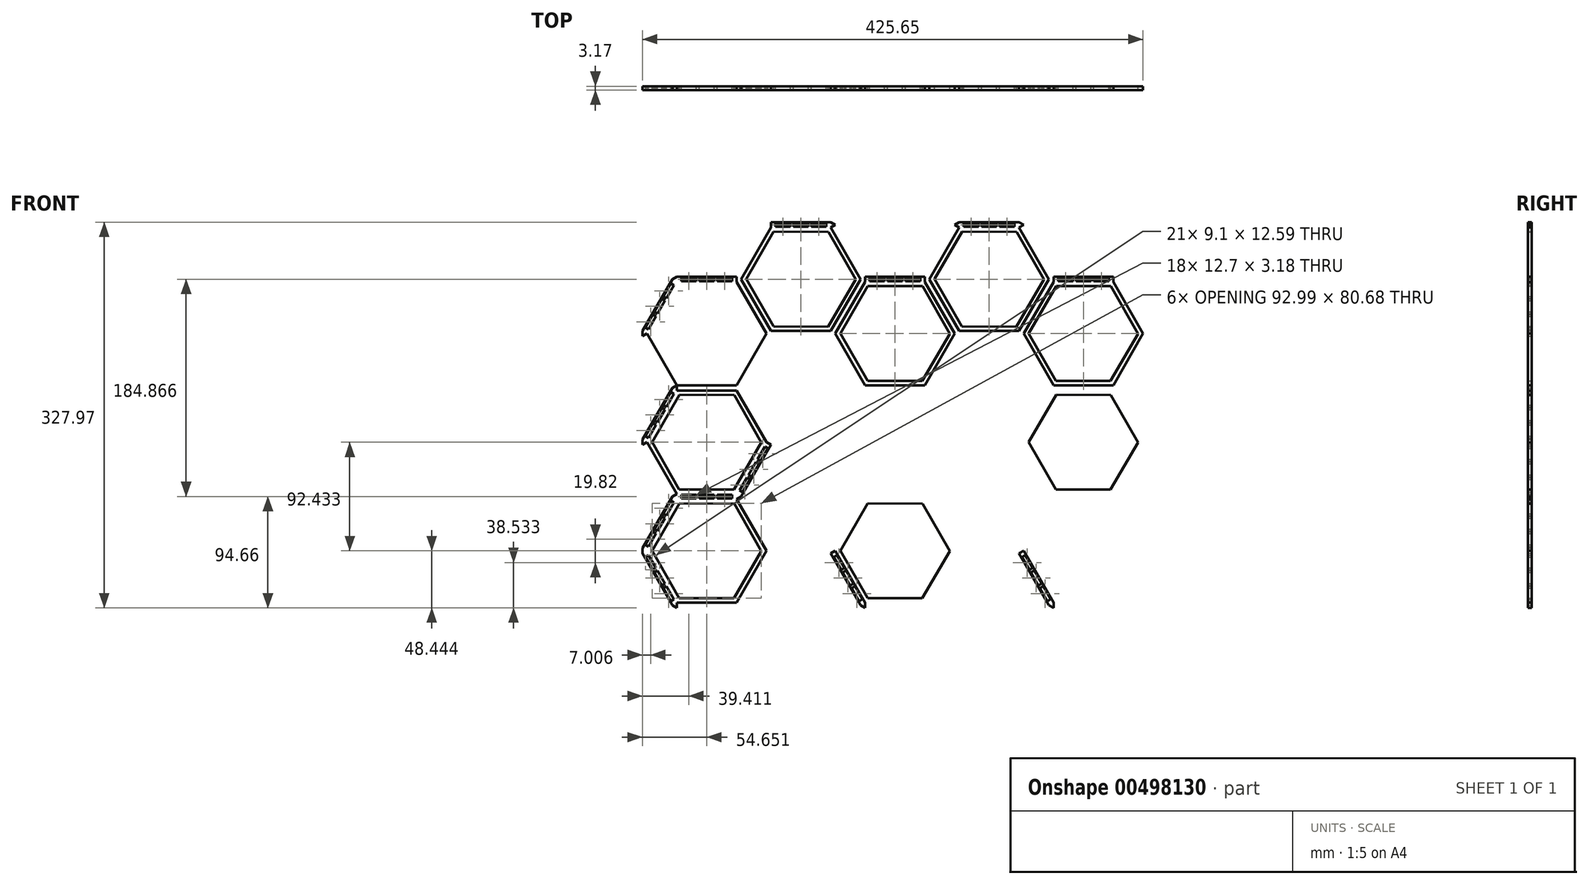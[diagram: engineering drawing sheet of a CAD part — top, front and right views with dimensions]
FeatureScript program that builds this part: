
annotation { "Feature Type Name" : "Feature", "Feature Type Description" : "" }
export const myFeature = defineFeature(function(context is Context, id is Id, definition is map)
    precondition{}
    {
        {
            var Q0;
            Q0=qCreatedBy(makeId("Front.planeOp"),FACE);
            var sketch = newSketch(context, id + "F0", { "sketchPlane" : qUnion([Q0])});
            skLineSegment(sketch, "E0", {"start": v(-1207.39, 180.55) * mm, "end": v(-1156.59, 180.55) * mm});
            skLineSegment(sketch, "E1", {"start": v(-1207.39, 185) * mm, "end": v(-1207.39, 180.55) * mm});
            skLineSegment(sketch, "E2", {"start": v(-1156.59, 185) * mm, "end": v(-1156.59, 180.55) * mm});
            skPoint(sketch, "E3.endSnap0", {"position": v(-1156.59, 182.78) * mm});
            skLineSegment(sketch, "E4", {"start": v(-1207.39, 182.78) * mm, "end": v(-1156.59, 182.78) * mm, "construction": true});
            skLineSegment(sketch, "E5", {"start": v(-1207.39, 185) * mm, "end": v(-1156.59, 185) * mm});
            skLineSegment(sketch, "E6.left", {"start": v(-1160.4, 181.19) * mm, "end": v(-1160.4, 184.36) * mm});
            skLineSegment(sketch, "E6.right", {"start": v(-1203.58, 181.19) * mm, "end": v(-1203.58, 184.36) * mm});
            skPoint(sketch, "E6.middle", {"position": v(-1181.99, 182.78) * mm});
            skLineSegment(sketch, "E7", {"start": v(-1181.99, 184.36) * mm, "end": v(-1181.99, 181.19) * mm, "construction": true});
            skLineSegment(sketch, "E8", {"start": v(-1190.88, 184.36) * mm, "end": v(-1190.88, 181.19) * mm});
            skLineSegment(sketch, "E9.MirrorCS", {"start": v(-1173.1, 184.36) * mm, "end": v(-1173.1, 181.19) * mm});
            skLineSegment(sketch, "E10", {"start": v(-1188.34, 184.36) * mm, "end": v(-1188.34, 181.19) * mm});
            skLineSegment(sketch, "E11.MirrorCS", {"start": v(-1175.64, 184.36) * mm, "end": v(-1175.64, 181.19) * mm});
            skLineSegment(sketch, "E12", {"start": v(-1203.58, 184.36) * mm, "end": v(-1190.88, 184.36) * mm});
            skLineSegment(sketch, "E13", {"start": v(-1203.58, 181.19) * mm, "end": v(-1190.88, 181.19) * mm});
            skLineSegment(sketch, "E14", {"start": v(-1188.34, 181.19) * mm, "end": v(-1181.99, 181.19) * mm});
            skLineSegment(sketch, "E15", {"start": v(-1188.34, 184.36) * mm, "end": v(-1181.99, 184.36) * mm});
            skLineSegment(sketch, "E16", {"start": v(-1181.99, 184.36) * mm, "end": v(-1175.64, 184.36) * mm});
            skLineSegment(sketch, "E17", {"start": v(-1181.99, 181.19) * mm, "end": v(-1175.64, 181.19) * mm});
            skLineSegment(sketch, "E18", {"start": v(-1173.1, 184.36) * mm, "end": v(-1160.4, 184.36) * mm});
            skLineSegment(sketch, "E19", {"start": v(-1173.1, 181.19) * mm, "end": v(-1160.4, 181.19) * mm});
            skLineSegment(sketch, "E20", {"start": v(-1152.74, 182.78) * mm, "end": v(-1156.59, 180.55) * mm});
            skLineSegment(sketch, "E21", {"start": v(-1211.24, 182.78) * mm, "end": v(-1207.39, 180.55) * mm});
            skPoint(sketch, "E22.endSnap0", {"position": v(-1209.31, 181.67) * mm});
            skLineSegment(sketch, "E23.0", {"start": v(-1207.39, 180.55) * mm, "end": v(-1211.24, 182.78) * mm, "construction": true});
            skLineSegment(sketch, "E24", {"start": v(-1207.39, 272.99) * mm, "end": v(-1156.59, 272.99) * mm});
            skLineSegment(sketch, "E25", {"start": v(-1207.39, 277.43) * mm, "end": v(-1207.39, 272.99) * mm});
            skLineSegment(sketch, "E26", {"start": v(-1156.59, 277.43) * mm, "end": v(-1156.59, 272.99) * mm});
            skPoint(sketch, "E27.endSnap0", {"position": v(-1156.59, 275.21) * mm});
            skLineSegment(sketch, "E28", {"start": v(-1207.39, 275.21) * mm, "end": v(-1156.59, 275.21) * mm, "construction": true});
            skLineSegment(sketch, "E29", {"start": v(-1207.39, 277.43) * mm, "end": v(-1156.59, 277.43) * mm});
            skLineSegment(sketch, "E30", {"start": v(-1236.64, 231.22) * mm, "end": v(-1232.79, 229) * mm});
            skLineSegment(sketch, "E31.left", {"start": v(-1160.4, 273.62) * mm, "end": v(-1160.4, 276.8) * mm});
            skLineSegment(sketch, "E31.right", {"start": v(-1203.58, 273.62) * mm, "end": v(-1203.58, 276.8) * mm});
            skPoint(sketch, "E31.middle", {"position": v(-1181.99, 275.21) * mm});
            skLineSegment(sketch, "E32", {"start": v(-1181.99, 276.8) * mm, "end": v(-1181.99, 273.62) * mm, "construction": true});
            skLineSegment(sketch, "E33", {"start": v(-1190.88, 276.8) * mm, "end": v(-1190.88, 273.62) * mm});
            skLineSegment(sketch, "E34.MirrorCS", {"start": v(-1173.1, 276.8) * mm, "end": v(-1173.1, 273.62) * mm});
            skLineSegment(sketch, "E35", {"start": v(-1188.34, 276.8) * mm, "end": v(-1188.34, 273.62) * mm});
            skLineSegment(sketch, "E36.MirrorCS", {"start": v(-1175.64, 276.8) * mm, "end": v(-1175.64, 273.62) * mm});
            skLineSegment(sketch, "E37", {"start": v(-1203.58, 276.8) * mm, "end": v(-1190.88, 276.8) * mm});
            skLineSegment(sketch, "E38", {"start": v(-1203.58, 273.62) * mm, "end": v(-1190.88, 273.62) * mm});
            skLineSegment(sketch, "E39", {"start": v(-1188.34, 273.62) * mm, "end": v(-1181.99, 273.62) * mm});
            skLineSegment(sketch, "E40", {"start": v(-1188.34, 276.8) * mm, "end": v(-1181.99, 276.8) * mm});
            skLineSegment(sketch, "E41", {"start": v(-1181.99, 276.8) * mm, "end": v(-1175.64, 276.8) * mm});
            skLineSegment(sketch, "E42", {"start": v(-1181.99, 273.62) * mm, "end": v(-1175.64, 273.62) * mm});
            skLineSegment(sketch, "E43", {"start": v(-1173.1, 276.8) * mm, "end": v(-1160.4, 276.8) * mm});
            skLineSegment(sketch, "E44", {"start": v(-1173.1, 273.62) * mm, "end": v(-1160.4, 273.62) * mm});
            skLineSegment(sketch, "E45", {"start": v(-1156.59, 272.99) * mm, "end": v(-1131.19, 229) * mm});
            skLineSegment(sketch, "E46", {"start": v(-1152.74, 275.21) * mm, "end": v(-1156.59, 272.99) * mm});
            skLineSegment(sketch, "E47", {"start": v(-1152.74, 275.21) * mm, "end": v(-1127.34, 231.22) * mm});
            skLineSegment(sketch, "E48.left", {"start": v(-1132.54, 232.61) * mm, "end": v(-1129.8, 234.2) * mm});
            skLineSegment(sketch, "E48.right", {"start": v(-1154.13, 270) * mm, "end": v(-1151.38, 271.6) * mm});
            skPoint(sketch, "E48.middle", {"position": v(-1141.96, 252.1) * mm});
            skLineSegment(sketch, "E49", {"start": v(-1140.59, 252.9) * mm, "end": v(-1143.34, 251.3) * mm, "construction": true});
            skLineSegment(sketch, "E50", {"start": v(-1145.03, 260.6) * mm, "end": v(-1147.78, 259) * mm});
            skLineSegment(sketch, "E51.MirrorCS", {"start": v(-1136.14, 245.2) * mm, "end": v(-1138.9, 243.6) * mm});
            skLineSegment(sketch, "E52", {"start": v(-1143.76, 258.4) * mm, "end": v(-1146.51, 256.8) * mm});
            skLineSegment(sketch, "E53.MirrorCS", {"start": v(-1137.41, 247.4) * mm, "end": v(-1140.16, 245.8) * mm});
            skLineSegment(sketch, "E54", {"start": v(-1151.38, 271.6) * mm, "end": v(-1145.03, 260.6) * mm});
            skLineSegment(sketch, "E55", {"start": v(-1154.13, 270) * mm, "end": v(-1147.78, 259) * mm});
            skLineSegment(sketch, "E56", {"start": v(-1146.51, 256.8) * mm, "end": v(-1143.34, 251.3) * mm});
            skLineSegment(sketch, "E57", {"start": v(-1143.76, 258.4) * mm, "end": v(-1140.59, 252.9) * mm});
            skLineSegment(sketch, "E58", {"start": v(-1140.59, 252.9) * mm, "end": v(-1137.41, 247.4) * mm});
            skLineSegment(sketch, "E59", {"start": v(-1143.34, 251.3) * mm, "end": v(-1140.16, 245.8) * mm});
            skLineSegment(sketch, "E60", {"start": v(-1136.14, 245.2) * mm, "end": v(-1129.8, 234.2) * mm});
            skLineSegment(sketch, "E61", {"start": v(-1138.9, 243.6) * mm, "end": v(-1132.54, 232.61) * mm});
            skLineSegment(sketch, "E62", {"start": v(-1232.79, 229) * mm, "end": v(-1207.39, 272.99) * mm});
            skLineSegment(sketch, "E63", {"start": v(-1211.24, 275.21) * mm, "end": v(-1207.39, 272.99) * mm});
            skPoint(sketch, "E64.endSnap0", {"position": v(-1209.31, 274.1) * mm});
            skLineSegment(sketch, "E65", {"start": v(-1236.64, 231.22) * mm, "end": v(-1211.24, 275.21) * mm});
            skLineSegment(sketch, "E66.left", {"start": v(-1209.84, 270) * mm, "end": v(-1212.6, 271.6) * mm});
            skLineSegment(sketch, "E66.right", {"start": v(-1231.43, 232.61) * mm, "end": v(-1234.18, 234.2) * mm});
            skPoint(sketch, "E66.middle", {"position": v(-1222.01, 252.1) * mm});
            skLineSegment(sketch, "E67", {"start": v(-1223.39, 252.9) * mm, "end": v(-1220.64, 251.3) * mm, "construction": true});
            skLineSegment(sketch, "E68", {"start": v(-1227.83, 245.2) * mm, "end": v(-1225.08, 243.6) * mm});
            skLineSegment(sketch, "E69.MirrorCS", {"start": v(-1218.94, 260.6) * mm, "end": v(-1216.2, 259) * mm});
            skLineSegment(sketch, "E70", {"start": v(-1226.56, 247.4) * mm, "end": v(-1223.81, 245.8) * mm});
            skLineSegment(sketch, "E71.MirrorCS", {"start": v(-1220.21, 258.4) * mm, "end": v(-1217.46, 256.8) * mm});
            skLineSegment(sketch, "E72", {"start": v(-1234.18, 234.2) * mm, "end": v(-1227.83, 245.2) * mm});
            skLineSegment(sketch, "E73", {"start": v(-1231.43, 232.61) * mm, "end": v(-1225.08, 243.6) * mm});
            skLineSegment(sketch, "E74", {"start": v(-1223.81, 245.8) * mm, "end": v(-1220.64, 251.3) * mm});
            skLineSegment(sketch, "E75", {"start": v(-1226.56, 247.4) * mm, "end": v(-1223.39, 252.9) * mm});
            skLineSegment(sketch, "E76", {"start": v(-1223.39, 252.9) * mm, "end": v(-1220.21, 258.4) * mm});
            skLineSegment(sketch, "E77", {"start": v(-1220.64, 251.3) * mm, "end": v(-1217.46, 256.8) * mm});
            skLineSegment(sketch, "E78", {"start": v(-1218.94, 260.6) * mm, "end": v(-1212.6, 271.6) * mm});
            skLineSegment(sketch, "E79", {"start": v(-1216.2, 259) * mm, "end": v(-1209.84, 270) * mm});
            skLineSegment(sketch, "E80.0", {"start": v(-1207.39, 272.99) * mm, "end": v(-1211.24, 275.21) * mm, "construction": true});
            skLineSegment(sketch, "E81", {"start": v(-1131.19, 229) * mm, "end": v(-1127.34, 231.22) * mm});
            skLineSegment(sketch, "E82.MirrorCS", {"start": v(-1211.24, 182.78) * mm, "end": v(-1207.39, 185) * mm});
            skLineSegment(sketch, "E83.MirrorCS", {"start": v(-1140.59, 205.1) * mm, "end": v(-1143.34, 206.68) * mm, "construction": true});
            skLineSegment(sketch, "E84.MirrorCS", {"start": v(-1223.39, 205.1) * mm, "end": v(-1220.64, 206.68) * mm, "construction": true});
            skLineSegment(sketch, "E85.MirrorCS", {"start": v(-1181.99, 181.19) * mm, "end": v(-1181.99, 184.36) * mm, "construction": true});
            skLineSegment(sketch, "E86.MirrorCS", {"start": v(-1207.39, 185) * mm, "end": v(-1211.24, 182.78) * mm, "construction": true});
            skLineSegment(sketch, "E87.MirrorCS", {"start": v(-1152.74, 182.78) * mm, "end": v(-1156.59, 185) * mm});
            skLineSegment(sketch, "E88.MirrorCS", {"start": v(-1154.13, 187.98) * mm, "end": v(-1151.38, 186.4) * mm});
            skLineSegment(sketch, "E89.MirrorCS", {"start": v(-1220.21, 199.6) * mm, "end": v(-1217.46, 201.18) * mm});
            skLineSegment(sketch, "E90.MirrorCS", {"start": v(-1175.64, 181.19) * mm, "end": v(-1175.64, 184.36) * mm});
            skLineSegment(sketch, "E91.MirrorCS", {"start": v(-1156.59, 180.55) * mm, "end": v(-1156.59, 185) * mm});
            skLineSegment(sketch, "E92.MirrorCS", {"start": v(-1190.88, 181.19) * mm, "end": v(-1190.88, 184.36) * mm});
            skLineSegment(sketch, "E93.MirrorCS", {"start": v(-1145.03, 197.4) * mm, "end": v(-1147.78, 198.98) * mm});
            skLineSegment(sketch, "E94.MirrorCS", {"start": v(-1188.34, 181.19) * mm, "end": v(-1188.34, 184.36) * mm});
            skLineSegment(sketch, "E95.MirrorCS", {"start": v(-1209.84, 187.98) * mm, "end": v(-1212.6, 186.4) * mm});
            skLineSegment(sketch, "E96.MirrorCS", {"start": v(-1231.43, 225.38) * mm, "end": v(-1234.18, 223.79) * mm});
            skLineSegment(sketch, "E97.MirrorCS", {"start": v(-1226.56, 210.6) * mm, "end": v(-1223.81, 212.18) * mm});
            skLineSegment(sketch, "E98.MirrorCS", {"start": v(-1236.64, 226.77) * mm, "end": v(-1232.79, 229) * mm});
            skLineSegment(sketch, "E99.MirrorCS", {"start": v(-1143.76, 199.6) * mm, "end": v(-1146.51, 201.18) * mm});
            skLineSegment(sketch, "E100.MirrorCS", {"start": v(-1173.1, 181.19) * mm, "end": v(-1173.1, 184.36) * mm});
            skLineSegment(sketch, "E101.MirrorCS", {"start": v(-1227.83, 212.8) * mm, "end": v(-1225.08, 214.38) * mm});
            skLineSegment(sketch, "E102.MirrorCS", {"start": v(-1132.54, 225.38) * mm, "end": v(-1129.8, 223.79) * mm});
            skLineSegment(sketch, "E103.MirrorCS", {"start": v(-1203.58, 184.36) * mm, "end": v(-1203.58, 181.19) * mm});
            skLineSegment(sketch, "E104.MirrorCS", {"start": v(-1136.14, 212.8) * mm, "end": v(-1138.9, 214.38) * mm});
            skLineSegment(sketch, "E105.MirrorCS", {"start": v(-1131.19, 229) * mm, "end": v(-1127.34, 226.77) * mm});
            skLineSegment(sketch, "E106.MirrorCS", {"start": v(-1137.41, 210.6) * mm, "end": v(-1140.16, 212.18) * mm});
            skLineSegment(sketch, "E107.MirrorCS", {"start": v(-1218.94, 197.4) * mm, "end": v(-1216.2, 198.98) * mm});
            skLineSegment(sketch, "E108.MirrorCS", {"start": v(-1160.4, 184.36) * mm, "end": v(-1160.4, 181.19) * mm});
            skLineSegment(sketch, "E109.MirrorCS", {"start": v(-1146.51, 201.18) * mm, "end": v(-1143.34, 206.68) * mm});
            skLineSegment(sketch, "E110.MirrorCS", {"start": v(-1223.81, 212.18) * mm, "end": v(-1220.64, 206.68) * mm});
            skLineSegment(sketch, "E111.MirrorCS", {"start": v(-1140.59, 205.1) * mm, "end": v(-1137.41, 210.6) * mm});
            skLineSegment(sketch, "E112.MirrorCS", {"start": v(-1207.39, 180.55) * mm, "end": v(-1207.39, 185) * mm});
            skLineSegment(sketch, "E113.MirrorCS", {"start": v(-1143.34, 206.68) * mm, "end": v(-1140.16, 212.18) * mm});
            skLineSegment(sketch, "E114.MirrorCS", {"start": v(-1143.76, 199.6) * mm, "end": v(-1140.59, 205.1) * mm});
            skLineSegment(sketch, "E115.MirrorCS", {"start": v(-1220.64, 206.68) * mm, "end": v(-1217.46, 201.18) * mm});
            skLineSegment(sketch, "E116.MirrorCS", {"start": v(-1138.9, 214.38) * mm, "end": v(-1132.54, 225.38) * mm});
            skLineSegment(sketch, "E117.MirrorCS", {"start": v(-1236.64, 226.77) * mm, "end": v(-1211.24, 182.78) * mm});
            skLineSegment(sketch, "E118.MirrorCS", {"start": v(-1156.59, 185) * mm, "end": v(-1131.19, 229) * mm});
            skLineSegment(sketch, "E119.MirrorCS", {"start": v(-1151.38, 186.4) * mm, "end": v(-1145.03, 197.4) * mm});
            skLineSegment(sketch, "E120.MirrorCS", {"start": v(-1231.43, 225.38) * mm, "end": v(-1225.08, 214.38) * mm});
            skLineSegment(sketch, "E121.MirrorCS", {"start": v(-1216.2, 198.98) * mm, "end": v(-1209.84, 187.98) * mm});
            skPoint(sketch, "E122.MirrorP", {"position": v(-1141.96, 205.89) * mm});
            skLineSegment(sketch, "E123.MirrorCS", {"start": v(-1136.14, 212.8) * mm, "end": v(-1129.8, 223.79) * mm});
            skPoint(sketch, "E124.MirrorP", {"position": v(-1209.31, 183.89) * mm});
            skLineSegment(sketch, "E125.MirrorCS", {"start": v(-1226.56, 210.6) * mm, "end": v(-1223.39, 205.1) * mm});
            skPoint(sketch, "E126.MirrorP", {"position": v(-1222.01, 205.89) * mm});
            skLineSegment(sketch, "E127.MirrorCS", {"start": v(-1154.13, 187.98) * mm, "end": v(-1147.78, 198.98) * mm});
            skLineSegment(sketch, "E128.MirrorCS", {"start": v(-1152.74, 182.78) * mm, "end": v(-1127.34, 226.77) * mm});
            skLineSegment(sketch, "E129.MirrorCS", {"start": v(-1232.79, 229) * mm, "end": v(-1207.39, 185) * mm});
            skLineSegment(sketch, "E130.MirrorCS", {"start": v(-1218.94, 197.4) * mm, "end": v(-1212.6, 186.4) * mm});
            skLineSegment(sketch, "E131.MirrorCS", {"start": v(-1234.18, 223.79) * mm, "end": v(-1227.83, 212.8) * mm});
            skLineSegment(sketch, "E132.MirrorCS", {"start": v(-1223.39, 205.1) * mm, "end": v(-1220.21, 199.6) * mm});
            skLineSegment(sketch, "E133", {"start": v(-1127.34, 231.22) * mm, "end": v(-1127.34, 226.77) * mm});
            skLineSegment(sketch, "E134", {"start": v(-1156.59, 185) * mm, "end": v(-1152.74, 182.78) * mm});
            skLineSegment(sketch, "E135.left", {"start": v(-1129.8, 223.79) * mm, "end": v(-1132.54, 225.38) * mm});
            skLineSegment(sketch, "E135.right", {"start": v(-1151.38, 186.4) * mm, "end": v(-1154.13, 187.98) * mm});
            skLineSegment(sketch, "E136", {"start": v(-1143.34, 206.68) * mm, "end": v(-1140.59, 205.1) * mm, "construction": true});
            skLineSegment(sketch, "E137", {"start": v(-1147.78, 198.98) * mm, "end": v(-1145.03, 197.4) * mm});
            skLineSegment(sketch, "E138.MirrorCS", {"start": v(-1138.9, 214.38) * mm, "end": v(-1136.14, 212.8) * mm});
            skLineSegment(sketch, "E139", {"start": v(-1146.51, 201.18) * mm, "end": v(-1143.76, 199.6) * mm});
            skLineSegment(sketch, "E140.MirrorCS", {"start": v(-1140.16, 212.18) * mm, "end": v(-1137.41, 210.6) * mm});
            skLineSegment(sketch, "E141.0", {"start": v(-1127.34, 226.77) * mm, "end": v(-1131.19, 229) * mm, "construction": true});
            skLineSegment(sketch, "E142.MirrorCS", {"start": v(-1156.59, 180.55) * mm, "end": v(-1152.74, 182.78) * mm});
            skLineSegment(sketch, "E143", {"start": v(-1156.59, 277.43) * mm, "end": v(-1152.74, 275.21) * mm});
            skLineSegment(sketch, "E144.MirrorCS", {"start": v(-1143.34, 251.3) * mm, "end": v(-1140.59, 252.9) * mm, "construction": true});
            skLineSegment(sketch, "E145.MirrorCS", {"start": v(-1127.34, 231.22) * mm, "end": v(-1131.19, 229) * mm, "construction": true});
            skLineSegment(sketch, "E146.MirrorCS", {"start": v(-1140.16, 245.8) * mm, "end": v(-1137.41, 247.4) * mm});
            skLineSegment(sketch, "E147.MirrorCS", {"start": v(-1129.8, 234.2) * mm, "end": v(-1132.54, 232.61) * mm});
            skLineSegment(sketch, "E148.MirrorCS", {"start": v(-1151.38, 271.6) * mm, "end": v(-1154.13, 270) * mm});
            skLineSegment(sketch, "E149.MirrorCS", {"start": v(-1146.51, 256.8) * mm, "end": v(-1143.76, 258.4) * mm});
            skLineSegment(sketch, "E150.MirrorCS", {"start": v(-1156.59, 272.99) * mm, "end": v(-1152.74, 275.21) * mm});
            skLineSegment(sketch, "E151.MirrorCS", {"start": v(-1147.78, 259) * mm, "end": v(-1145.03, 260.6) * mm});
            skLineSegment(sketch, "E152.MirrorCS", {"start": v(-1138.9, 243.6) * mm, "end": v(-1136.14, 245.2) * mm});
            skLineSegment(sketch, "E153.MirrorCS", {"start": v(-1127.34, 226.77) * mm, "end": v(-1127.34, 231.22) * mm});
            skLineSegment(sketch, "E154", {"start": v(-1236.64, 231.22) * mm, "end": v(-1236.64, 226.77) * mm});
            skLineSegment(sketch, "E155", {"start": v(-1207.39, 277.43) * mm, "end": v(-1211.24, 275.21) * mm});
            skLineSegment(sketch, "E156.0", {"start": v(-1135.5, 228.85) * mm, "end": v(-1158.86, 188.66) * mm});
            skLineSegment(sketch, "E156.1", {"start": v(-1158.86, 188.66) * mm, "end": v(-1205.36, 188.8) * mm});
            skLineSegment(sketch, "E156.2", {"start": v(-1205.36, 188.8) * mm, "end": v(-1228.49, 229.14) * mm});
            skLineSegment(sketch, "E156.3", {"start": v(-1228.49, 229.14) * mm, "end": v(-1205.11, 269.33) * mm});
            skLineSegment(sketch, "E156.4", {"start": v(-1205.11, 269.33) * mm, "end": v(-1158.62, 269.19) * mm});
            skLineSegment(sketch, "E156.5", {"start": v(-1158.62, 269.19) * mm, "end": v(-1135.5, 228.85) * mm});
            skPoint(sketch, "E156.0.midPoint", {"position": v(-1147.18, 208.75) * mm});
            skLineSegment(sketch, "E157", {"start": v(-1207.39, 365.42) * mm, "end": v(-1156.59, 365.42) * mm});
            skLineSegment(sketch, "E158", {"start": v(-1207.39, 369.87) * mm, "end": v(-1207.39, 365.42) * mm});
            skLineSegment(sketch, "E159", {"start": v(-1156.59, 369.87) * mm, "end": v(-1156.59, 365.42) * mm});
            skPoint(sketch, "E160.endSnap0", {"position": v(-1156.59, 367.64) * mm});
            skLineSegment(sketch, "E161", {"start": v(-1207.39, 367.64) * mm, "end": v(-1156.59, 367.64) * mm, "construction": true});
            skLineSegment(sketch, "E162", {"start": v(-1207.39, 369.87) * mm, "end": v(-1156.59, 369.87) * mm});
            skLineSegment(sketch, "E163", {"start": v(-1236.64, 323.65) * mm, "end": v(-1232.79, 321.43) * mm});
            skLineSegment(sketch, "E164.left", {"start": v(-1160.4, 366.06) * mm, "end": v(-1160.4, 369.23) * mm});
            skLineSegment(sketch, "E164.right", {"start": v(-1203.58, 366.06) * mm, "end": v(-1203.58, 369.23) * mm});
            skPoint(sketch, "E164.middle", {"position": v(-1181.99, 367.64) * mm});
            skLineSegment(sketch, "E165", {"start": v(-1181.99, 369.23) * mm, "end": v(-1181.99, 366.06) * mm, "construction": true});
            skLineSegment(sketch, "E166", {"start": v(-1190.88, 369.23) * mm, "end": v(-1190.88, 366.06) * mm});
            skLineSegment(sketch, "E167.MirrorCS", {"start": v(-1173.1, 369.23) * mm, "end": v(-1173.1, 366.06) * mm});
            skLineSegment(sketch, "E168", {"start": v(-1188.34, 369.23) * mm, "end": v(-1188.34, 366.06) * mm});
            skLineSegment(sketch, "E169.MirrorCS", {"start": v(-1175.64, 369.23) * mm, "end": v(-1175.64, 366.06) * mm});
            skLineSegment(sketch, "E170", {"start": v(-1203.58, 369.23) * mm, "end": v(-1190.88, 369.23) * mm});
            skLineSegment(sketch, "E171", {"start": v(-1203.58, 366.06) * mm, "end": v(-1190.88, 366.06) * mm});
            skLineSegment(sketch, "E172", {"start": v(-1188.34, 366.06) * mm, "end": v(-1181.99, 366.06) * mm});
            skLineSegment(sketch, "E173", {"start": v(-1188.34, 369.23) * mm, "end": v(-1181.99, 369.23) * mm});
            skLineSegment(sketch, "E174", {"start": v(-1181.99, 369.23) * mm, "end": v(-1175.64, 369.23) * mm});
            skLineSegment(sketch, "E175", {"start": v(-1181.99, 366.06) * mm, "end": v(-1175.64, 366.06) * mm});
            skLineSegment(sketch, "E176", {"start": v(-1173.1, 369.23) * mm, "end": v(-1160.4, 369.23) * mm});
            skLineSegment(sketch, "E177", {"start": v(-1173.1, 366.06) * mm, "end": v(-1160.4, 366.06) * mm});
            skLineSegment(sketch, "E178", {"start": v(-1156.59, 365.42) * mm, "end": v(-1131.19, 321.43) * mm});
            skLineSegment(sketch, "E179", {"start": v(-1152.74, 367.64) * mm, "end": v(-1156.59, 365.42) * mm});
            skLineSegment(sketch, "E180", {"start": v(-1152.74, 367.64) * mm, "end": v(-1127.34, 323.65) * mm});
            skLineSegment(sketch, "E181.left", {"start": v(-1132.54, 325.04) * mm, "end": v(-1129.8, 326.63) * mm});
            skLineSegment(sketch, "E181.right", {"start": v(-1154.13, 362.44) * mm, "end": v(-1151.38, 364.03) * mm});
            skPoint(sketch, "E181.middle", {"position": v(-1141.96, 344.53) * mm});
            skLineSegment(sketch, "E182", {"start": v(-1140.59, 345.33) * mm, "end": v(-1143.34, 343.74) * mm, "construction": true});
            skLineSegment(sketch, "E183", {"start": v(-1145.03, 353.03) * mm, "end": v(-1147.78, 351.44) * mm});
            skLineSegment(sketch, "E184.MirrorCS", {"start": v(-1136.14, 337.63) * mm, "end": v(-1138.9, 336.04) * mm});
            skLineSegment(sketch, "E185", {"start": v(-1143.76, 350.83) * mm, "end": v(-1146.51, 349.24) * mm});
            skLineSegment(sketch, "E186.MirrorCS", {"start": v(-1137.41, 339.83) * mm, "end": v(-1140.16, 338.24) * mm});
            skLineSegment(sketch, "E187", {"start": v(-1151.38, 364.03) * mm, "end": v(-1145.03, 353.03) * mm});
            skLineSegment(sketch, "E188", {"start": v(-1154.13, 362.44) * mm, "end": v(-1147.78, 351.44) * mm});
            skLineSegment(sketch, "E189", {"start": v(-1146.51, 349.24) * mm, "end": v(-1143.34, 343.74) * mm});
            skLineSegment(sketch, "E190", {"start": v(-1143.76, 350.83) * mm, "end": v(-1140.59, 345.33) * mm});
            skLineSegment(sketch, "E191", {"start": v(-1140.59, 345.33) * mm, "end": v(-1137.41, 339.83) * mm});
            skLineSegment(sketch, "E192", {"start": v(-1143.34, 343.74) * mm, "end": v(-1140.16, 338.24) * mm});
            skLineSegment(sketch, "E193", {"start": v(-1136.14, 337.63) * mm, "end": v(-1129.8, 326.63) * mm});
            skLineSegment(sketch, "E194", {"start": v(-1138.9, 336.04) * mm, "end": v(-1132.54, 325.04) * mm});
            skLineSegment(sketch, "E195", {"start": v(-1232.79, 321.43) * mm, "end": v(-1207.39, 365.42) * mm});
            skLineSegment(sketch, "E196", {"start": v(-1211.24, 367.64) * mm, "end": v(-1207.39, 365.42) * mm});
            skPoint(sketch, "E197.endSnap0", {"position": v(-1209.31, 366.53) * mm});
            skLineSegment(sketch, "E198", {"start": v(-1236.64, 323.65) * mm, "end": v(-1211.24, 367.64) * mm});
            skLineSegment(sketch, "E199.left", {"start": v(-1209.84, 362.44) * mm, "end": v(-1212.6, 364.03) * mm});
            skLineSegment(sketch, "E199.right", {"start": v(-1231.43, 325.04) * mm, "end": v(-1234.18, 326.63) * mm});
            skPoint(sketch, "E199.middle", {"position": v(-1222.01, 344.53) * mm});
            skLineSegment(sketch, "E200", {"start": v(-1223.39, 345.33) * mm, "end": v(-1220.64, 343.74) * mm, "construction": true});
            skLineSegment(sketch, "E201", {"start": v(-1227.83, 337.63) * mm, "end": v(-1225.08, 336.04) * mm});
            skLineSegment(sketch, "E202.MirrorCS", {"start": v(-1218.94, 353.03) * mm, "end": v(-1216.2, 351.44) * mm});
            skLineSegment(sketch, "E203", {"start": v(-1226.56, 339.83) * mm, "end": v(-1223.81, 338.24) * mm});
            skLineSegment(sketch, "E204.MirrorCS", {"start": v(-1220.21, 350.83) * mm, "end": v(-1217.46, 349.24) * mm});
            skLineSegment(sketch, "E205", {"start": v(-1234.18, 326.63) * mm, "end": v(-1227.83, 337.63) * mm});
            skLineSegment(sketch, "E206", {"start": v(-1231.43, 325.04) * mm, "end": v(-1225.08, 336.04) * mm});
            skLineSegment(sketch, "E207", {"start": v(-1223.81, 338.24) * mm, "end": v(-1220.64, 343.74) * mm});
            skLineSegment(sketch, "E208", {"start": v(-1226.56, 339.83) * mm, "end": v(-1223.39, 345.33) * mm});
            skLineSegment(sketch, "E209", {"start": v(-1223.39, 345.33) * mm, "end": v(-1220.21, 350.83) * mm});
            skLineSegment(sketch, "E210", {"start": v(-1220.64, 343.74) * mm, "end": v(-1217.46, 349.24) * mm});
            skLineSegment(sketch, "E211", {"start": v(-1218.94, 353.03) * mm, "end": v(-1212.6, 364.03) * mm});
            skLineSegment(sketch, "E212", {"start": v(-1216.2, 351.44) * mm, "end": v(-1209.84, 362.44) * mm});
            skLineSegment(sketch, "E213.0", {"start": v(-1207.39, 365.42) * mm, "end": v(-1211.24, 367.64) * mm, "construction": true});
            skLineSegment(sketch, "E214", {"start": v(-1131.19, 321.43) * mm, "end": v(-1127.34, 323.65) * mm});
            skLineSegment(sketch, "E215.MirrorCS", {"start": v(-1211.24, 275.21) * mm, "end": v(-1207.39, 277.43) * mm});
            skLineSegment(sketch, "E216.MirrorCS", {"start": v(-1140.59, 297.52) * mm, "end": v(-1143.34, 299.11) * mm, "construction": true});
            skLineSegment(sketch, "E217.MirrorCS", {"start": v(-1223.39, 297.52) * mm, "end": v(-1220.64, 299.11) * mm, "construction": true});
            skLineSegment(sketch, "E218.MirrorCS", {"start": v(-1181.99, 273.62) * mm, "end": v(-1181.99, 276.8) * mm, "construction": true});
            skLineSegment(sketch, "E219.MirrorCS", {"start": v(-1207.39, 277.43) * mm, "end": v(-1211.24, 275.21) * mm, "construction": true});
            skLineSegment(sketch, "E220.MirrorCS", {"start": v(-1152.74, 275.21) * mm, "end": v(-1156.59, 277.43) * mm});
            skLineSegment(sketch, "E221.MirrorCS", {"start": v(-1154.13, 280.41) * mm, "end": v(-1151.38, 278.83) * mm});
            skLineSegment(sketch, "E222.MirrorCS", {"start": v(-1220.21, 292.03) * mm, "end": v(-1217.46, 293.61) * mm});
            skLineSegment(sketch, "E223.MirrorCS", {"start": v(-1175.64, 273.62) * mm, "end": v(-1175.64, 276.8) * mm});
            skLineSegment(sketch, "E224.MirrorCS", {"start": v(-1156.59, 272.99) * mm, "end": v(-1156.59, 277.43) * mm});
            skLineSegment(sketch, "E225.MirrorCS", {"start": v(-1190.88, 273.62) * mm, "end": v(-1190.88, 276.8) * mm});
            skLineSegment(sketch, "E226.MirrorCS", {"start": v(-1145.03, 289.83) * mm, "end": v(-1147.78, 291.41) * mm});
            skLineSegment(sketch, "E227.MirrorCS", {"start": v(-1188.34, 273.62) * mm, "end": v(-1188.34, 276.8) * mm});
            skLineSegment(sketch, "E228.MirrorCS", {"start": v(-1209.84, 280.41) * mm, "end": v(-1212.6, 278.83) * mm});
            skLineSegment(sketch, "E229.MirrorCS", {"start": v(-1231.43, 317.8) * mm, "end": v(-1234.18, 316.22) * mm});
            skLineSegment(sketch, "E230.MirrorCS", {"start": v(-1226.56, 303.02) * mm, "end": v(-1223.81, 304.61) * mm});
            skLineSegment(sketch, "E231.MirrorCS", {"start": v(-1236.64, 319.2) * mm, "end": v(-1232.79, 321.43) * mm});
            skLineSegment(sketch, "E232.MirrorCS", {"start": v(-1143.76, 292.03) * mm, "end": v(-1146.51, 293.61) * mm});
            skLineSegment(sketch, "E233.MirrorCS", {"start": v(-1173.1, 273.62) * mm, "end": v(-1173.1, 276.8) * mm});
            skLineSegment(sketch, "E234.MirrorCS", {"start": v(-1227.83, 305.22) * mm, "end": v(-1225.08, 306.81) * mm});
            skLineSegment(sketch, "E235.MirrorCS", {"start": v(-1132.54, 317.8) * mm, "end": v(-1129.8, 316.22) * mm});
            skLineSegment(sketch, "E236.MirrorCS", {"start": v(-1203.58, 276.8) * mm, "end": v(-1203.58, 273.62) * mm});
            skLineSegment(sketch, "E237.MirrorCS", {"start": v(-1136.14, 305.22) * mm, "end": v(-1138.9, 306.81) * mm});
            skLineSegment(sketch, "E238.MirrorCS", {"start": v(-1131.19, 321.43) * mm, "end": v(-1127.34, 319.2) * mm});
            skLineSegment(sketch, "E239.MirrorCS", {"start": v(-1137.41, 303.02) * mm, "end": v(-1140.16, 304.61) * mm});
            skLineSegment(sketch, "E240.MirrorCS", {"start": v(-1218.94, 289.83) * mm, "end": v(-1216.2, 291.41) * mm});
            skLineSegment(sketch, "E241.MirrorCS", {"start": v(-1160.4, 276.8) * mm, "end": v(-1160.4, 273.62) * mm});
            skLineSegment(sketch, "E242.MirrorCS", {"start": v(-1146.51, 293.61) * mm, "end": v(-1143.34, 299.11) * mm});
            skLineSegment(sketch, "E243.MirrorCS", {"start": v(-1223.81, 304.61) * mm, "end": v(-1220.64, 299.11) * mm});
            skLineSegment(sketch, "E244.MirrorCS", {"start": v(-1140.59, 297.52) * mm, "end": v(-1137.41, 303.02) * mm});
            skLineSegment(sketch, "E245.MirrorCS", {"start": v(-1207.39, 272.99) * mm, "end": v(-1207.39, 277.43) * mm});
            skLineSegment(sketch, "E246.MirrorCS", {"start": v(-1143.34, 299.11) * mm, "end": v(-1140.16, 304.61) * mm});
            skLineSegment(sketch, "E247.MirrorCS", {"start": v(-1143.76, 292.03) * mm, "end": v(-1140.59, 297.52) * mm});
            skLineSegment(sketch, "E248.MirrorCS", {"start": v(-1220.64, 299.11) * mm, "end": v(-1217.46, 293.61) * mm});
            skLineSegment(sketch, "E249.MirrorCS", {"start": v(-1138.9, 306.81) * mm, "end": v(-1132.54, 317.8) * mm});
            skLineSegment(sketch, "E250.MirrorCS", {"start": v(-1236.64, 319.2) * mm, "end": v(-1211.24, 275.21) * mm});
            skLineSegment(sketch, "E251.MirrorCS", {"start": v(-1156.59, 277.43) * mm, "end": v(-1131.19, 321.43) * mm});
            skLineSegment(sketch, "E252.MirrorCS", {"start": v(-1151.38, 278.83) * mm, "end": v(-1145.03, 289.83) * mm});
            skLineSegment(sketch, "E253.MirrorCS", {"start": v(-1231.43, 317.8) * mm, "end": v(-1225.08, 306.81) * mm});
            skLineSegment(sketch, "E254.MirrorCS", {"start": v(-1216.2, 291.41) * mm, "end": v(-1209.84, 280.41) * mm});
            skPoint(sketch, "E255.MirrorP", {"position": v(-1141.96, 298.32) * mm});
            skLineSegment(sketch, "E256.MirrorCS", {"start": v(-1136.14, 305.22) * mm, "end": v(-1129.8, 316.22) * mm});
            skPoint(sketch, "E257.MirrorP", {"position": v(-1209.31, 276.32) * mm});
            skLineSegment(sketch, "E258.MirrorCS", {"start": v(-1226.56, 303.02) * mm, "end": v(-1223.39, 297.52) * mm});
            skPoint(sketch, "E259.MirrorP", {"position": v(-1222.01, 298.32) * mm});
            skLineSegment(sketch, "E260.MirrorCS", {"start": v(-1154.13, 280.41) * mm, "end": v(-1147.78, 291.41) * mm});
            skLineSegment(sketch, "E261.MirrorCS", {"start": v(-1152.74, 275.21) * mm, "end": v(-1127.34, 319.2) * mm});
            skLineSegment(sketch, "E262.MirrorCS", {"start": v(-1232.79, 321.43) * mm, "end": v(-1207.39, 277.43) * mm});
            skLineSegment(sketch, "E263.MirrorCS", {"start": v(-1218.94, 289.83) * mm, "end": v(-1212.6, 278.83) * mm});
            skLineSegment(sketch, "E264.MirrorCS", {"start": v(-1234.18, 316.22) * mm, "end": v(-1227.83, 305.22) * mm});
            skLineSegment(sketch, "E265.MirrorCS", {"start": v(-1223.39, 297.52) * mm, "end": v(-1220.21, 292.03) * mm});
            skLineSegment(sketch, "E266", {"start": v(-1127.34, 323.65) * mm, "end": v(-1127.34, 319.2) * mm});
            skLineSegment(sketch, "E267.left", {"start": v(-1129.8, 316.22) * mm, "end": v(-1132.54, 317.8) * mm});
            skLineSegment(sketch, "E267.right", {"start": v(-1151.38, 278.83) * mm, "end": v(-1154.13, 280.41) * mm});
            skLineSegment(sketch, "E268", {"start": v(-1143.34, 299.11) * mm, "end": v(-1140.59, 297.52) * mm, "construction": true});
            skLineSegment(sketch, "E269", {"start": v(-1147.78, 291.41) * mm, "end": v(-1145.03, 289.83) * mm});
            skLineSegment(sketch, "E270.MirrorCS", {"start": v(-1138.9, 306.81) * mm, "end": v(-1136.14, 305.22) * mm});
            skLineSegment(sketch, "E271", {"start": v(-1146.51, 293.61) * mm, "end": v(-1143.76, 292.03) * mm});
            skLineSegment(sketch, "E272.MirrorCS", {"start": v(-1140.16, 304.61) * mm, "end": v(-1137.41, 303.02) * mm});
            skLineSegment(sketch, "E273.0", {"start": v(-1127.34, 319.2) * mm, "end": v(-1131.19, 321.43) * mm, "construction": true});
            skLineSegment(sketch, "E274", {"start": v(-1156.59, 369.87) * mm, "end": v(-1152.74, 367.64) * mm});
            skLineSegment(sketch, "E275.MirrorCS", {"start": v(-1143.34, 343.74) * mm, "end": v(-1140.59, 345.33) * mm, "construction": true});
            skLineSegment(sketch, "E276.MirrorCS", {"start": v(-1127.34, 323.65) * mm, "end": v(-1131.19, 321.43) * mm, "construction": true});
            skLineSegment(sketch, "E277.MirrorCS", {"start": v(-1140.16, 338.24) * mm, "end": v(-1137.41, 339.83) * mm});
            skLineSegment(sketch, "E278.MirrorCS", {"start": v(-1129.8, 326.63) * mm, "end": v(-1132.54, 325.04) * mm});
            skLineSegment(sketch, "E279.MirrorCS", {"start": v(-1151.38, 364.03) * mm, "end": v(-1154.13, 362.44) * mm});
            skLineSegment(sketch, "E280.MirrorCS", {"start": v(-1146.51, 349.24) * mm, "end": v(-1143.76, 350.83) * mm});
            skLineSegment(sketch, "E281.MirrorCS", {"start": v(-1156.59, 365.42) * mm, "end": v(-1152.74, 367.64) * mm});
            skLineSegment(sketch, "E282.MirrorCS", {"start": v(-1147.78, 351.44) * mm, "end": v(-1145.03, 353.03) * mm});
            skLineSegment(sketch, "E283.MirrorCS", {"start": v(-1138.9, 336.04) * mm, "end": v(-1136.14, 337.63) * mm});
            skLineSegment(sketch, "E284.MirrorCS", {"start": v(-1127.34, 319.2) * mm, "end": v(-1127.34, 323.65) * mm});
            skLineSegment(sketch, "E285", {"start": v(-1236.64, 323.65) * mm, "end": v(-1236.64, 319.2) * mm});
            skLineSegment(sketch, "E286", {"start": v(-1207.39, 369.87) * mm, "end": v(-1211.24, 367.64) * mm});
            skLineSegment(sketch, "E287.0", {"start": v(-1135.5, 321.28) * mm, "end": v(-1158.86, 281.09) * mm});
            skLineSegment(sketch, "E287.1", {"start": v(-1158.86, 281.09) * mm, "end": v(-1205.36, 281.23) * mm});
            skLineSegment(sketch, "E287.2", {"start": v(-1205.36, 281.23) * mm, "end": v(-1228.49, 321.57) * mm});
            skLineSegment(sketch, "E287.3", {"start": v(-1228.49, 321.57) * mm, "end": v(-1205.11, 361.76) * mm});
            skLineSegment(sketch, "E287.4", {"start": v(-1205.11, 361.76) * mm, "end": v(-1158.62, 361.62) * mm});
            skLineSegment(sketch, "E287.5", {"start": v(-1158.62, 361.62) * mm, "end": v(-1135.5, 321.28) * mm});
            skPoint(sketch, "E287.0.midPoint", {"position": v(-1147.18, 301.19) * mm});
            skLineSegment(sketch, "E288", {"start": v(-1207.39, 457.85) * mm, "end": v(-1156.59, 457.85) * mm});
            skLineSegment(sketch, "E289", {"start": v(-1207.39, 462.3) * mm, "end": v(-1207.39, 457.85) * mm});
            skLineSegment(sketch, "E290", {"start": v(-1156.59, 462.3) * mm, "end": v(-1156.59, 457.85) * mm});
            skPoint(sketch, "E291.endSnap0", {"position": v(-1156.59, 460.08) * mm});
            skLineSegment(sketch, "E292", {"start": v(-1207.39, 460.08) * mm, "end": v(-1156.59, 460.08) * mm, "construction": true});
            skLineSegment(sketch, "E293", {"start": v(-1207.39, 462.3) * mm, "end": v(-1156.59, 462.3) * mm});
            skLineSegment(sketch, "E294", {"start": v(-1236.64, 416.08) * mm, "end": v(-1232.79, 413.86) * mm});
            skLineSegment(sketch, "E295.left", {"start": v(-1160.4, 458.49) * mm, "end": v(-1160.4, 461.66) * mm});
            skLineSegment(sketch, "E295.right", {"start": v(-1203.58, 458.49) * mm, "end": v(-1203.58, 461.66) * mm});
            skPoint(sketch, "E295.middle", {"position": v(-1181.99, 460.08) * mm});
            skLineSegment(sketch, "E296", {"start": v(-1181.99, 461.66) * mm, "end": v(-1181.99, 458.49) * mm, "construction": true});
            skLineSegment(sketch, "E297", {"start": v(-1190.88, 461.66) * mm, "end": v(-1190.88, 458.49) * mm});
            skLineSegment(sketch, "E298.MirrorCS", {"start": v(-1173.1, 461.66) * mm, "end": v(-1173.1, 458.49) * mm});
            skLineSegment(sketch, "E299", {"start": v(-1188.34, 461.66) * mm, "end": v(-1188.34, 458.49) * mm});
            skLineSegment(sketch, "E300.MirrorCS", {"start": v(-1175.64, 461.66) * mm, "end": v(-1175.64, 458.49) * mm});
            skLineSegment(sketch, "E301", {"start": v(-1203.58, 461.66) * mm, "end": v(-1190.88, 461.66) * mm});
            skLineSegment(sketch, "E302", {"start": v(-1203.58, 458.49) * mm, "end": v(-1190.88, 458.49) * mm});
            skLineSegment(sketch, "E303", {"start": v(-1188.34, 458.49) * mm, "end": v(-1181.99, 458.49) * mm});
            skLineSegment(sketch, "E304", {"start": v(-1188.34, 461.66) * mm, "end": v(-1181.99, 461.66) * mm});
            skLineSegment(sketch, "E305", {"start": v(-1181.99, 461.66) * mm, "end": v(-1175.64, 461.66) * mm});
            skLineSegment(sketch, "E306", {"start": v(-1181.99, 458.49) * mm, "end": v(-1175.64, 458.49) * mm});
            skLineSegment(sketch, "E307", {"start": v(-1173.1, 461.66) * mm, "end": v(-1160.4, 461.66) * mm});
            skLineSegment(sketch, "E308", {"start": v(-1173.1, 458.49) * mm, "end": v(-1160.4, 458.49) * mm});
            skLineSegment(sketch, "E309", {"start": v(-1156.59, 457.85) * mm, "end": v(-1131.19, 413.86) * mm});
            skLineSegment(sketch, "E310", {"start": v(-1152.74, 460.08) * mm, "end": v(-1156.59, 457.85) * mm});
            skLineSegment(sketch, "E311", {"start": v(-1152.74, 460.08) * mm, "end": v(-1127.34, 416.08) * mm});
            skLineSegment(sketch, "E312.left", {"start": v(-1132.54, 417.48) * mm, "end": v(-1129.8, 419.06) * mm});
            skLineSegment(sketch, "E312.right", {"start": v(-1154.13, 454.87) * mm, "end": v(-1151.38, 456.46) * mm});
            skPoint(sketch, "E312.middle", {"position": v(-1141.96, 436.97) * mm});
            skLineSegment(sketch, "E313", {"start": v(-1140.59, 437.76) * mm, "end": v(-1143.34, 436.17) * mm, "construction": true});
            skLineSegment(sketch, "E314", {"start": v(-1145.03, 445.46) * mm, "end": v(-1147.78, 443.87) * mm});
            skLineSegment(sketch, "E315.MirrorCS", {"start": v(-1136.14, 430.06) * mm, "end": v(-1138.9, 428.48) * mm});
            skLineSegment(sketch, "E316", {"start": v(-1143.76, 443.26) * mm, "end": v(-1146.51, 441.67) * mm});
            skLineSegment(sketch, "E317.MirrorCS", {"start": v(-1137.41, 432.26) * mm, "end": v(-1140.16, 430.68) * mm});
            skLineSegment(sketch, "E318", {"start": v(-1151.38, 456.46) * mm, "end": v(-1145.03, 445.46) * mm});
            skLineSegment(sketch, "E319", {"start": v(-1154.13, 454.87) * mm, "end": v(-1147.78, 443.87) * mm});
            skLineSegment(sketch, "E320", {"start": v(-1146.51, 441.67) * mm, "end": v(-1143.34, 436.17) * mm});
            skLineSegment(sketch, "E321", {"start": v(-1143.76, 443.26) * mm, "end": v(-1140.59, 437.76) * mm});
            skLineSegment(sketch, "E322", {"start": v(-1140.59, 437.76) * mm, "end": v(-1137.41, 432.26) * mm});
            skLineSegment(sketch, "E323", {"start": v(-1143.34, 436.17) * mm, "end": v(-1140.16, 430.68) * mm});
            skLineSegment(sketch, "E324", {"start": v(-1136.14, 430.06) * mm, "end": v(-1129.8, 419.06) * mm});
            skLineSegment(sketch, "E325", {"start": v(-1138.9, 428.48) * mm, "end": v(-1132.54, 417.48) * mm});
            skLineSegment(sketch, "E326", {"start": v(-1232.79, 413.86) * mm, "end": v(-1207.39, 457.85) * mm});
            skLineSegment(sketch, "E327", {"start": v(-1211.24, 460.08) * mm, "end": v(-1207.39, 457.85) * mm});
            skPoint(sketch, "E328.endSnap0", {"position": v(-1209.31, 458.97) * mm});
            skLineSegment(sketch, "E329", {"start": v(-1236.64, 416.08) * mm, "end": v(-1211.24, 460.08) * mm});
            skLineSegment(sketch, "E330.left", {"start": v(-1209.84, 454.87) * mm, "end": v(-1212.6, 456.46) * mm});
            skLineSegment(sketch, "E330.right", {"start": v(-1231.43, 417.48) * mm, "end": v(-1234.18, 419.06) * mm});
            skPoint(sketch, "E330.middle", {"position": v(-1222.01, 436.97) * mm});
            skLineSegment(sketch, "E331", {"start": v(-1223.39, 437.76) * mm, "end": v(-1220.64, 436.17) * mm, "construction": true});
            skLineSegment(sketch, "E332", {"start": v(-1227.83, 430.06) * mm, "end": v(-1225.08, 428.48) * mm});
            skLineSegment(sketch, "E333.MirrorCS", {"start": v(-1218.94, 445.46) * mm, "end": v(-1216.2, 443.87) * mm});
            skLineSegment(sketch, "E334", {"start": v(-1226.56, 432.26) * mm, "end": v(-1223.81, 430.68) * mm});
            skLineSegment(sketch, "E335.MirrorCS", {"start": v(-1220.21, 443.26) * mm, "end": v(-1217.46, 441.67) * mm});
            skLineSegment(sketch, "E336", {"start": v(-1234.18, 419.06) * mm, "end": v(-1227.83, 430.06) * mm});
            skLineSegment(sketch, "E337", {"start": v(-1231.43, 417.48) * mm, "end": v(-1225.08, 428.48) * mm});
            skLineSegment(sketch, "E338", {"start": v(-1223.81, 430.68) * mm, "end": v(-1220.64, 436.17) * mm});
            skLineSegment(sketch, "E339", {"start": v(-1226.56, 432.26) * mm, "end": v(-1223.39, 437.76) * mm});
            skLineSegment(sketch, "E340", {"start": v(-1223.39, 437.76) * mm, "end": v(-1220.21, 443.26) * mm});
            skLineSegment(sketch, "E341", {"start": v(-1220.64, 436.17) * mm, "end": v(-1217.46, 441.67) * mm});
            skLineSegment(sketch, "E342", {"start": v(-1218.94, 445.46) * mm, "end": v(-1212.6, 456.46) * mm});
            skLineSegment(sketch, "E343", {"start": v(-1216.2, 443.87) * mm, "end": v(-1209.84, 454.87) * mm});
            skLineSegment(sketch, "E344.0", {"start": v(-1207.39, 457.85) * mm, "end": v(-1211.24, 460.08) * mm, "construction": true});
            skLineSegment(sketch, "E345", {"start": v(-1131.19, 413.86) * mm, "end": v(-1127.34, 416.08) * mm});
            skLineSegment(sketch, "E346.MirrorCS", {"start": v(-1211.24, 367.64) * mm, "end": v(-1207.39, 369.87) * mm});
            skLineSegment(sketch, "E347.MirrorCS", {"start": v(-1140.59, 389.96) * mm, "end": v(-1143.34, 391.55) * mm, "construction": true});
            skLineSegment(sketch, "E348.MirrorCS", {"start": v(-1223.39, 389.96) * mm, "end": v(-1220.64, 391.55) * mm, "construction": true});
            skLineSegment(sketch, "E349.MirrorCS", {"start": v(-1181.99, 366.06) * mm, "end": v(-1181.99, 369.23) * mm, "construction": true});
            skLineSegment(sketch, "E350.MirrorCS", {"start": v(-1207.39, 369.87) * mm, "end": v(-1211.24, 367.64) * mm, "construction": true});
            skLineSegment(sketch, "E351.MirrorCS", {"start": v(-1152.74, 367.64) * mm, "end": v(-1156.59, 369.87) * mm});
            skLineSegment(sketch, "E352.MirrorCS", {"start": v(-1154.13, 372.85) * mm, "end": v(-1151.38, 371.26) * mm});
            skLineSegment(sketch, "E353.MirrorCS", {"start": v(-1220.21, 384.46) * mm, "end": v(-1217.46, 386.05) * mm});
            skLineSegment(sketch, "E354.MirrorCS", {"start": v(-1175.64, 366.06) * mm, "end": v(-1175.64, 369.23) * mm});
            skLineSegment(sketch, "E355.MirrorCS", {"start": v(-1156.59, 365.42) * mm, "end": v(-1156.59, 369.87) * mm});
            skLineSegment(sketch, "E356.MirrorCS", {"start": v(-1190.88, 366.06) * mm, "end": v(-1190.88, 369.23) * mm});
            skLineSegment(sketch, "E357.MirrorCS", {"start": v(-1145.03, 382.26) * mm, "end": v(-1147.78, 383.85) * mm});
            skLineSegment(sketch, "E358.MirrorCS", {"start": v(-1188.34, 366.06) * mm, "end": v(-1188.34, 369.23) * mm});
            skLineSegment(sketch, "E359.MirrorCS", {"start": v(-1209.84, 372.85) * mm, "end": v(-1212.6, 371.26) * mm});
            skLineSegment(sketch, "E360.MirrorCS", {"start": v(-1231.43, 410.24) * mm, "end": v(-1234.18, 408.66) * mm});
            skLineSegment(sketch, "E361.MirrorCS", {"start": v(-1226.56, 395.46) * mm, "end": v(-1223.81, 397.04) * mm});
            skLineSegment(sketch, "E362.MirrorCS", {"start": v(-1236.64, 411.64) * mm, "end": v(-1232.79, 413.86) * mm});
            skLineSegment(sketch, "E363.MirrorCS", {"start": v(-1143.76, 384.46) * mm, "end": v(-1146.51, 386.05) * mm});
            skLineSegment(sketch, "E364.MirrorCS", {"start": v(-1173.1, 366.06) * mm, "end": v(-1173.1, 369.23) * mm});
            skLineSegment(sketch, "E365.MirrorCS", {"start": v(-1227.83, 397.66) * mm, "end": v(-1225.08, 399.24) * mm});
            skLineSegment(sketch, "E366.MirrorCS", {"start": v(-1132.54, 410.24) * mm, "end": v(-1129.8, 408.66) * mm});
            skLineSegment(sketch, "E367.MirrorCS", {"start": v(-1203.58, 369.23) * mm, "end": v(-1203.58, 366.06) * mm});
            skLineSegment(sketch, "E368.MirrorCS", {"start": v(-1136.14, 397.66) * mm, "end": v(-1138.9, 399.24) * mm});
            skLineSegment(sketch, "E369.MirrorCS", {"start": v(-1131.19, 413.86) * mm, "end": v(-1127.34, 411.64) * mm});
            skLineSegment(sketch, "E370.MirrorCS", {"start": v(-1137.41, 395.46) * mm, "end": v(-1140.16, 397.04) * mm});
            skLineSegment(sketch, "E371.MirrorCS", {"start": v(-1218.94, 382.26) * mm, "end": v(-1216.2, 383.85) * mm});
            skLineSegment(sketch, "E372.MirrorCS", {"start": v(-1160.4, 369.23) * mm, "end": v(-1160.4, 366.06) * mm});
            skLineSegment(sketch, "E373.MirrorCS", {"start": v(-1146.51, 386.05) * mm, "end": v(-1143.34, 391.55) * mm});
            skLineSegment(sketch, "E374.MirrorCS", {"start": v(-1223.81, 397.04) * mm, "end": v(-1220.64, 391.55) * mm});
            skLineSegment(sketch, "E375.MirrorCS", {"start": v(-1140.59, 389.96) * mm, "end": v(-1137.41, 395.46) * mm});
            skLineSegment(sketch, "E376.MirrorCS", {"start": v(-1207.39, 365.42) * mm, "end": v(-1207.39, 369.87) * mm});
            skLineSegment(sketch, "E377.MirrorCS", {"start": v(-1143.34, 391.55) * mm, "end": v(-1140.16, 397.04) * mm});
            skLineSegment(sketch, "E378.MirrorCS", {"start": v(-1143.76, 384.46) * mm, "end": v(-1140.59, 389.96) * mm});
            skLineSegment(sketch, "E379.MirrorCS", {"start": v(-1220.64, 391.55) * mm, "end": v(-1217.46, 386.05) * mm});
            skLineSegment(sketch, "E380.MirrorCS", {"start": v(-1138.9, 399.24) * mm, "end": v(-1132.54, 410.24) * mm});
            skLineSegment(sketch, "E381.MirrorCS", {"start": v(-1236.64, 411.64) * mm, "end": v(-1211.24, 367.64) * mm});
            skLineSegment(sketch, "E382.MirrorCS", {"start": v(-1156.59, 369.87) * mm, "end": v(-1131.19, 413.86) * mm});
            skLineSegment(sketch, "E383.MirrorCS", {"start": v(-1151.38, 371.26) * mm, "end": v(-1145.03, 382.26) * mm});
            skLineSegment(sketch, "E384.MirrorCS", {"start": v(-1231.43, 410.24) * mm, "end": v(-1225.08, 399.24) * mm});
            skLineSegment(sketch, "E385.MirrorCS", {"start": v(-1216.2, 383.85) * mm, "end": v(-1209.84, 372.85) * mm});
            skPoint(sketch, "E386.MirrorP", {"position": v(-1141.96, 390.75) * mm});
            skLineSegment(sketch, "E387.MirrorCS", {"start": v(-1136.14, 397.66) * mm, "end": v(-1129.8, 408.66) * mm});
            skPoint(sketch, "E388.MirrorP", {"position": v(-1209.31, 368.75) * mm});
            skLineSegment(sketch, "E389.MirrorCS", {"start": v(-1226.56, 395.46) * mm, "end": v(-1223.39, 389.96) * mm});
            skPoint(sketch, "E390.MirrorP", {"position": v(-1222.01, 390.75) * mm});
            skLineSegment(sketch, "E391.MirrorCS", {"start": v(-1154.13, 372.85) * mm, "end": v(-1147.78, 383.85) * mm});
            skLineSegment(sketch, "E392.MirrorCS", {"start": v(-1152.74, 367.64) * mm, "end": v(-1127.34, 411.64) * mm});
            skLineSegment(sketch, "E393.MirrorCS", {"start": v(-1232.79, 413.86) * mm, "end": v(-1207.39, 369.87) * mm});
            skLineSegment(sketch, "E394.MirrorCS", {"start": v(-1218.94, 382.26) * mm, "end": v(-1212.6, 371.26) * mm});
            skLineSegment(sketch, "E395.MirrorCS", {"start": v(-1234.18, 408.66) * mm, "end": v(-1227.83, 397.66) * mm});
            skLineSegment(sketch, "E396.MirrorCS", {"start": v(-1223.39, 389.96) * mm, "end": v(-1220.21, 384.46) * mm});
            skLineSegment(sketch, "E397", {"start": v(-1127.34, 416.08) * mm, "end": v(-1127.34, 411.64) * mm});
            skLineSegment(sketch, "E398.left", {"start": v(-1129.8, 408.66) * mm, "end": v(-1132.54, 410.24) * mm});
            skLineSegment(sketch, "E398.right", {"start": v(-1151.38, 371.26) * mm, "end": v(-1154.13, 372.85) * mm});
            skLineSegment(sketch, "E399", {"start": v(-1143.34, 391.55) * mm, "end": v(-1140.59, 389.96) * mm, "construction": true});
            skLineSegment(sketch, "E400", {"start": v(-1147.78, 383.85) * mm, "end": v(-1145.03, 382.26) * mm});
            skLineSegment(sketch, "E401.MirrorCS", {"start": v(-1138.9, 399.24) * mm, "end": v(-1136.14, 397.66) * mm});
            skLineSegment(sketch, "E402", {"start": v(-1146.51, 386.05) * mm, "end": v(-1143.76, 384.46) * mm});
            skLineSegment(sketch, "E403.MirrorCS", {"start": v(-1140.16, 397.04) * mm, "end": v(-1137.41, 395.46) * mm});
            skLineSegment(sketch, "E404.0", {"start": v(-1127.34, 411.64) * mm, "end": v(-1131.19, 413.86) * mm, "construction": true});
            skLineSegment(sketch, "E405", {"start": v(-1156.59, 462.3) * mm, "end": v(-1152.74, 460.08) * mm});
            skLineSegment(sketch, "E406.MirrorCS", {"start": v(-1143.34, 436.17) * mm, "end": v(-1140.59, 437.76) * mm, "construction": true});
            skLineSegment(sketch, "E407.MirrorCS", {"start": v(-1127.34, 416.08) * mm, "end": v(-1131.19, 413.86) * mm, "construction": true});
            skLineSegment(sketch, "E408.MirrorCS", {"start": v(-1140.16, 430.68) * mm, "end": v(-1137.41, 432.26) * mm});
            skLineSegment(sketch, "E409.MirrorCS", {"start": v(-1129.8, 419.06) * mm, "end": v(-1132.54, 417.48) * mm});
            skLineSegment(sketch, "E410.MirrorCS", {"start": v(-1151.38, 456.46) * mm, "end": v(-1154.13, 454.87) * mm});
            skLineSegment(sketch, "E411.MirrorCS", {"start": v(-1146.51, 441.67) * mm, "end": v(-1143.76, 443.26) * mm});
            skLineSegment(sketch, "E412.MirrorCS", {"start": v(-1156.59, 457.85) * mm, "end": v(-1152.74, 460.08) * mm});
            skLineSegment(sketch, "E413.MirrorCS", {"start": v(-1147.78, 443.87) * mm, "end": v(-1145.03, 445.46) * mm});
            skLineSegment(sketch, "E414.MirrorCS", {"start": v(-1138.9, 428.48) * mm, "end": v(-1136.14, 430.06) * mm});
            skLineSegment(sketch, "E415.MirrorCS", {"start": v(-1127.34, 411.64) * mm, "end": v(-1127.34, 416.08) * mm});
            skLineSegment(sketch, "E416", {"start": v(-1236.64, 416.08) * mm, "end": v(-1236.64, 411.64) * mm});
            skLineSegment(sketch, "E417", {"start": v(-1207.39, 462.3) * mm, "end": v(-1211.24, 460.08) * mm});
            skLineSegment(sketch, "E418.0", {"start": v(-1135.5, 413.72) * mm, "end": v(-1158.86, 373.52) * mm});
            skLineSegment(sketch, "E418.1", {"start": v(-1158.86, 373.52) * mm, "end": v(-1205.36, 373.66) * mm});
            skLineSegment(sketch, "E418.2", {"start": v(-1205.36, 373.66) * mm, "end": v(-1228.49, 414) * mm});
            skLineSegment(sketch, "E418.3", {"start": v(-1228.49, 414) * mm, "end": v(-1205.11, 454.2) * mm});
            skLineSegment(sketch, "E418.4", {"start": v(-1205.11, 454.2) * mm, "end": v(-1158.62, 454.06) * mm});
            skLineSegment(sketch, "E418.5", {"start": v(-1158.62, 454.06) * mm, "end": v(-1135.5, 413.72) * mm});
            skPoint(sketch, "E418.0.midPoint", {"position": v(-1147.18, 393.62) * mm});
            skLineSegment(sketch, "E419", {"start": v(-1127.34, 226.77) * mm, "end": v(-1076.54, 226.77) * mm});
            skLineSegment(sketch, "E420", {"start": v(-1076.54, 231.22) * mm, "end": v(-1076.54, 226.77) * mm});
            skPoint(sketch, "E421.endSnap0", {"position": v(-1076.54, 229) * mm});
            skLineSegment(sketch, "E422", {"start": v(-1127.34, 229) * mm, "end": v(-1076.54, 229) * mm, "construction": true});
            skLineSegment(sketch, "E423", {"start": v(-1127.34, 231.22) * mm, "end": v(-1076.54, 231.22) * mm});
            skLineSegment(sketch, "E424.left", {"start": v(-1080.35, 227.4) * mm, "end": v(-1080.35, 230.58) * mm});
            skLineSegment(sketch, "E424.right", {"start": v(-1123.53, 227.4) * mm, "end": v(-1123.53, 230.58) * mm});
            skPoint(sketch, "E424.middle", {"position": v(-1101.94, 229) * mm});
            skLineSegment(sketch, "E425", {"start": v(-1101.94, 230.58) * mm, "end": v(-1101.94, 227.4) * mm, "construction": true});
            skLineSegment(sketch, "E426", {"start": v(-1110.83, 230.58) * mm, "end": v(-1110.83, 227.4) * mm});
            skLineSegment(sketch, "E427.MirrorCS", {"start": v(-1093.05, 230.58) * mm, "end": v(-1093.05, 227.4) * mm});
            skLineSegment(sketch, "E428", {"start": v(-1108.29, 230.58) * mm, "end": v(-1108.29, 227.4) * mm});
            skLineSegment(sketch, "E429.MirrorCS", {"start": v(-1095.59, 230.58) * mm, "end": v(-1095.59, 227.4) * mm});
            skLineSegment(sketch, "E430", {"start": v(-1123.53, 230.58) * mm, "end": v(-1110.83, 230.58) * mm});
            skLineSegment(sketch, "E431", {"start": v(-1123.53, 227.4) * mm, "end": v(-1110.83, 227.4) * mm});
            skLineSegment(sketch, "E432", {"start": v(-1108.29, 227.4) * mm, "end": v(-1101.94, 227.4) * mm});
            skLineSegment(sketch, "E433", {"start": v(-1108.29, 230.58) * mm, "end": v(-1101.94, 230.58) * mm});
            skLineSegment(sketch, "E434", {"start": v(-1101.94, 230.58) * mm, "end": v(-1095.59, 230.58) * mm});
            skLineSegment(sketch, "E435", {"start": v(-1101.94, 227.4) * mm, "end": v(-1095.59, 227.4) * mm});
            skLineSegment(sketch, "E436", {"start": v(-1093.05, 230.58) * mm, "end": v(-1080.35, 230.58) * mm});
            skLineSegment(sketch, "E437", {"start": v(-1093.05, 227.4) * mm, "end": v(-1080.35, 227.4) * mm});
            skLineSegment(sketch, "E438", {"start": v(-1072.69, 229) * mm, "end": v(-1076.54, 226.77) * mm});
            skPoint(sketch, "E439.endSnap0", {"position": v(-1129.26, 227.88) * mm});
            skLineSegment(sketch, "E440", {"start": v(-1127.34, 319.2) * mm, "end": v(-1076.54, 319.2) * mm});
            skLineSegment(sketch, "E441", {"start": v(-1076.54, 323.65) * mm, "end": v(-1076.54, 319.2) * mm});
            skPoint(sketch, "E442.endSnap0", {"position": v(-1076.54, 321.43) * mm});
            skLineSegment(sketch, "E443", {"start": v(-1127.34, 321.43) * mm, "end": v(-1076.54, 321.43) * mm, "construction": true});
            skLineSegment(sketch, "E444", {"start": v(-1127.34, 323.65) * mm, "end": v(-1076.54, 323.65) * mm});
            skLineSegment(sketch, "E445.left", {"start": v(-1080.35, 319.84) * mm, "end": v(-1080.35, 323.01) * mm});
            skLineSegment(sketch, "E445.right", {"start": v(-1123.53, 319.84) * mm, "end": v(-1123.53, 323.01) * mm});
            skPoint(sketch, "E445.middle", {"position": v(-1101.94, 321.43) * mm});
            skLineSegment(sketch, "E446", {"start": v(-1101.94, 323.01) * mm, "end": v(-1101.94, 319.84) * mm, "construction": true});
            skLineSegment(sketch, "E447", {"start": v(-1110.83, 323.01) * mm, "end": v(-1110.83, 319.84) * mm});
            skLineSegment(sketch, "E448.MirrorCS", {"start": v(-1093.05, 323.01) * mm, "end": v(-1093.05, 319.84) * mm});
            skLineSegment(sketch, "E449", {"start": v(-1108.29, 323.01) * mm, "end": v(-1108.29, 319.84) * mm});
            skLineSegment(sketch, "E450.MirrorCS", {"start": v(-1095.59, 323.01) * mm, "end": v(-1095.59, 319.84) * mm});
            skLineSegment(sketch, "E451", {"start": v(-1123.53, 323.01) * mm, "end": v(-1110.83, 323.01) * mm});
            skLineSegment(sketch, "E452", {"start": v(-1123.53, 319.84) * mm, "end": v(-1110.83, 319.84) * mm});
            skLineSegment(sketch, "E453", {"start": v(-1108.29, 319.84) * mm, "end": v(-1101.94, 319.84) * mm});
            skLineSegment(sketch, "E454", {"start": v(-1108.29, 323.01) * mm, "end": v(-1101.94, 323.01) * mm});
            skLineSegment(sketch, "E455", {"start": v(-1101.94, 323.01) * mm, "end": v(-1095.59, 323.01) * mm});
            skLineSegment(sketch, "E456", {"start": v(-1101.94, 319.84) * mm, "end": v(-1095.59, 319.84) * mm});
            skLineSegment(sketch, "E457", {"start": v(-1093.05, 323.01) * mm, "end": v(-1080.35, 323.01) * mm});
            skLineSegment(sketch, "E458", {"start": v(-1093.05, 319.84) * mm, "end": v(-1080.35, 319.84) * mm});
            skLineSegment(sketch, "E459", {"start": v(-1076.54, 319.2) * mm, "end": v(-1051.14, 275.21) * mm});
            skLineSegment(sketch, "E460", {"start": v(-1072.69, 321.43) * mm, "end": v(-1076.54, 319.2) * mm});
            skLineSegment(sketch, "E461", {"start": v(-1072.69, 321.43) * mm, "end": v(-1047.29, 277.43) * mm});
            skLineSegment(sketch, "E462.left", {"start": v(-1052.5, 278.83) * mm, "end": v(-1049.74, 280.41) * mm});
            skLineSegment(sketch, "E462.right", {"start": v(-1074.08, 316.22) * mm, "end": v(-1071.33, 317.8) * mm});
            skPoint(sketch, "E462.middle", {"position": v(-1061.91, 298.32) * mm});
            skLineSegment(sketch, "E463", {"start": v(-1060.54, 299.11) * mm, "end": v(-1063.29, 297.52) * mm, "construction": true});
            skLineSegment(sketch, "E464", {"start": v(-1064.98, 306.81) * mm, "end": v(-1067.73, 305.22) * mm});
            skLineSegment(sketch, "E465.MirrorCS", {"start": v(-1056.1, 291.41) * mm, "end": v(-1058.84, 289.83) * mm});
            skLineSegment(sketch, "E466", {"start": v(-1063.71, 304.61) * mm, "end": v(-1066.46, 303.02) * mm});
            skLineSegment(sketch, "E467.MirrorCS", {"start": v(-1057.36, 293.61) * mm, "end": v(-1060.11, 292.03) * mm});
            skLineSegment(sketch, "E468", {"start": v(-1071.33, 317.8) * mm, "end": v(-1064.98, 306.81) * mm});
            skLineSegment(sketch, "E469", {"start": v(-1074.08, 316.22) * mm, "end": v(-1067.73, 305.22) * mm});
            skLineSegment(sketch, "E470", {"start": v(-1066.46, 303.02) * mm, "end": v(-1063.29, 297.52) * mm});
            skLineSegment(sketch, "E471", {"start": v(-1063.71, 304.61) * mm, "end": v(-1060.54, 299.11) * mm});
            skLineSegment(sketch, "E472", {"start": v(-1060.54, 299.11) * mm, "end": v(-1057.36, 293.61) * mm});
            skLineSegment(sketch, "E473", {"start": v(-1063.29, 297.52) * mm, "end": v(-1060.11, 292.03) * mm});
            skLineSegment(sketch, "E474", {"start": v(-1056.1, 291.41) * mm, "end": v(-1049.74, 280.41) * mm});
            skLineSegment(sketch, "E475", {"start": v(-1058.84, 289.83) * mm, "end": v(-1052.5, 278.83) * mm});
            skPoint(sketch, "E476.endSnap0", {"position": v(-1129.26, 320.32) * mm});
            skLineSegment(sketch, "E477", {"start": v(-1051.14, 275.21) * mm, "end": v(-1047.29, 277.43) * mm});
            skLineSegment(sketch, "E478.MirrorCS", {"start": v(-1060.54, 251.3) * mm, "end": v(-1063.29, 252.9) * mm, "construction": true});
            skLineSegment(sketch, "E479.MirrorCS", {"start": v(-1101.94, 227.4) * mm, "end": v(-1101.94, 230.58) * mm, "construction": true});
            skLineSegment(sketch, "E480.MirrorCS", {"start": v(-1072.69, 229) * mm, "end": v(-1076.54, 231.22) * mm});
            skLineSegment(sketch, "E481.MirrorCS", {"start": v(-1074.08, 234.2) * mm, "end": v(-1071.33, 232.61) * mm});
            skLineSegment(sketch, "E482.MirrorCS", {"start": v(-1095.59, 227.4) * mm, "end": v(-1095.59, 230.58) * mm});
            skLineSegment(sketch, "E483.MirrorCS", {"start": v(-1076.54, 226.77) * mm, "end": v(-1076.54, 231.22) * mm});
            skLineSegment(sketch, "E484.MirrorCS", {"start": v(-1110.83, 227.4) * mm, "end": v(-1110.83, 230.58) * mm});
            skLineSegment(sketch, "E485.MirrorCS", {"start": v(-1064.98, 243.6) * mm, "end": v(-1067.73, 245.2) * mm});
            skLineSegment(sketch, "E486.MirrorCS", {"start": v(-1108.29, 227.4) * mm, "end": v(-1108.29, 230.58) * mm});
            skLineSegment(sketch, "E487.MirrorCS", {"start": v(-1063.71, 245.8) * mm, "end": v(-1066.46, 247.4) * mm});
            skLineSegment(sketch, "E488.MirrorCS", {"start": v(-1093.05, 227.4) * mm, "end": v(-1093.05, 230.58) * mm});
            skLineSegment(sketch, "E489.MirrorCS", {"start": v(-1052.5, 271.6) * mm, "end": v(-1049.74, 270) * mm});
            skLineSegment(sketch, "E490.MirrorCS", {"start": v(-1123.53, 230.58) * mm, "end": v(-1123.53, 227.4) * mm});
            skLineSegment(sketch, "E491.MirrorCS", {"start": v(-1056.1, 259) * mm, "end": v(-1058.84, 260.6) * mm});
            skLineSegment(sketch, "E492.MirrorCS", {"start": v(-1051.14, 275.21) * mm, "end": v(-1047.29, 272.99) * mm});
            skLineSegment(sketch, "E493.MirrorCS", {"start": v(-1057.36, 256.8) * mm, "end": v(-1060.11, 258.4) * mm});
            skLineSegment(sketch, "E494.MirrorCS", {"start": v(-1080.35, 230.58) * mm, "end": v(-1080.35, 227.4) * mm});
            skLineSegment(sketch, "E495.MirrorCS", {"start": v(-1066.46, 247.4) * mm, "end": v(-1063.29, 252.9) * mm});
            skLineSegment(sketch, "E496.MirrorCS", {"start": v(-1060.54, 251.3) * mm, "end": v(-1057.36, 256.8) * mm});
            skLineSegment(sketch, "E497.MirrorCS", {"start": v(-1063.29, 252.9) * mm, "end": v(-1060.11, 258.4) * mm});
            skLineSegment(sketch, "E498.MirrorCS", {"start": v(-1063.71, 245.8) * mm, "end": v(-1060.54, 251.3) * mm});
            skLineSegment(sketch, "E499.MirrorCS", {"start": v(-1058.84, 260.6) * mm, "end": v(-1052.5, 271.6) * mm});
            skLineSegment(sketch, "E500.MirrorCS", {"start": v(-1076.54, 231.22) * mm, "end": v(-1051.14, 275.21) * mm});
            skLineSegment(sketch, "E501.MirrorCS", {"start": v(-1071.33, 232.61) * mm, "end": v(-1064.98, 243.6) * mm});
            skPoint(sketch, "E502.MirrorP", {"position": v(-1061.91, 252.1) * mm});
            skLineSegment(sketch, "E503.MirrorCS", {"start": v(-1056.1, 259) * mm, "end": v(-1049.74, 270) * mm});
            skPoint(sketch, "E504.MirrorP", {"position": v(-1129.26, 230.1) * mm});
            skLineSegment(sketch, "E505.MirrorCS", {"start": v(-1074.08, 234.2) * mm, "end": v(-1067.73, 245.2) * mm});
            skLineSegment(sketch, "E506.MirrorCS", {"start": v(-1072.69, 229) * mm, "end": v(-1047.29, 272.99) * mm});
            skLineSegment(sketch, "E507", {"start": v(-1047.29, 277.43) * mm, "end": v(-1047.29, 272.99) * mm});
            skLineSegment(sketch, "E508", {"start": v(-1076.54, 231.22) * mm, "end": v(-1072.69, 229) * mm});
            skLineSegment(sketch, "E509.left", {"start": v(-1049.74, 270) * mm, "end": v(-1052.5, 271.6) * mm});
            skLineSegment(sketch, "E509.right", {"start": v(-1071.33, 232.61) * mm, "end": v(-1074.08, 234.2) * mm});
            skLineSegment(sketch, "E510", {"start": v(-1063.29, 252.9) * mm, "end": v(-1060.54, 251.3) * mm, "construction": true});
            skLineSegment(sketch, "E511", {"start": v(-1067.73, 245.2) * mm, "end": v(-1064.98, 243.6) * mm});
            skLineSegment(sketch, "E512.MirrorCS", {"start": v(-1058.84, 260.6) * mm, "end": v(-1056.1, 259) * mm});
            skLineSegment(sketch, "E513", {"start": v(-1066.46, 247.4) * mm, "end": v(-1063.71, 245.8) * mm});
            skLineSegment(sketch, "E514.MirrorCS", {"start": v(-1060.11, 258.4) * mm, "end": v(-1057.36, 256.8) * mm});
            skLineSegment(sketch, "E515.0", {"start": v(-1047.29, 272.99) * mm, "end": v(-1051.14, 275.21) * mm, "construction": true});
            skLineSegment(sketch, "E516.MirrorCS", {"start": v(-1076.54, 226.77) * mm, "end": v(-1072.69, 229) * mm});
            skLineSegment(sketch, "E517", {"start": v(-1076.54, 323.65) * mm, "end": v(-1072.69, 321.43) * mm});
            skLineSegment(sketch, "E518.MirrorCS", {"start": v(-1063.29, 297.52) * mm, "end": v(-1060.54, 299.11) * mm, "construction": true});
            skLineSegment(sketch, "E519.MirrorCS", {"start": v(-1047.29, 277.43) * mm, "end": v(-1051.14, 275.21) * mm, "construction": true});
            skLineSegment(sketch, "E520.MirrorCS", {"start": v(-1060.11, 292.03) * mm, "end": v(-1057.36, 293.61) * mm});
            skLineSegment(sketch, "E521.MirrorCS", {"start": v(-1049.74, 280.41) * mm, "end": v(-1052.5, 278.83) * mm});
            skLineSegment(sketch, "E522.MirrorCS", {"start": v(-1071.33, 317.8) * mm, "end": v(-1074.08, 316.22) * mm});
            skLineSegment(sketch, "E523.MirrorCS", {"start": v(-1066.46, 303.02) * mm, "end": v(-1063.71, 304.61) * mm});
            skLineSegment(sketch, "E524.MirrorCS", {"start": v(-1076.54, 319.2) * mm, "end": v(-1072.69, 321.43) * mm});
            skLineSegment(sketch, "E525.MirrorCS", {"start": v(-1067.73, 305.22) * mm, "end": v(-1064.98, 306.81) * mm});
            skLineSegment(sketch, "E526.MirrorCS", {"start": v(-1058.84, 289.83) * mm, "end": v(-1056.1, 291.41) * mm});
            skLineSegment(sketch, "E527.MirrorCS", {"start": v(-1047.29, 272.99) * mm, "end": v(-1047.29, 277.43) * mm});
            skLineSegment(sketch, "E528", {"start": v(-1127.34, 323.65) * mm, "end": v(-1131.19, 321.43) * mm});
            skLineSegment(sketch, "E529.0", {"start": v(-1055.44, 275.07) * mm, "end": v(-1078.81, 234.87) * mm});
            skLineSegment(sketch, "E529.1", {"start": v(-1078.81, 234.87) * mm, "end": v(-1125.31, 235.01) * mm});
            skLineSegment(sketch, "E529.2", {"start": v(-1125.31, 235.01) * mm, "end": v(-1148.44, 275.35) * mm});
            skLineSegment(sketch, "E529.3", {"start": v(-1148.44, 275.35) * mm, "end": v(-1125.06, 315.55) * mm});
            skLineSegment(sketch, "E529.4", {"start": v(-1125.06, 315.55) * mm, "end": v(-1078.57, 315.4) * mm});
            skLineSegment(sketch, "E529.5", {"start": v(-1078.57, 315.4) * mm, "end": v(-1055.44, 275.07) * mm});
            skPoint(sketch, "E529.0.midPoint", {"position": v(-1067.13, 254.97) * mm});
            skLineSegment(sketch, "E530", {"start": v(-1127.34, 411.64) * mm, "end": v(-1076.54, 411.64) * mm});
            skLineSegment(sketch, "E531", {"start": v(-1076.54, 416.08) * mm, "end": v(-1076.54, 411.64) * mm});
            skPoint(sketch, "E532.endSnap0", {"position": v(-1076.54, 413.86) * mm});
            skLineSegment(sketch, "E533", {"start": v(-1127.34, 413.86) * mm, "end": v(-1076.54, 413.86) * mm, "construction": true});
            skLineSegment(sketch, "E534", {"start": v(-1127.34, 416.08) * mm, "end": v(-1076.54, 416.08) * mm});
            skLineSegment(sketch, "E535.left", {"start": v(-1080.35, 412.27) * mm, "end": v(-1080.35, 415.45) * mm});
            skLineSegment(sketch, "E535.right", {"start": v(-1123.53, 412.27) * mm, "end": v(-1123.53, 415.45) * mm});
            skPoint(sketch, "E535.middle", {"position": v(-1101.94, 413.86) * mm});
            skLineSegment(sketch, "E536", {"start": v(-1101.94, 415.45) * mm, "end": v(-1101.94, 412.27) * mm, "construction": true});
            skLineSegment(sketch, "E537", {"start": v(-1110.83, 415.45) * mm, "end": v(-1110.83, 412.27) * mm});
            skLineSegment(sketch, "E538.MirrorCS", {"start": v(-1093.05, 415.45) * mm, "end": v(-1093.05, 412.27) * mm});
            skLineSegment(sketch, "E539", {"start": v(-1108.29, 415.45) * mm, "end": v(-1108.29, 412.27) * mm});
            skLineSegment(sketch, "E540.MirrorCS", {"start": v(-1095.59, 415.45) * mm, "end": v(-1095.59, 412.27) * mm});
            skLineSegment(sketch, "E541", {"start": v(-1123.53, 415.45) * mm, "end": v(-1110.83, 415.45) * mm});
            skLineSegment(sketch, "E542", {"start": v(-1123.53, 412.27) * mm, "end": v(-1110.83, 412.27) * mm});
            skLineSegment(sketch, "E543", {"start": v(-1108.29, 412.27) * mm, "end": v(-1101.94, 412.27) * mm});
            skLineSegment(sketch, "E544", {"start": v(-1108.29, 415.45) * mm, "end": v(-1101.94, 415.45) * mm});
            skLineSegment(sketch, "E545", {"start": v(-1101.94, 415.45) * mm, "end": v(-1095.59, 415.45) * mm});
            skLineSegment(sketch, "E546", {"start": v(-1101.94, 412.27) * mm, "end": v(-1095.59, 412.27) * mm});
            skLineSegment(sketch, "E547", {"start": v(-1093.05, 415.45) * mm, "end": v(-1080.35, 415.45) * mm});
            skLineSegment(sketch, "E548", {"start": v(-1093.05, 412.27) * mm, "end": v(-1080.35, 412.27) * mm});
            skLineSegment(sketch, "E549", {"start": v(-1076.54, 411.64) * mm, "end": v(-1051.14, 367.64) * mm});
            skLineSegment(sketch, "E550", {"start": v(-1072.69, 413.86) * mm, "end": v(-1076.54, 411.64) * mm});
            skLineSegment(sketch, "E551", {"start": v(-1072.69, 413.86) * mm, "end": v(-1047.29, 369.87) * mm});
            skLineSegment(sketch, "E552.left", {"start": v(-1052.5, 371.26) * mm, "end": v(-1049.74, 372.85) * mm});
            skLineSegment(sketch, "E552.right", {"start": v(-1074.08, 408.66) * mm, "end": v(-1071.33, 410.24) * mm});
            skPoint(sketch, "E552.middle", {"position": v(-1061.91, 390.75) * mm});
            skLineSegment(sketch, "E553", {"start": v(-1060.54, 391.55) * mm, "end": v(-1063.29, 389.96) * mm, "construction": true});
            skLineSegment(sketch, "E554", {"start": v(-1064.98, 399.24) * mm, "end": v(-1067.73, 397.66) * mm});
            skLineSegment(sketch, "E555.MirrorCS", {"start": v(-1056.1, 383.85) * mm, "end": v(-1058.84, 382.26) * mm});
            skLineSegment(sketch, "E556", {"start": v(-1063.71, 397.04) * mm, "end": v(-1066.46, 395.46) * mm});
            skLineSegment(sketch, "E557.MirrorCS", {"start": v(-1057.36, 386.05) * mm, "end": v(-1060.11, 384.46) * mm});
            skLineSegment(sketch, "E558", {"start": v(-1071.33, 410.24) * mm, "end": v(-1064.98, 399.24) * mm});
            skLineSegment(sketch, "E559", {"start": v(-1074.08, 408.66) * mm, "end": v(-1067.73, 397.66) * mm});
            skLineSegment(sketch, "E560", {"start": v(-1066.46, 395.46) * mm, "end": v(-1063.29, 389.96) * mm});
            skLineSegment(sketch, "E561", {"start": v(-1063.71, 397.04) * mm, "end": v(-1060.54, 391.55) * mm});
            skLineSegment(sketch, "E562", {"start": v(-1060.54, 391.55) * mm, "end": v(-1057.36, 386.05) * mm});
            skLineSegment(sketch, "E563", {"start": v(-1063.29, 389.96) * mm, "end": v(-1060.11, 384.46) * mm});
            skLineSegment(sketch, "E564", {"start": v(-1056.1, 383.85) * mm, "end": v(-1049.74, 372.85) * mm});
            skLineSegment(sketch, "E565", {"start": v(-1058.84, 382.26) * mm, "end": v(-1052.5, 371.26) * mm});
            skPoint(sketch, "E566.endSnap0", {"position": v(-1129.26, 412.75) * mm});
            skLineSegment(sketch, "E567", {"start": v(-1051.14, 367.64) * mm, "end": v(-1047.29, 369.87) * mm});
            skLineSegment(sketch, "E568.MirrorCS", {"start": v(-1060.54, 343.74) * mm, "end": v(-1063.29, 345.33) * mm, "construction": true});
            skLineSegment(sketch, "E569.MirrorCS", {"start": v(-1101.94, 319.84) * mm, "end": v(-1101.94, 323.01) * mm, "construction": true});
            skLineSegment(sketch, "E570.MirrorCS", {"start": v(-1072.69, 321.43) * mm, "end": v(-1076.54, 323.65) * mm});
            skLineSegment(sketch, "E571.MirrorCS", {"start": v(-1074.08, 326.63) * mm, "end": v(-1071.33, 325.04) * mm});
            skLineSegment(sketch, "E572.MirrorCS", {"start": v(-1095.59, 319.84) * mm, "end": v(-1095.59, 323.01) * mm});
            skLineSegment(sketch, "E573.MirrorCS", {"start": v(-1076.54, 319.2) * mm, "end": v(-1076.54, 323.65) * mm});
            skLineSegment(sketch, "E574.MirrorCS", {"start": v(-1110.83, 319.84) * mm, "end": v(-1110.83, 323.01) * mm});
            skLineSegment(sketch, "E575.MirrorCS", {"start": v(-1064.98, 336.04) * mm, "end": v(-1067.73, 337.63) * mm});
            skLineSegment(sketch, "E576.MirrorCS", {"start": v(-1108.29, 319.84) * mm, "end": v(-1108.29, 323.01) * mm});
            skLineSegment(sketch, "E577.MirrorCS", {"start": v(-1063.71, 338.24) * mm, "end": v(-1066.46, 339.83) * mm});
            skLineSegment(sketch, "E578.MirrorCS", {"start": v(-1093.05, 319.84) * mm, "end": v(-1093.05, 323.01) * mm});
            skLineSegment(sketch, "E579.MirrorCS", {"start": v(-1052.5, 364.03) * mm, "end": v(-1049.74, 362.44) * mm});
            skLineSegment(sketch, "E580.MirrorCS", {"start": v(-1123.53, 323.01) * mm, "end": v(-1123.53, 319.84) * mm});
            skLineSegment(sketch, "E581.MirrorCS", {"start": v(-1056.1, 351.44) * mm, "end": v(-1058.84, 353.03) * mm});
            skLineSegment(sketch, "E582.MirrorCS", {"start": v(-1051.14, 367.64) * mm, "end": v(-1047.29, 365.42) * mm});
            skLineSegment(sketch, "E583.MirrorCS", {"start": v(-1057.36, 349.24) * mm, "end": v(-1060.11, 350.83) * mm});
            skLineSegment(sketch, "E584.MirrorCS", {"start": v(-1080.35, 323.01) * mm, "end": v(-1080.35, 319.84) * mm});
            skLineSegment(sketch, "E585.MirrorCS", {"start": v(-1066.46, 339.83) * mm, "end": v(-1063.29, 345.33) * mm});
            skLineSegment(sketch, "E586.MirrorCS", {"start": v(-1060.54, 343.74) * mm, "end": v(-1057.36, 349.24) * mm});
            skLineSegment(sketch, "E587.MirrorCS", {"start": v(-1063.29, 345.33) * mm, "end": v(-1060.11, 350.83) * mm});
            skLineSegment(sketch, "E588.MirrorCS", {"start": v(-1063.71, 338.24) * mm, "end": v(-1060.54, 343.74) * mm});
            skLineSegment(sketch, "E589.MirrorCS", {"start": v(-1058.84, 353.03) * mm, "end": v(-1052.5, 364.03) * mm});
            skLineSegment(sketch, "E590.MirrorCS", {"start": v(-1076.54, 323.65) * mm, "end": v(-1051.14, 367.64) * mm});
            skLineSegment(sketch, "E591.MirrorCS", {"start": v(-1071.33, 325.04) * mm, "end": v(-1064.98, 336.04) * mm});
            skPoint(sketch, "E592.MirrorP", {"position": v(-1061.91, 344.53) * mm});
            skLineSegment(sketch, "E593.MirrorCS", {"start": v(-1056.1, 351.44) * mm, "end": v(-1049.74, 362.44) * mm});
            skPoint(sketch, "E594.MirrorP", {"position": v(-1129.26, 322.54) * mm});
            skLineSegment(sketch, "E595.MirrorCS", {"start": v(-1074.08, 326.63) * mm, "end": v(-1067.73, 337.63) * mm});
            skLineSegment(sketch, "E596.MirrorCS", {"start": v(-1072.69, 321.43) * mm, "end": v(-1047.29, 365.42) * mm});
            skLineSegment(sketch, "E597", {"start": v(-1047.29, 369.87) * mm, "end": v(-1047.29, 365.42) * mm});
            skLineSegment(sketch, "E598.left", {"start": v(-1049.74, 362.44) * mm, "end": v(-1052.5, 364.03) * mm});
            skLineSegment(sketch, "E598.right", {"start": v(-1071.33, 325.04) * mm, "end": v(-1074.08, 326.63) * mm});
            skLineSegment(sketch, "E599", {"start": v(-1063.29, 345.33) * mm, "end": v(-1060.54, 343.74) * mm, "construction": true});
            skLineSegment(sketch, "E600", {"start": v(-1067.73, 337.63) * mm, "end": v(-1064.98, 336.04) * mm});
            skLineSegment(sketch, "E601.MirrorCS", {"start": v(-1058.84, 353.03) * mm, "end": v(-1056.1, 351.44) * mm});
            skLineSegment(sketch, "E602", {"start": v(-1066.46, 339.83) * mm, "end": v(-1063.71, 338.24) * mm});
            skLineSegment(sketch, "E603.MirrorCS", {"start": v(-1060.11, 350.83) * mm, "end": v(-1057.36, 349.24) * mm});
            skLineSegment(sketch, "E604.0", {"start": v(-1047.29, 365.42) * mm, "end": v(-1051.14, 367.64) * mm, "construction": true});
            skLineSegment(sketch, "E605", {"start": v(-1076.54, 416.08) * mm, "end": v(-1072.69, 413.86) * mm});
            skLineSegment(sketch, "E606.MirrorCS", {"start": v(-1063.29, 389.96) * mm, "end": v(-1060.54, 391.55) * mm, "construction": true});
            skLineSegment(sketch, "E607.MirrorCS", {"start": v(-1047.29, 369.87) * mm, "end": v(-1051.14, 367.64) * mm, "construction": true});
            skLineSegment(sketch, "E608.MirrorCS", {"start": v(-1060.11, 384.46) * mm, "end": v(-1057.36, 386.05) * mm});
            skLineSegment(sketch, "E609.MirrorCS", {"start": v(-1049.74, 372.85) * mm, "end": v(-1052.5, 371.26) * mm});
            skLineSegment(sketch, "E610.MirrorCS", {"start": v(-1071.33, 410.24) * mm, "end": v(-1074.08, 408.66) * mm});
            skLineSegment(sketch, "E611.MirrorCS", {"start": v(-1066.46, 395.46) * mm, "end": v(-1063.71, 397.04) * mm});
            skLineSegment(sketch, "E612.MirrorCS", {"start": v(-1076.54, 411.64) * mm, "end": v(-1072.69, 413.86) * mm});
            skLineSegment(sketch, "E613.MirrorCS", {"start": v(-1067.73, 397.66) * mm, "end": v(-1064.98, 399.24) * mm});
            skLineSegment(sketch, "E614.MirrorCS", {"start": v(-1058.84, 382.26) * mm, "end": v(-1056.1, 383.85) * mm});
            skLineSegment(sketch, "E615.MirrorCS", {"start": v(-1047.29, 365.42) * mm, "end": v(-1047.29, 369.87) * mm});
            skLineSegment(sketch, "E616", {"start": v(-1127.34, 416.08) * mm, "end": v(-1131.19, 413.86) * mm});
            skLineSegment(sketch, "E617.0", {"start": v(-1055.44, 367.5) * mm, "end": v(-1078.81, 327.3) * mm});
            skLineSegment(sketch, "E617.1", {"start": v(-1078.81, 327.3) * mm, "end": v(-1125.31, 327.45) * mm});
            skLineSegment(sketch, "E617.2", {"start": v(-1125.31, 327.45) * mm, "end": v(-1148.44, 367.79) * mm});
            skLineSegment(sketch, "E617.3", {"start": v(-1148.44, 367.79) * mm, "end": v(-1125.06, 407.98) * mm});
            skLineSegment(sketch, "E617.4", {"start": v(-1125.06, 407.98) * mm, "end": v(-1078.57, 407.84) * mm});
            skLineSegment(sketch, "E617.5", {"start": v(-1078.57, 407.84) * mm, "end": v(-1055.44, 367.5) * mm});
            skPoint(sketch, "E617.0.midPoint", {"position": v(-1067.13, 347.4) * mm});
            skLineSegment(sketch, "E618", {"start": v(-1127.34, 504.07) * mm, "end": v(-1076.54, 504.07) * mm});
            skLineSegment(sketch, "E619", {"start": v(-1127.34, 508.52) * mm, "end": v(-1127.34, 504.07) * mm});
            skLineSegment(sketch, "E620", {"start": v(-1076.54, 508.52) * mm, "end": v(-1076.54, 504.07) * mm});
            skPoint(sketch, "E621.endSnap0", {"position": v(-1076.54, 506.3) * mm});
            skLineSegment(sketch, "E622", {"start": v(-1127.34, 506.3) * mm, "end": v(-1076.54, 506.3) * mm, "construction": true});
            skLineSegment(sketch, "E623", {"start": v(-1127.34, 508.52) * mm, "end": v(-1076.54, 508.52) * mm});
            skLineSegment(sketch, "E624.left", {"start": v(-1080.35, 504.7) * mm, "end": v(-1080.35, 507.88) * mm});
            skLineSegment(sketch, "E624.right", {"start": v(-1123.53, 504.7) * mm, "end": v(-1123.53, 507.88) * mm});
            skPoint(sketch, "E624.middle", {"position": v(-1101.94, 506.3) * mm});
            skLineSegment(sketch, "E625", {"start": v(-1101.94, 507.88) * mm, "end": v(-1101.94, 504.7) * mm, "construction": true});
            skLineSegment(sketch, "E626", {"start": v(-1110.83, 507.88) * mm, "end": v(-1110.83, 504.7) * mm});
            skLineSegment(sketch, "E627.MirrorCS", {"start": v(-1093.05, 507.88) * mm, "end": v(-1093.05, 504.7) * mm});
            skLineSegment(sketch, "E628", {"start": v(-1108.29, 507.88) * mm, "end": v(-1108.29, 504.7) * mm});
            skLineSegment(sketch, "E629.MirrorCS", {"start": v(-1095.59, 507.88) * mm, "end": v(-1095.59, 504.7) * mm});
            skLineSegment(sketch, "E630", {"start": v(-1123.53, 507.88) * mm, "end": v(-1110.83, 507.88) * mm});
            skLineSegment(sketch, "E631", {"start": v(-1123.53, 504.7) * mm, "end": v(-1110.83, 504.7) * mm});
            skLineSegment(sketch, "E632", {"start": v(-1108.29, 504.7) * mm, "end": v(-1101.94, 504.7) * mm});
            skLineSegment(sketch, "E633", {"start": v(-1108.29, 507.88) * mm, "end": v(-1101.94, 507.88) * mm});
            skLineSegment(sketch, "E634", {"start": v(-1101.94, 507.88) * mm, "end": v(-1095.59, 507.88) * mm});
            skLineSegment(sketch, "E635", {"start": v(-1101.94, 504.7) * mm, "end": v(-1095.59, 504.7) * mm});
            skLineSegment(sketch, "E636", {"start": v(-1093.05, 507.88) * mm, "end": v(-1080.35, 507.88) * mm});
            skLineSegment(sketch, "E637", {"start": v(-1093.05, 504.7) * mm, "end": v(-1080.35, 504.7) * mm});
            skLineSegment(sketch, "E638", {"start": v(-1076.54, 504.07) * mm, "end": v(-1051.14, 460.08) * mm});
            skLineSegment(sketch, "E639", {"start": v(-1072.69, 506.3) * mm, "end": v(-1076.54, 504.07) * mm});
            skLineSegment(sketch, "E640", {"start": v(-1072.69, 506.3) * mm, "end": v(-1047.29, 462.3) * mm});
            skLineSegment(sketch, "E641.left", {"start": v(-1052.5, 463.7) * mm, "end": v(-1049.74, 465.28) * mm});
            skLineSegment(sketch, "E641.right", {"start": v(-1074.08, 501.09) * mm, "end": v(-1071.33, 502.68) * mm});
            skPoint(sketch, "E641.middle", {"position": v(-1061.91, 483.18) * mm});
            skLineSegment(sketch, "E642", {"start": v(-1060.54, 483.98) * mm, "end": v(-1063.29, 482.4) * mm, "construction": true});
            skLineSegment(sketch, "E643", {"start": v(-1064.98, 491.68) * mm, "end": v(-1067.73, 490.09) * mm});
            skLineSegment(sketch, "E644.MirrorCS", {"start": v(-1056.1, 476.28) * mm, "end": v(-1058.84, 474.7) * mm});
            skLineSegment(sketch, "E645", {"start": v(-1063.71, 489.48) * mm, "end": v(-1066.46, 487.9) * mm});
            skLineSegment(sketch, "E646.MirrorCS", {"start": v(-1057.36, 478.48) * mm, "end": v(-1060.11, 476.9) * mm});
            skLineSegment(sketch, "E647", {"start": v(-1071.33, 502.68) * mm, "end": v(-1064.98, 491.68) * mm});
            skLineSegment(sketch, "E648", {"start": v(-1074.08, 501.09) * mm, "end": v(-1067.73, 490.09) * mm});
            skLineSegment(sketch, "E649", {"start": v(-1066.46, 487.9) * mm, "end": v(-1063.29, 482.4) * mm});
            skLineSegment(sketch, "E650", {"start": v(-1063.71, 489.48) * mm, "end": v(-1060.54, 483.98) * mm});
            skLineSegment(sketch, "E651", {"start": v(-1060.54, 483.98) * mm, "end": v(-1057.36, 478.48) * mm});
            skLineSegment(sketch, "E652", {"start": v(-1063.29, 482.4) * mm, "end": v(-1060.11, 476.9) * mm});
            skLineSegment(sketch, "E653", {"start": v(-1056.1, 476.28) * mm, "end": v(-1049.74, 465.28) * mm});
            skLineSegment(sketch, "E654", {"start": v(-1058.84, 474.7) * mm, "end": v(-1052.5, 463.7) * mm});
            skLineSegment(sketch, "E655", {"start": v(-1152.74, 460.08) * mm, "end": v(-1127.34, 504.07) * mm});
            skLineSegment(sketch, "E656", {"start": v(-1131.19, 506.3) * mm, "end": v(-1127.34, 504.07) * mm});
            skPoint(sketch, "E657.endSnap0", {"position": v(-1129.26, 505.18) * mm});
            skLineSegment(sketch, "E658", {"start": v(-1156.59, 462.3) * mm, "end": v(-1131.19, 506.3) * mm});
            skLineSegment(sketch, "E659.left", {"start": v(-1129.8, 501.09) * mm, "end": v(-1132.54, 502.68) * mm});
            skLineSegment(sketch, "E659.right", {"start": v(-1151.38, 463.7) * mm, "end": v(-1154.13, 465.28) * mm});
            skPoint(sketch, "E659.middle", {"position": v(-1141.96, 483.18) * mm});
            skLineSegment(sketch, "E660", {"start": v(-1143.34, 483.98) * mm, "end": v(-1140.59, 482.4) * mm, "construction": true});
            skLineSegment(sketch, "E661", {"start": v(-1147.78, 476.28) * mm, "end": v(-1145.03, 474.7) * mm});
            skLineSegment(sketch, "E662.MirrorCS", {"start": v(-1138.9, 491.68) * mm, "end": v(-1136.14, 490.09) * mm});
            skLineSegment(sketch, "E663", {"start": v(-1146.51, 478.48) * mm, "end": v(-1143.76, 476.9) * mm});
            skLineSegment(sketch, "E664.MirrorCS", {"start": v(-1140.16, 489.48) * mm, "end": v(-1137.41, 487.9) * mm});
            skLineSegment(sketch, "E665", {"start": v(-1154.13, 465.28) * mm, "end": v(-1147.78, 476.28) * mm});
            skLineSegment(sketch, "E666", {"start": v(-1151.38, 463.7) * mm, "end": v(-1145.03, 474.7) * mm});
            skLineSegment(sketch, "E667", {"start": v(-1143.76, 476.9) * mm, "end": v(-1140.59, 482.4) * mm});
            skLineSegment(sketch, "E668", {"start": v(-1146.51, 478.48) * mm, "end": v(-1143.34, 483.98) * mm});
            skLineSegment(sketch, "E669", {"start": v(-1143.34, 483.98) * mm, "end": v(-1140.16, 489.48) * mm});
            skLineSegment(sketch, "E670", {"start": v(-1140.59, 482.4) * mm, "end": v(-1137.41, 487.9) * mm});
            skLineSegment(sketch, "E671", {"start": v(-1138.9, 491.68) * mm, "end": v(-1132.54, 502.68) * mm});
            skLineSegment(sketch, "E672", {"start": v(-1136.14, 490.09) * mm, "end": v(-1129.8, 501.09) * mm});
            skLineSegment(sketch, "E673.0", {"start": v(-1127.34, 504.07) * mm, "end": v(-1131.19, 506.3) * mm, "construction": true});
            skLineSegment(sketch, "E674", {"start": v(-1051.14, 460.08) * mm, "end": v(-1047.29, 462.3) * mm});
            skLineSegment(sketch, "E675.MirrorCS", {"start": v(-1060.54, 436.17) * mm, "end": v(-1063.29, 437.76) * mm, "construction": true});
            skLineSegment(sketch, "E676.MirrorCS", {"start": v(-1101.94, 412.27) * mm, "end": v(-1101.94, 415.45) * mm, "construction": true});
            skLineSegment(sketch, "E677.MirrorCS", {"start": v(-1072.69, 413.86) * mm, "end": v(-1076.54, 416.08) * mm});
            skLineSegment(sketch, "E678.MirrorCS", {"start": v(-1074.08, 419.06) * mm, "end": v(-1071.33, 417.48) * mm});
            skLineSegment(sketch, "E679.MirrorCS", {"start": v(-1095.59, 412.27) * mm, "end": v(-1095.59, 415.45) * mm});
            skLineSegment(sketch, "E680.MirrorCS", {"start": v(-1076.54, 411.64) * mm, "end": v(-1076.54, 416.08) * mm});
            skLineSegment(sketch, "E681.MirrorCS", {"start": v(-1110.83, 412.27) * mm, "end": v(-1110.83, 415.45) * mm});
            skLineSegment(sketch, "E682.MirrorCS", {"start": v(-1064.98, 428.48) * mm, "end": v(-1067.73, 430.06) * mm});
            skLineSegment(sketch, "E683.MirrorCS", {"start": v(-1108.29, 412.27) * mm, "end": v(-1108.29, 415.45) * mm});
            skLineSegment(sketch, "E684.MirrorCS", {"start": v(-1063.71, 430.68) * mm, "end": v(-1066.46, 432.26) * mm});
            skLineSegment(sketch, "E685.MirrorCS", {"start": v(-1093.05, 412.27) * mm, "end": v(-1093.05, 415.45) * mm});
            skLineSegment(sketch, "E686.MirrorCS", {"start": v(-1052.5, 456.46) * mm, "end": v(-1049.74, 454.87) * mm});
            skLineSegment(sketch, "E687.MirrorCS", {"start": v(-1123.53, 415.45) * mm, "end": v(-1123.53, 412.27) * mm});
            skLineSegment(sketch, "E688.MirrorCS", {"start": v(-1056.1, 443.87) * mm, "end": v(-1058.84, 445.46) * mm});
            skLineSegment(sketch, "E689.MirrorCS", {"start": v(-1051.14, 460.08) * mm, "end": v(-1047.29, 457.85) * mm});
            skLineSegment(sketch, "E690.MirrorCS", {"start": v(-1057.36, 441.67) * mm, "end": v(-1060.11, 443.26) * mm});
            skLineSegment(sketch, "E691.MirrorCS", {"start": v(-1080.35, 415.45) * mm, "end": v(-1080.35, 412.27) * mm});
            skLineSegment(sketch, "E692.MirrorCS", {"start": v(-1066.46, 432.26) * mm, "end": v(-1063.29, 437.76) * mm});
            skLineSegment(sketch, "E693.MirrorCS", {"start": v(-1060.54, 436.17) * mm, "end": v(-1057.36, 441.67) * mm});
            skLineSegment(sketch, "E694.MirrorCS", {"start": v(-1063.29, 437.76) * mm, "end": v(-1060.11, 443.26) * mm});
            skLineSegment(sketch, "E695.MirrorCS", {"start": v(-1063.71, 430.68) * mm, "end": v(-1060.54, 436.17) * mm});
            skLineSegment(sketch, "E696.MirrorCS", {"start": v(-1058.84, 445.46) * mm, "end": v(-1052.5, 456.46) * mm});
            skLineSegment(sketch, "E697.MirrorCS", {"start": v(-1076.54, 416.08) * mm, "end": v(-1051.14, 460.08) * mm});
            skLineSegment(sketch, "E698.MirrorCS", {"start": v(-1071.33, 417.48) * mm, "end": v(-1064.98, 428.48) * mm});
            skPoint(sketch, "E699.MirrorP", {"position": v(-1061.91, 436.97) * mm});
            skLineSegment(sketch, "E700.MirrorCS", {"start": v(-1056.1, 443.87) * mm, "end": v(-1049.74, 454.87) * mm});
            skPoint(sketch, "E701.MirrorP", {"position": v(-1129.26, 414.97) * mm});
            skLineSegment(sketch, "E702.MirrorCS", {"start": v(-1074.08, 419.06) * mm, "end": v(-1067.73, 430.06) * mm});
            skLineSegment(sketch, "E703.MirrorCS", {"start": v(-1072.69, 413.86) * mm, "end": v(-1047.29, 457.85) * mm});
            skLineSegment(sketch, "E704", {"start": v(-1047.29, 462.3) * mm, "end": v(-1047.29, 457.85) * mm});
            skLineSegment(sketch, "E705.left", {"start": v(-1049.74, 454.87) * mm, "end": v(-1052.5, 456.46) * mm});
            skLineSegment(sketch, "E705.right", {"start": v(-1071.33, 417.48) * mm, "end": v(-1074.08, 419.06) * mm});
            skLineSegment(sketch, "E706", {"start": v(-1063.29, 437.76) * mm, "end": v(-1060.54, 436.17) * mm, "construction": true});
            skLineSegment(sketch, "E707", {"start": v(-1067.73, 430.06) * mm, "end": v(-1064.98, 428.48) * mm});
            skLineSegment(sketch, "E708.MirrorCS", {"start": v(-1058.84, 445.46) * mm, "end": v(-1056.1, 443.87) * mm});
            skLineSegment(sketch, "E709", {"start": v(-1066.46, 432.26) * mm, "end": v(-1063.71, 430.68) * mm});
            skLineSegment(sketch, "E710.MirrorCS", {"start": v(-1060.11, 443.26) * mm, "end": v(-1057.36, 441.67) * mm});
            skLineSegment(sketch, "E711.0", {"start": v(-1047.29, 457.85) * mm, "end": v(-1051.14, 460.08) * mm, "construction": true});
            skLineSegment(sketch, "E712", {"start": v(-1076.54, 508.52) * mm, "end": v(-1072.69, 506.3) * mm});
            skLineSegment(sketch, "E713.MirrorCS", {"start": v(-1063.29, 482.4) * mm, "end": v(-1060.54, 483.98) * mm, "construction": true});
            skLineSegment(sketch, "E714.MirrorCS", {"start": v(-1047.29, 462.3) * mm, "end": v(-1051.14, 460.08) * mm, "construction": true});
            skLineSegment(sketch, "E715.MirrorCS", {"start": v(-1060.11, 476.9) * mm, "end": v(-1057.36, 478.48) * mm});
            skLineSegment(sketch, "E716.MirrorCS", {"start": v(-1049.74, 465.28) * mm, "end": v(-1052.5, 463.7) * mm});
            skLineSegment(sketch, "E717.MirrorCS", {"start": v(-1071.33, 502.68) * mm, "end": v(-1074.08, 501.09) * mm});
            skLineSegment(sketch, "E718.MirrorCS", {"start": v(-1066.46, 487.9) * mm, "end": v(-1063.71, 489.48) * mm});
            skLineSegment(sketch, "E719.MirrorCS", {"start": v(-1076.54, 504.07) * mm, "end": v(-1072.69, 506.3) * mm});
            skLineSegment(sketch, "E720.MirrorCS", {"start": v(-1067.73, 490.09) * mm, "end": v(-1064.98, 491.68) * mm});
            skLineSegment(sketch, "E721.MirrorCS", {"start": v(-1058.84, 474.7) * mm, "end": v(-1056.1, 476.28) * mm});
            skLineSegment(sketch, "E722.MirrorCS", {"start": v(-1047.29, 457.85) * mm, "end": v(-1047.29, 462.3) * mm});
            skLineSegment(sketch, "E723", {"start": v(-1127.34, 508.52) * mm, "end": v(-1131.19, 506.3) * mm});
            skLineSegment(sketch, "E724.0", {"start": v(-1055.44, 459.93) * mm, "end": v(-1078.81, 419.74) * mm});
            skLineSegment(sketch, "E724.1", {"start": v(-1078.81, 419.74) * mm, "end": v(-1125.31, 419.88) * mm});
            skLineSegment(sketch, "E724.2", {"start": v(-1125.31, 419.88) * mm, "end": v(-1148.44, 460.22) * mm});
            skLineSegment(sketch, "E724.3", {"start": v(-1148.44, 460.22) * mm, "end": v(-1125.06, 500.41) * mm});
            skLineSegment(sketch, "E724.4", {"start": v(-1125.06, 500.41) * mm, "end": v(-1078.57, 500.27) * mm});
            skLineSegment(sketch, "E724.5", {"start": v(-1078.57, 500.27) * mm, "end": v(-1055.44, 459.93) * mm});
            skPoint(sketch, "E724.0.midPoint", {"position": v(-1067.13, 439.84) * mm});
            skLineSegment(sketch, "E725", {"start": v(-1047.29, 180.55) * mm, "end": v(-996.49, 180.55) * mm});
            skLineSegment(sketch, "E726", {"start": v(-1047.29, 185) * mm, "end": v(-1047.29, 180.55) * mm});
            skLineSegment(sketch, "E727", {"start": v(-996.49, 185) * mm, "end": v(-996.49, 180.55) * mm});
            skPoint(sketch, "E728.endSnap0", {"position": v(-996.49, 182.78) * mm});
            skLineSegment(sketch, "E729", {"start": v(-1047.29, 182.78) * mm, "end": v(-996.49, 182.78) * mm, "construction": true});
            skLineSegment(sketch, "E730", {"start": v(-1047.29, 185) * mm, "end": v(-996.49, 185) * mm});
            skLineSegment(sketch, "E731.left", {"start": v(-1000.3, 181.19) * mm, "end": v(-1000.3, 184.36) * mm});
            skLineSegment(sketch, "E731.right", {"start": v(-1043.48, 181.19) * mm, "end": v(-1043.48, 184.36) * mm});
            skPoint(sketch, "E731.middle", {"position": v(-1021.89, 182.78) * mm});
            skLineSegment(sketch, "E732", {"start": v(-1021.89, 184.36) * mm, "end": v(-1021.89, 181.19) * mm, "construction": true});
            skLineSegment(sketch, "E733", {"start": v(-1030.78, 184.36) * mm, "end": v(-1030.78, 181.19) * mm});
            skLineSegment(sketch, "E734.MirrorCS", {"start": v(-1013, 184.36) * mm, "end": v(-1013, 181.19) * mm});
            skLineSegment(sketch, "E735", {"start": v(-1028.24, 184.36) * mm, "end": v(-1028.24, 181.19) * mm});
            skLineSegment(sketch, "E736.MirrorCS", {"start": v(-1015.54, 184.36) * mm, "end": v(-1015.54, 181.19) * mm});
            skLineSegment(sketch, "E737", {"start": v(-1043.48, 184.36) * mm, "end": v(-1030.78, 184.36) * mm});
            skLineSegment(sketch, "E738", {"start": v(-1043.48, 181.19) * mm, "end": v(-1030.78, 181.19) * mm});
            skLineSegment(sketch, "E739", {"start": v(-1028.24, 181.19) * mm, "end": v(-1021.89, 181.19) * mm});
            skLineSegment(sketch, "E740", {"start": v(-1028.24, 184.36) * mm, "end": v(-1021.89, 184.36) * mm});
            skLineSegment(sketch, "E741", {"start": v(-1021.89, 184.36) * mm, "end": v(-1015.54, 184.36) * mm});
            skLineSegment(sketch, "E742", {"start": v(-1021.89, 181.19) * mm, "end": v(-1015.54, 181.19) * mm});
            skLineSegment(sketch, "E743", {"start": v(-1013, 184.36) * mm, "end": v(-1000.3, 184.36) * mm});
            skLineSegment(sketch, "E744", {"start": v(-1013, 181.19) * mm, "end": v(-1000.3, 181.19) * mm});
            skLineSegment(sketch, "E745", {"start": v(-992.64, 182.78) * mm, "end": v(-996.49, 180.55) * mm});
            skLineSegment(sketch, "E746", {"start": v(-1051.14, 182.78) * mm, "end": v(-1047.29, 180.55) * mm});
            skPoint(sketch, "E747.endSnap0", {"position": v(-1049.21, 181.67) * mm});
            skLineSegment(sketch, "E748.0", {"start": v(-1047.29, 180.55) * mm, "end": v(-1051.14, 182.78) * mm, "construction": true});
            skLineSegment(sketch, "E749", {"start": v(-1047.29, 272.99) * mm, "end": v(-996.49, 272.99) * mm});
            skLineSegment(sketch, "E750", {"start": v(-996.49, 277.43) * mm, "end": v(-996.49, 272.99) * mm});
            skPoint(sketch, "E751.endSnap0", {"position": v(-996.49, 275.21) * mm});
            skLineSegment(sketch, "E752", {"start": v(-1047.29, 275.21) * mm, "end": v(-996.49, 275.21) * mm, "construction": true});
            skLineSegment(sketch, "E753", {"start": v(-1047.29, 277.43) * mm, "end": v(-996.49, 277.43) * mm});
            skLineSegment(sketch, "E754.left", {"start": v(-1000.3, 273.62) * mm, "end": v(-1000.3, 276.8) * mm});
            skLineSegment(sketch, "E754.right", {"start": v(-1043.48, 273.62) * mm, "end": v(-1043.48, 276.8) * mm});
            skPoint(sketch, "E754.middle", {"position": v(-1021.89, 275.21) * mm});
            skLineSegment(sketch, "E755", {"start": v(-1021.89, 276.8) * mm, "end": v(-1021.89, 273.62) * mm, "construction": true});
            skLineSegment(sketch, "E756", {"start": v(-1030.78, 276.8) * mm, "end": v(-1030.78, 273.62) * mm});
            skLineSegment(sketch, "E757.MirrorCS", {"start": v(-1013, 276.8) * mm, "end": v(-1013, 273.62) * mm});
            skLineSegment(sketch, "E758", {"start": v(-1028.24, 276.8) * mm, "end": v(-1028.24, 273.62) * mm});
            skLineSegment(sketch, "E759.MirrorCS", {"start": v(-1015.54, 276.8) * mm, "end": v(-1015.54, 273.62) * mm});
            skLineSegment(sketch, "E760", {"start": v(-1043.48, 276.8) * mm, "end": v(-1030.78, 276.8) * mm});
            skLineSegment(sketch, "E761", {"start": v(-1043.48, 273.62) * mm, "end": v(-1030.78, 273.62) * mm});
            skLineSegment(sketch, "E762", {"start": v(-1028.24, 273.62) * mm, "end": v(-1021.89, 273.62) * mm});
            skLineSegment(sketch, "E763", {"start": v(-1028.24, 276.8) * mm, "end": v(-1021.89, 276.8) * mm});
            skLineSegment(sketch, "E764", {"start": v(-1021.89, 276.8) * mm, "end": v(-1015.54, 276.8) * mm});
            skLineSegment(sketch, "E765", {"start": v(-1021.89, 273.62) * mm, "end": v(-1015.54, 273.62) * mm});
            skLineSegment(sketch, "E766", {"start": v(-1013, 276.8) * mm, "end": v(-1000.3, 276.8) * mm});
            skLineSegment(sketch, "E767", {"start": v(-1013, 273.62) * mm, "end": v(-1000.3, 273.62) * mm});
            skLineSegment(sketch, "E768", {"start": v(-996.49, 272.99) * mm, "end": v(-971.09, 229) * mm});
            skLineSegment(sketch, "E769", {"start": v(-992.64, 275.21) * mm, "end": v(-996.49, 272.99) * mm});
            skLineSegment(sketch, "E770", {"start": v(-992.64, 275.21) * mm, "end": v(-967.24, 231.22) * mm});
            skLineSegment(sketch, "E771.left", {"start": v(-972.44, 232.61) * mm, "end": v(-969.7, 234.2) * mm});
            skLineSegment(sketch, "E771.right", {"start": v(-994.03, 270) * mm, "end": v(-991.29, 271.6) * mm});
            skPoint(sketch, "E771.middle", {"position": v(-981.87, 252.1) * mm});
            skLineSegment(sketch, "E772", {"start": v(-980.5, 252.9) * mm, "end": v(-983.24, 251.3) * mm, "construction": true});
            skLineSegment(sketch, "E773", {"start": v(-984.94, 260.6) * mm, "end": v(-987.68, 259) * mm});
            skLineSegment(sketch, "E774.MirrorCS", {"start": v(-976.05, 245.2) * mm, "end": v(-978.8, 243.6) * mm});
            skLineSegment(sketch, "E775", {"start": v(-983.67, 258.4) * mm, "end": v(-986.41, 256.8) * mm});
            skLineSegment(sketch, "E776.MirrorCS", {"start": v(-977.32, 247.4) * mm, "end": v(-980.06, 245.8) * mm});
            skLineSegment(sketch, "E777", {"start": v(-991.29, 271.6) * mm, "end": v(-984.94, 260.6) * mm});
            skLineSegment(sketch, "E778", {"start": v(-994.03, 270) * mm, "end": v(-987.68, 259) * mm});
            skLineSegment(sketch, "E779", {"start": v(-986.41, 256.8) * mm, "end": v(-983.24, 251.3) * mm});
            skLineSegment(sketch, "E780", {"start": v(-983.67, 258.4) * mm, "end": v(-980.5, 252.9) * mm});
            skLineSegment(sketch, "E781", {"start": v(-980.5, 252.9) * mm, "end": v(-977.32, 247.4) * mm});
            skLineSegment(sketch, "E782", {"start": v(-983.24, 251.3) * mm, "end": v(-980.06, 245.8) * mm});
            skLineSegment(sketch, "E783", {"start": v(-976.05, 245.2) * mm, "end": v(-969.7, 234.2) * mm});
            skLineSegment(sketch, "E784", {"start": v(-978.8, 243.6) * mm, "end": v(-972.44, 232.61) * mm});
            skPoint(sketch, "E785.endSnap0", {"position": v(-1049.21, 274.1) * mm});
            skLineSegment(sketch, "E786", {"start": v(-971.09, 229) * mm, "end": v(-967.24, 231.22) * mm});
            skLineSegment(sketch, "E787.MirrorCS", {"start": v(-1051.14, 182.78) * mm, "end": v(-1047.29, 185) * mm});
            skLineSegment(sketch, "E788.MirrorCS", {"start": v(-980.5, 205.1) * mm, "end": v(-983.24, 206.68) * mm, "construction": true});
            skLineSegment(sketch, "E789.MirrorCS", {"start": v(-1063.29, 205.1) * mm, "end": v(-1060.54, 206.68) * mm, "construction": true});
            skLineSegment(sketch, "E790.MirrorCS", {"start": v(-1021.89, 181.19) * mm, "end": v(-1021.89, 184.36) * mm, "construction": true});
            skLineSegment(sketch, "E791.MirrorCS", {"start": v(-1047.29, 185) * mm, "end": v(-1051.14, 182.78) * mm, "construction": true});
            skLineSegment(sketch, "E792.MirrorCS", {"start": v(-992.64, 182.78) * mm, "end": v(-996.49, 185) * mm});
            skLineSegment(sketch, "E793.MirrorCS", {"start": v(-994.03, 187.98) * mm, "end": v(-991.29, 186.4) * mm});
            skLineSegment(sketch, "E794.MirrorCS", {"start": v(-1060.11, 199.6) * mm, "end": v(-1057.36, 201.18) * mm});
            skLineSegment(sketch, "E795.MirrorCS", {"start": v(-1015.54, 181.19) * mm, "end": v(-1015.54, 184.36) * mm});
            skLineSegment(sketch, "E796.MirrorCS", {"start": v(-996.49, 180.55) * mm, "end": v(-996.49, 185) * mm});
            skLineSegment(sketch, "E797.MirrorCS", {"start": v(-1030.78, 181.19) * mm, "end": v(-1030.78, 184.36) * mm});
            skLineSegment(sketch, "E798.MirrorCS", {"start": v(-984.94, 197.4) * mm, "end": v(-987.68, 198.98) * mm});
            skLineSegment(sketch, "E799.MirrorCS", {"start": v(-1028.24, 181.19) * mm, "end": v(-1028.24, 184.36) * mm});
            skLineSegment(sketch, "E800.MirrorCS", {"start": v(-1049.74, 187.98) * mm, "end": v(-1052.5, 186.4) * mm});
            skLineSegment(sketch, "E801.MirrorCS", {"start": v(-1071.33, 225.38) * mm, "end": v(-1074.08, 223.79) * mm});
            skLineSegment(sketch, "E802.MirrorCS", {"start": v(-1066.46, 210.6) * mm, "end": v(-1063.71, 212.18) * mm});
            skLineSegment(sketch, "E803.MirrorCS", {"start": v(-983.67, 199.6) * mm, "end": v(-986.41, 201.18) * mm});
            skLineSegment(sketch, "E804.MirrorCS", {"start": v(-1013, 181.19) * mm, "end": v(-1013, 184.36) * mm});
            skLineSegment(sketch, "E805.MirrorCS", {"start": v(-1067.73, 212.8) * mm, "end": v(-1064.98, 214.38) * mm});
            skLineSegment(sketch, "E806.MirrorCS", {"start": v(-972.44, 225.38) * mm, "end": v(-969.7, 223.79) * mm});
            skLineSegment(sketch, "E807.MirrorCS", {"start": v(-1043.48, 184.36) * mm, "end": v(-1043.48, 181.19) * mm});
            skLineSegment(sketch, "E808.MirrorCS", {"start": v(-976.05, 212.8) * mm, "end": v(-978.8, 214.38) * mm});
            skLineSegment(sketch, "E809.MirrorCS", {"start": v(-971.09, 229) * mm, "end": v(-967.24, 226.77) * mm});
            skLineSegment(sketch, "E810.MirrorCS", {"start": v(-977.32, 210.6) * mm, "end": v(-980.06, 212.18) * mm});
            skLineSegment(sketch, "E811.MirrorCS", {"start": v(-1058.84, 197.4) * mm, "end": v(-1056.1, 198.98) * mm});
            skLineSegment(sketch, "E812.MirrorCS", {"start": v(-1000.3, 184.36) * mm, "end": v(-1000.3, 181.19) * mm});
            skLineSegment(sketch, "E813.MirrorCS", {"start": v(-986.41, 201.18) * mm, "end": v(-983.24, 206.68) * mm});
            skLineSegment(sketch, "E814.MirrorCS", {"start": v(-1063.71, 212.18) * mm, "end": v(-1060.54, 206.68) * mm});
            skLineSegment(sketch, "E815.MirrorCS", {"start": v(-980.5, 205.1) * mm, "end": v(-977.32, 210.6) * mm});
            skLineSegment(sketch, "E816.MirrorCS", {"start": v(-1047.29, 180.55) * mm, "end": v(-1047.29, 185) * mm});
            skLineSegment(sketch, "E817.MirrorCS", {"start": v(-983.24, 206.68) * mm, "end": v(-980.06, 212.18) * mm});
            skLineSegment(sketch, "E818.MirrorCS", {"start": v(-983.67, 199.6) * mm, "end": v(-980.5, 205.1) * mm});
            skLineSegment(sketch, "E819.MirrorCS", {"start": v(-1060.54, 206.68) * mm, "end": v(-1057.36, 201.18) * mm});
            skLineSegment(sketch, "E820.MirrorCS", {"start": v(-978.8, 214.38) * mm, "end": v(-972.44, 225.38) * mm});
            skLineSegment(sketch, "E821.MirrorCS", {"start": v(-1076.54, 226.77) * mm, "end": v(-1051.14, 182.78) * mm});
            skLineSegment(sketch, "E822.MirrorCS", {"start": v(-996.49, 185) * mm, "end": v(-971.09, 229) * mm});
            skLineSegment(sketch, "E823.MirrorCS", {"start": v(-991.29, 186.4) * mm, "end": v(-984.94, 197.4) * mm});
            skLineSegment(sketch, "E824.MirrorCS", {"start": v(-1071.33, 225.38) * mm, "end": v(-1064.98, 214.38) * mm});
            skLineSegment(sketch, "E825.MirrorCS", {"start": v(-1056.1, 198.98) * mm, "end": v(-1049.74, 187.98) * mm});
            skPoint(sketch, "E826.MirrorP", {"position": v(-981.87, 205.89) * mm});
            skLineSegment(sketch, "E827.MirrorCS", {"start": v(-976.05, 212.8) * mm, "end": v(-969.7, 223.79) * mm});
            skPoint(sketch, "E828.MirrorP", {"position": v(-1049.21, 183.89) * mm});
            skLineSegment(sketch, "E829.MirrorCS", {"start": v(-1066.46, 210.6) * mm, "end": v(-1063.29, 205.1) * mm});
            skPoint(sketch, "E830.MirrorP", {"position": v(-1061.91, 205.89) * mm});
            skLineSegment(sketch, "E831.MirrorCS", {"start": v(-994.03, 187.98) * mm, "end": v(-987.68, 198.98) * mm});
            skLineSegment(sketch, "E832.MirrorCS", {"start": v(-992.64, 182.78) * mm, "end": v(-967.24, 226.77) * mm});
            skLineSegment(sketch, "E833.MirrorCS", {"start": v(-1072.69, 229) * mm, "end": v(-1047.29, 185) * mm});
            skLineSegment(sketch, "E834.MirrorCS", {"start": v(-1058.84, 197.4) * mm, "end": v(-1052.5, 186.4) * mm});
            skLineSegment(sketch, "E835.MirrorCS", {"start": v(-1074.08, 223.79) * mm, "end": v(-1067.73, 212.8) * mm});
            skLineSegment(sketch, "E836.MirrorCS", {"start": v(-1063.29, 205.1) * mm, "end": v(-1060.11, 199.6) * mm});
            skLineSegment(sketch, "E837", {"start": v(-967.24, 231.22) * mm, "end": v(-967.24, 226.77) * mm});
            skLineSegment(sketch, "E838", {"start": v(-996.49, 185) * mm, "end": v(-992.64, 182.78) * mm});
            skLineSegment(sketch, "E839.left", {"start": v(-969.7, 223.79) * mm, "end": v(-972.44, 225.38) * mm});
            skLineSegment(sketch, "E839.right", {"start": v(-991.29, 186.4) * mm, "end": v(-994.03, 187.98) * mm});
            skLineSegment(sketch, "E840", {"start": v(-983.24, 206.68) * mm, "end": v(-980.5, 205.1) * mm, "construction": true});
            skLineSegment(sketch, "E841", {"start": v(-987.68, 198.98) * mm, "end": v(-984.94, 197.4) * mm});
            skLineSegment(sketch, "E842.MirrorCS", {"start": v(-978.8, 214.38) * mm, "end": v(-976.05, 212.8) * mm});
            skLineSegment(sketch, "E843", {"start": v(-986.41, 201.18) * mm, "end": v(-983.67, 199.6) * mm});
            skLineSegment(sketch, "E844.MirrorCS", {"start": v(-980.06, 212.18) * mm, "end": v(-977.32, 210.6) * mm});
            skLineSegment(sketch, "E845.0", {"start": v(-967.24, 226.77) * mm, "end": v(-971.09, 229) * mm, "construction": true});
            skLineSegment(sketch, "E846.MirrorCS", {"start": v(-996.49, 180.55) * mm, "end": v(-992.64, 182.78) * mm});
            skLineSegment(sketch, "E847", {"start": v(-996.49, 277.43) * mm, "end": v(-992.64, 275.21) * mm});
            skLineSegment(sketch, "E848.MirrorCS", {"start": v(-983.24, 251.3) * mm, "end": v(-980.5, 252.9) * mm, "construction": true});
            skLineSegment(sketch, "E849.MirrorCS", {"start": v(-967.24, 231.22) * mm, "end": v(-971.09, 229) * mm, "construction": true});
            skLineSegment(sketch, "E850.MirrorCS", {"start": v(-980.06, 245.8) * mm, "end": v(-977.32, 247.4) * mm});
            skLineSegment(sketch, "E851.MirrorCS", {"start": v(-969.7, 234.2) * mm, "end": v(-972.44, 232.61) * mm});
            skLineSegment(sketch, "E852.MirrorCS", {"start": v(-991.29, 271.6) * mm, "end": v(-994.03, 270) * mm});
            skLineSegment(sketch, "E853.MirrorCS", {"start": v(-986.41, 256.8) * mm, "end": v(-983.67, 258.4) * mm});
            skLineSegment(sketch, "E854.MirrorCS", {"start": v(-996.49, 272.99) * mm, "end": v(-992.64, 275.21) * mm});
            skLineSegment(sketch, "E855.MirrorCS", {"start": v(-987.68, 259) * mm, "end": v(-984.94, 260.6) * mm});
            skLineSegment(sketch, "E856.MirrorCS", {"start": v(-978.8, 243.6) * mm, "end": v(-976.05, 245.2) * mm});
            skLineSegment(sketch, "E857.MirrorCS", {"start": v(-967.24, 226.77) * mm, "end": v(-967.24, 231.22) * mm});
            skLineSegment(sketch, "E858", {"start": v(-1047.29, 277.43) * mm, "end": v(-1051.14, 275.21) * mm});
            skLineSegment(sketch, "E859.0", {"start": v(-975.4, 228.85) * mm, "end": v(-998.76, 188.66) * mm});
            skLineSegment(sketch, "E859.1", {"start": v(-998.76, 188.66) * mm, "end": v(-1045.26, 188.8) * mm});
            skLineSegment(sketch, "E859.2", {"start": v(-1045.26, 188.8) * mm, "end": v(-1068.39, 229.14) * mm});
            skLineSegment(sketch, "E859.3", {"start": v(-1068.39, 229.14) * mm, "end": v(-1045.01, 269.33) * mm});
            skLineSegment(sketch, "E859.4", {"start": v(-1045.01, 269.33) * mm, "end": v(-998.52, 269.19) * mm});
            skLineSegment(sketch, "E859.5", {"start": v(-998.52, 269.19) * mm, "end": v(-975.4, 228.85) * mm});
            skPoint(sketch, "E859.0.midPoint", {"position": v(-987.08, 208.75) * mm});
            skLineSegment(sketch, "E860", {"start": v(-1047.29, 365.42) * mm, "end": v(-996.49, 365.42) * mm});
            skLineSegment(sketch, "E861", {"start": v(-996.49, 369.87) * mm, "end": v(-996.49, 365.42) * mm});
            skPoint(sketch, "E862.endSnap0", {"position": v(-996.49, 367.64) * mm});
            skLineSegment(sketch, "E863", {"start": v(-1047.29, 367.64) * mm, "end": v(-996.49, 367.64) * mm, "construction": true});
            skLineSegment(sketch, "E864", {"start": v(-1047.29, 369.87) * mm, "end": v(-996.49, 369.87) * mm});
            skLineSegment(sketch, "E865.left", {"start": v(-1000.3, 366.06) * mm, "end": v(-1000.3, 369.23) * mm});
            skLineSegment(sketch, "E865.right", {"start": v(-1043.48, 366.06) * mm, "end": v(-1043.48, 369.23) * mm});
            skPoint(sketch, "E865.middle", {"position": v(-1021.89, 367.64) * mm});
            skLineSegment(sketch, "E866", {"start": v(-1021.89, 369.23) * mm, "end": v(-1021.89, 366.06) * mm, "construction": true});
            skLineSegment(sketch, "E867", {"start": v(-1030.78, 369.23) * mm, "end": v(-1030.78, 366.06) * mm});
            skLineSegment(sketch, "E868.MirrorCS", {"start": v(-1013, 369.23) * mm, "end": v(-1013, 366.06) * mm});
            skLineSegment(sketch, "E869", {"start": v(-1028.24, 369.23) * mm, "end": v(-1028.24, 366.06) * mm});
            skLineSegment(sketch, "E870.MirrorCS", {"start": v(-1015.54, 369.23) * mm, "end": v(-1015.54, 366.06) * mm});
            skLineSegment(sketch, "E871", {"start": v(-1043.48, 369.23) * mm, "end": v(-1030.78, 369.23) * mm});
            skLineSegment(sketch, "E872", {"start": v(-1043.48, 366.06) * mm, "end": v(-1030.78, 366.06) * mm});
            skLineSegment(sketch, "E873", {"start": v(-1028.24, 366.06) * mm, "end": v(-1021.89, 366.06) * mm});
            skLineSegment(sketch, "E874", {"start": v(-1028.24, 369.23) * mm, "end": v(-1021.89, 369.23) * mm});
            skLineSegment(sketch, "E875", {"start": v(-1021.89, 369.23) * mm, "end": v(-1015.54, 369.23) * mm});
            skLineSegment(sketch, "E876", {"start": v(-1021.89, 366.06) * mm, "end": v(-1015.54, 366.06) * mm});
            skLineSegment(sketch, "E877", {"start": v(-1013, 369.23) * mm, "end": v(-1000.3, 369.23) * mm});
            skLineSegment(sketch, "E878", {"start": v(-1013, 366.06) * mm, "end": v(-1000.3, 366.06) * mm});
            skLineSegment(sketch, "E879", {"start": v(-996.49, 365.42) * mm, "end": v(-971.09, 321.43) * mm});
            skLineSegment(sketch, "E880", {"start": v(-992.64, 367.64) * mm, "end": v(-996.49, 365.42) * mm});
            skLineSegment(sketch, "E881", {"start": v(-992.64, 367.64) * mm, "end": v(-967.24, 323.65) * mm});
            skLineSegment(sketch, "E882.left", {"start": v(-972.44, 325.04) * mm, "end": v(-969.7, 326.63) * mm});
            skLineSegment(sketch, "E882.right", {"start": v(-994.03, 362.44) * mm, "end": v(-991.29, 364.03) * mm});
            skPoint(sketch, "E882.middle", {"position": v(-981.87, 344.53) * mm});
            skLineSegment(sketch, "E883", {"start": v(-980.5, 345.33) * mm, "end": v(-983.24, 343.74) * mm, "construction": true});
            skLineSegment(sketch, "E884", {"start": v(-984.94, 353.03) * mm, "end": v(-987.68, 351.44) * mm});
            skLineSegment(sketch, "E885.MirrorCS", {"start": v(-976.05, 337.63) * mm, "end": v(-978.8, 336.04) * mm});
            skLineSegment(sketch, "E886", {"start": v(-983.67, 350.83) * mm, "end": v(-986.41, 349.24) * mm});
            skLineSegment(sketch, "E887.MirrorCS", {"start": v(-977.32, 339.83) * mm, "end": v(-980.06, 338.24) * mm});
            skLineSegment(sketch, "E888", {"start": v(-991.29, 364.03) * mm, "end": v(-984.94, 353.03) * mm});
            skLineSegment(sketch, "E889", {"start": v(-994.03, 362.44) * mm, "end": v(-987.68, 351.44) * mm});
            skLineSegment(sketch, "E890", {"start": v(-986.41, 349.24) * mm, "end": v(-983.24, 343.74) * mm});
            skLineSegment(sketch, "E891", {"start": v(-983.67, 350.83) * mm, "end": v(-980.5, 345.33) * mm});
            skLineSegment(sketch, "E892", {"start": v(-980.5, 345.33) * mm, "end": v(-977.32, 339.83) * mm});
            skLineSegment(sketch, "E893", {"start": v(-983.24, 343.74) * mm, "end": v(-980.06, 338.24) * mm});
            skLineSegment(sketch, "E894", {"start": v(-976.05, 337.63) * mm, "end": v(-969.7, 326.63) * mm});
            skLineSegment(sketch, "E895", {"start": v(-978.8, 336.04) * mm, "end": v(-972.44, 325.04) * mm});
            skPoint(sketch, "E896.endSnap0", {"position": v(-1049.21, 366.53) * mm});
            skLineSegment(sketch, "E897", {"start": v(-971.09, 321.43) * mm, "end": v(-967.24, 323.65) * mm});
            skLineSegment(sketch, "E898.MirrorCS", {"start": v(-980.5, 297.52) * mm, "end": v(-983.24, 299.11) * mm, "construction": true});
            skLineSegment(sketch, "E899.MirrorCS", {"start": v(-1021.89, 273.62) * mm, "end": v(-1021.89, 276.8) * mm, "construction": true});
            skLineSegment(sketch, "E900.MirrorCS", {"start": v(-992.64, 275.21) * mm, "end": v(-996.49, 277.43) * mm});
            skLineSegment(sketch, "E901.MirrorCS", {"start": v(-994.03, 280.41) * mm, "end": v(-991.29, 278.83) * mm});
            skLineSegment(sketch, "E902.MirrorCS", {"start": v(-1015.54, 273.62) * mm, "end": v(-1015.54, 276.8) * mm});
            skLineSegment(sketch, "E903.MirrorCS", {"start": v(-996.49, 272.99) * mm, "end": v(-996.49, 277.43) * mm});
            skLineSegment(sketch, "E904.MirrorCS", {"start": v(-1030.78, 273.62) * mm, "end": v(-1030.78, 276.8) * mm});
            skLineSegment(sketch, "E905.MirrorCS", {"start": v(-984.94, 289.83) * mm, "end": v(-987.68, 291.41) * mm});
            skLineSegment(sketch, "E906.MirrorCS", {"start": v(-1028.24, 273.62) * mm, "end": v(-1028.24, 276.8) * mm});
            skLineSegment(sketch, "E907.MirrorCS", {"start": v(-983.67, 292.03) * mm, "end": v(-986.41, 293.61) * mm});
            skLineSegment(sketch, "E908.MirrorCS", {"start": v(-1013, 273.62) * mm, "end": v(-1013, 276.8) * mm});
            skLineSegment(sketch, "E909.MirrorCS", {"start": v(-972.44, 317.8) * mm, "end": v(-969.7, 316.22) * mm});
            skLineSegment(sketch, "E910.MirrorCS", {"start": v(-1043.48, 276.8) * mm, "end": v(-1043.48, 273.62) * mm});
            skLineSegment(sketch, "E911.MirrorCS", {"start": v(-976.05, 305.22) * mm, "end": v(-978.8, 306.81) * mm});
            skLineSegment(sketch, "E912.MirrorCS", {"start": v(-971.09, 321.43) * mm, "end": v(-967.24, 319.2) * mm});
            skLineSegment(sketch, "E913.MirrorCS", {"start": v(-977.32, 303.02) * mm, "end": v(-980.06, 304.61) * mm});
            skLineSegment(sketch, "E914.MirrorCS", {"start": v(-1000.3, 276.8) * mm, "end": v(-1000.3, 273.62) * mm});
            skLineSegment(sketch, "E915.MirrorCS", {"start": v(-986.41, 293.61) * mm, "end": v(-983.24, 299.11) * mm});
            skLineSegment(sketch, "E916.MirrorCS", {"start": v(-980.5, 297.52) * mm, "end": v(-977.32, 303.02) * mm});
            skLineSegment(sketch, "E917.MirrorCS", {"start": v(-983.24, 299.11) * mm, "end": v(-980.06, 304.61) * mm});
            skLineSegment(sketch, "E918.MirrorCS", {"start": v(-983.67, 292.03) * mm, "end": v(-980.5, 297.52) * mm});
            skLineSegment(sketch, "E919.MirrorCS", {"start": v(-978.8, 306.81) * mm, "end": v(-972.44, 317.8) * mm});
            skLineSegment(sketch, "E920.MirrorCS", {"start": v(-996.49, 277.43) * mm, "end": v(-971.09, 321.43) * mm});
            skLineSegment(sketch, "E921.MirrorCS", {"start": v(-991.29, 278.83) * mm, "end": v(-984.94, 289.83) * mm});
            skPoint(sketch, "E922.MirrorP", {"position": v(-981.87, 298.32) * mm});
            skLineSegment(sketch, "E923.MirrorCS", {"start": v(-976.05, 305.22) * mm, "end": v(-969.7, 316.22) * mm});
            skPoint(sketch, "E924.MirrorP", {"position": v(-1049.21, 276.32) * mm});
            skLineSegment(sketch, "E925.MirrorCS", {"start": v(-994.03, 280.41) * mm, "end": v(-987.68, 291.41) * mm});
            skLineSegment(sketch, "E926.MirrorCS", {"start": v(-992.64, 275.21) * mm, "end": v(-967.24, 319.2) * mm});
            skLineSegment(sketch, "E927", {"start": v(-967.24, 323.65) * mm, "end": v(-967.24, 319.2) * mm});
            skLineSegment(sketch, "E928.left", {"start": v(-969.7, 316.22) * mm, "end": v(-972.44, 317.8) * mm});
            skLineSegment(sketch, "E928.right", {"start": v(-991.29, 278.83) * mm, "end": v(-994.03, 280.41) * mm});
            skLineSegment(sketch, "E929", {"start": v(-983.24, 299.11) * mm, "end": v(-980.5, 297.52) * mm, "construction": true});
            skLineSegment(sketch, "E930", {"start": v(-987.68, 291.41) * mm, "end": v(-984.94, 289.83) * mm});
            skLineSegment(sketch, "E931.MirrorCS", {"start": v(-978.8, 306.81) * mm, "end": v(-976.05, 305.22) * mm});
            skLineSegment(sketch, "E932", {"start": v(-986.41, 293.61) * mm, "end": v(-983.67, 292.03) * mm});
            skLineSegment(sketch, "E933.MirrorCS", {"start": v(-980.06, 304.61) * mm, "end": v(-977.32, 303.02) * mm});
            skLineSegment(sketch, "E934.0", {"start": v(-967.24, 319.2) * mm, "end": v(-971.09, 321.43) * mm, "construction": true});
            skLineSegment(sketch, "E935", {"start": v(-996.49, 369.87) * mm, "end": v(-992.64, 367.64) * mm});
            skLineSegment(sketch, "E936.MirrorCS", {"start": v(-983.24, 343.74) * mm, "end": v(-980.5, 345.33) * mm, "construction": true});
            skLineSegment(sketch, "E937.MirrorCS", {"start": v(-967.24, 323.65) * mm, "end": v(-971.09, 321.43) * mm, "construction": true});
            skLineSegment(sketch, "E938.MirrorCS", {"start": v(-980.06, 338.24) * mm, "end": v(-977.32, 339.83) * mm});
            skLineSegment(sketch, "E939.MirrorCS", {"start": v(-969.7, 326.63) * mm, "end": v(-972.44, 325.04) * mm});
            skLineSegment(sketch, "E940.MirrorCS", {"start": v(-991.29, 364.03) * mm, "end": v(-994.03, 362.44) * mm});
            skLineSegment(sketch, "E941.MirrorCS", {"start": v(-986.41, 349.24) * mm, "end": v(-983.67, 350.83) * mm});
            skLineSegment(sketch, "E942.MirrorCS", {"start": v(-996.49, 365.42) * mm, "end": v(-992.64, 367.64) * mm});
            skLineSegment(sketch, "E943.MirrorCS", {"start": v(-987.68, 351.44) * mm, "end": v(-984.94, 353.03) * mm});
            skLineSegment(sketch, "E944.MirrorCS", {"start": v(-978.8, 336.04) * mm, "end": v(-976.05, 337.63) * mm});
            skLineSegment(sketch, "E945.MirrorCS", {"start": v(-967.24, 319.2) * mm, "end": v(-967.24, 323.65) * mm});
            skLineSegment(sketch, "E946", {"start": v(-1047.29, 369.87) * mm, "end": v(-1051.14, 367.64) * mm});
            skLineSegment(sketch, "E947.0", {"start": v(-975.4, 321.28) * mm, "end": v(-998.76, 281.09) * mm});
            skLineSegment(sketch, "E947.1", {"start": v(-998.76, 281.09) * mm, "end": v(-1045.26, 281.23) * mm});
            skLineSegment(sketch, "E947.2", {"start": v(-1045.26, 281.23) * mm, "end": v(-1068.39, 321.57) * mm});
            skLineSegment(sketch, "E947.3", {"start": v(-1068.39, 321.57) * mm, "end": v(-1045.01, 361.76) * mm});
            skLineSegment(sketch, "E947.4", {"start": v(-1045.01, 361.76) * mm, "end": v(-998.52, 361.62) * mm});
            skLineSegment(sketch, "E947.5", {"start": v(-998.52, 361.62) * mm, "end": v(-975.4, 321.28) * mm});
            skPoint(sketch, "E947.0.midPoint", {"position": v(-987.08, 301.19) * mm});
            skLineSegment(sketch, "E948", {"start": v(-1047.29, 457.85) * mm, "end": v(-996.49, 457.85) * mm});
            skLineSegment(sketch, "E949", {"start": v(-996.49, 462.3) * mm, "end": v(-996.49, 457.85) * mm});
            skPoint(sketch, "E950.endSnap0", {"position": v(-996.49, 460.08) * mm});
            skLineSegment(sketch, "E951", {"start": v(-1047.29, 460.08) * mm, "end": v(-996.49, 460.08) * mm, "construction": true});
            skLineSegment(sketch, "E952", {"start": v(-1047.29, 462.3) * mm, "end": v(-996.49, 462.3) * mm});
            skLineSegment(sketch, "E953.left", {"start": v(-1000.3, 458.49) * mm, "end": v(-1000.3, 461.66) * mm});
            skLineSegment(sketch, "E953.right", {"start": v(-1043.48, 458.49) * mm, "end": v(-1043.48, 461.66) * mm});
            skPoint(sketch, "E953.middle", {"position": v(-1021.89, 460.08) * mm});
            skLineSegment(sketch, "E954", {"start": v(-1021.89, 461.66) * mm, "end": v(-1021.89, 458.49) * mm, "construction": true});
            skLineSegment(sketch, "E955", {"start": v(-1030.78, 461.66) * mm, "end": v(-1030.78, 458.49) * mm});
            skLineSegment(sketch, "E956.MirrorCS", {"start": v(-1013, 461.66) * mm, "end": v(-1013, 458.49) * mm});
            skLineSegment(sketch, "E957", {"start": v(-1028.24, 461.66) * mm, "end": v(-1028.24, 458.49) * mm});
            skLineSegment(sketch, "E958.MirrorCS", {"start": v(-1015.54, 461.66) * mm, "end": v(-1015.54, 458.49) * mm});
            skLineSegment(sketch, "E959", {"start": v(-1043.48, 461.66) * mm, "end": v(-1030.78, 461.66) * mm});
            skLineSegment(sketch, "E960", {"start": v(-1043.48, 458.49) * mm, "end": v(-1030.78, 458.49) * mm});
            skLineSegment(sketch, "E961", {"start": v(-1028.24, 458.49) * mm, "end": v(-1021.89, 458.49) * mm});
            skLineSegment(sketch, "E962", {"start": v(-1028.24, 461.66) * mm, "end": v(-1021.89, 461.66) * mm});
            skLineSegment(sketch, "E963", {"start": v(-1021.89, 461.66) * mm, "end": v(-1015.54, 461.66) * mm});
            skLineSegment(sketch, "E964", {"start": v(-1021.89, 458.49) * mm, "end": v(-1015.54, 458.49) * mm});
            skLineSegment(sketch, "E965", {"start": v(-1013, 461.66) * mm, "end": v(-1000.3, 461.66) * mm});
            skLineSegment(sketch, "E966", {"start": v(-1013, 458.49) * mm, "end": v(-1000.3, 458.49) * mm});
            skLineSegment(sketch, "E967", {"start": v(-996.49, 457.85) * mm, "end": v(-971.09, 413.86) * mm});
            skLineSegment(sketch, "E968", {"start": v(-992.64, 460.08) * mm, "end": v(-996.49, 457.85) * mm});
            skLineSegment(sketch, "E969", {"start": v(-992.64, 460.08) * mm, "end": v(-967.24, 416.08) * mm});
            skLineSegment(sketch, "E970.left", {"start": v(-972.44, 417.48) * mm, "end": v(-969.7, 419.06) * mm});
            skLineSegment(sketch, "E970.right", {"start": v(-994.03, 454.87) * mm, "end": v(-991.29, 456.46) * mm});
            skPoint(sketch, "E970.middle", {"position": v(-981.87, 436.97) * mm});
            skLineSegment(sketch, "E971", {"start": v(-980.5, 437.76) * mm, "end": v(-983.24, 436.17) * mm, "construction": true});
            skLineSegment(sketch, "E972", {"start": v(-984.94, 445.46) * mm, "end": v(-987.68, 443.87) * mm});
            skLineSegment(sketch, "E973.MirrorCS", {"start": v(-976.05, 430.06) * mm, "end": v(-978.8, 428.48) * mm});
            skLineSegment(sketch, "E974", {"start": v(-983.67, 443.26) * mm, "end": v(-986.41, 441.67) * mm});
            skLineSegment(sketch, "E975.MirrorCS", {"start": v(-977.32, 432.26) * mm, "end": v(-980.06, 430.68) * mm});
            skLineSegment(sketch, "E976", {"start": v(-991.29, 456.46) * mm, "end": v(-984.94, 445.46) * mm});
            skLineSegment(sketch, "E977", {"start": v(-994.03, 454.87) * mm, "end": v(-987.68, 443.87) * mm});
            skLineSegment(sketch, "E978", {"start": v(-986.41, 441.67) * mm, "end": v(-983.24, 436.17) * mm});
            skLineSegment(sketch, "E979", {"start": v(-983.67, 443.26) * mm, "end": v(-980.5, 437.76) * mm});
            skLineSegment(sketch, "E980", {"start": v(-980.5, 437.76) * mm, "end": v(-977.32, 432.26) * mm});
            skLineSegment(sketch, "E981", {"start": v(-983.24, 436.17) * mm, "end": v(-980.06, 430.68) * mm});
            skLineSegment(sketch, "E982", {"start": v(-976.05, 430.06) * mm, "end": v(-969.7, 419.06) * mm});
            skLineSegment(sketch, "E983", {"start": v(-978.8, 428.48) * mm, "end": v(-972.44, 417.48) * mm});
            skPoint(sketch, "E984.endSnap0", {"position": v(-1049.21, 458.97) * mm});
            skLineSegment(sketch, "E985", {"start": v(-971.09, 413.86) * mm, "end": v(-967.24, 416.08) * mm});
            skLineSegment(sketch, "E986.MirrorCS", {"start": v(-980.5, 389.96) * mm, "end": v(-983.24, 391.55) * mm, "construction": true});
            skLineSegment(sketch, "E987.MirrorCS", {"start": v(-1021.89, 366.06) * mm, "end": v(-1021.89, 369.23) * mm, "construction": true});
            skLineSegment(sketch, "E988.MirrorCS", {"start": v(-992.64, 367.64) * mm, "end": v(-996.49, 369.87) * mm});
            skLineSegment(sketch, "E989.MirrorCS", {"start": v(-994.03, 372.85) * mm, "end": v(-991.29, 371.26) * mm});
            skLineSegment(sketch, "E990.MirrorCS", {"start": v(-1015.54, 366.06) * mm, "end": v(-1015.54, 369.23) * mm});
            skLineSegment(sketch, "E991.MirrorCS", {"start": v(-996.49, 365.42) * mm, "end": v(-996.49, 369.87) * mm});
            skLineSegment(sketch, "E992.MirrorCS", {"start": v(-1030.78, 366.06) * mm, "end": v(-1030.78, 369.23) * mm});
            skLineSegment(sketch, "E993.MirrorCS", {"start": v(-984.94, 382.26) * mm, "end": v(-987.68, 383.85) * mm});
            skLineSegment(sketch, "E994.MirrorCS", {"start": v(-1028.24, 366.06) * mm, "end": v(-1028.24, 369.23) * mm});
            skLineSegment(sketch, "E995.MirrorCS", {"start": v(-983.67, 384.46) * mm, "end": v(-986.41, 386.05) * mm});
            skLineSegment(sketch, "E996.MirrorCS", {"start": v(-1013, 366.06) * mm, "end": v(-1013, 369.23) * mm});
            skLineSegment(sketch, "E997.MirrorCS", {"start": v(-972.44, 410.24) * mm, "end": v(-969.7, 408.66) * mm});
            skLineSegment(sketch, "E998.MirrorCS", {"start": v(-1043.48, 369.23) * mm, "end": v(-1043.48, 366.06) * mm});
            skLineSegment(sketch, "E999.MirrorCS", {"start": v(-976.05, 397.66) * mm, "end": v(-978.8, 399.24) * mm});
            skLineSegment(sketch, "E1000.MirrorCS", {"start": v(-971.09, 413.86) * mm, "end": v(-967.24, 411.64) * mm});
            skLineSegment(sketch, "E1001.MirrorCS", {"start": v(-977.32, 395.46) * mm, "end": v(-980.06, 397.04) * mm});
            skLineSegment(sketch, "E1002.MirrorCS", {"start": v(-1000.3, 369.23) * mm, "end": v(-1000.3, 366.06) * mm});
            skLineSegment(sketch, "E1003.MirrorCS", {"start": v(-986.41, 386.05) * mm, "end": v(-983.24, 391.55) * mm});
            skLineSegment(sketch, "E1004.MirrorCS", {"start": v(-980.5, 389.96) * mm, "end": v(-977.32, 395.46) * mm});
            skLineSegment(sketch, "E1005.MirrorCS", {"start": v(-983.24, 391.55) * mm, "end": v(-980.06, 397.04) * mm});
            skLineSegment(sketch, "E1006.MirrorCS", {"start": v(-983.67, 384.46) * mm, "end": v(-980.5, 389.96) * mm});
            skLineSegment(sketch, "E1007.MirrorCS", {"start": v(-978.8, 399.24) * mm, "end": v(-972.44, 410.24) * mm});
            skLineSegment(sketch, "E1008.MirrorCS", {"start": v(-996.49, 369.87) * mm, "end": v(-971.09, 413.86) * mm});
            skLineSegment(sketch, "E1009.MirrorCS", {"start": v(-991.29, 371.26) * mm, "end": v(-984.94, 382.26) * mm});
            skPoint(sketch, "E1010.MirrorP", {"position": v(-981.87, 390.75) * mm});
            skLineSegment(sketch, "E1011.MirrorCS", {"start": v(-976.05, 397.66) * mm, "end": v(-969.7, 408.66) * mm});
            skPoint(sketch, "E1012.MirrorP", {"position": v(-1049.21, 368.75) * mm});
            skLineSegment(sketch, "E1013.MirrorCS", {"start": v(-994.03, 372.85) * mm, "end": v(-987.68, 383.85) * mm});
            skLineSegment(sketch, "E1014.MirrorCS", {"start": v(-992.64, 367.64) * mm, "end": v(-967.24, 411.64) * mm});
            skLineSegment(sketch, "E1015", {"start": v(-967.24, 416.08) * mm, "end": v(-967.24, 411.64) * mm});
            skLineSegment(sketch, "E1016.left", {"start": v(-969.7, 408.66) * mm, "end": v(-972.44, 410.24) * mm});
            skLineSegment(sketch, "E1016.right", {"start": v(-991.29, 371.26) * mm, "end": v(-994.03, 372.85) * mm});
            skLineSegment(sketch, "E1017", {"start": v(-983.24, 391.55) * mm, "end": v(-980.5, 389.96) * mm, "construction": true});
            skLineSegment(sketch, "E1018", {"start": v(-987.68, 383.85) * mm, "end": v(-984.94, 382.26) * mm});
            skLineSegment(sketch, "E1019.MirrorCS", {"start": v(-978.8, 399.24) * mm, "end": v(-976.05, 397.66) * mm});
            skLineSegment(sketch, "E1020", {"start": v(-986.41, 386.05) * mm, "end": v(-983.67, 384.46) * mm});
            skLineSegment(sketch, "E1021.MirrorCS", {"start": v(-980.06, 397.04) * mm, "end": v(-977.32, 395.46) * mm});
            skLineSegment(sketch, "E1022.0", {"start": v(-967.24, 411.64) * mm, "end": v(-971.09, 413.86) * mm, "construction": true});
            skLineSegment(sketch, "E1023", {"start": v(-996.49, 462.3) * mm, "end": v(-992.64, 460.08) * mm});
            skLineSegment(sketch, "E1024.MirrorCS", {"start": v(-983.24, 436.17) * mm, "end": v(-980.5, 437.76) * mm, "construction": true});
            skLineSegment(sketch, "E1025.MirrorCS", {"start": v(-967.24, 416.08) * mm, "end": v(-971.09, 413.86) * mm, "construction": true});
            skLineSegment(sketch, "E1026.MirrorCS", {"start": v(-980.06, 430.68) * mm, "end": v(-977.32, 432.26) * mm});
            skLineSegment(sketch, "E1027.MirrorCS", {"start": v(-969.7, 419.06) * mm, "end": v(-972.44, 417.48) * mm});
            skLineSegment(sketch, "E1028.MirrorCS", {"start": v(-991.29, 456.46) * mm, "end": v(-994.03, 454.87) * mm});
            skLineSegment(sketch, "E1029.MirrorCS", {"start": v(-986.41, 441.67) * mm, "end": v(-983.67, 443.26) * mm});
            skLineSegment(sketch, "E1030.MirrorCS", {"start": v(-996.49, 457.85) * mm, "end": v(-992.64, 460.08) * mm});
            skLineSegment(sketch, "E1031.MirrorCS", {"start": v(-987.68, 443.87) * mm, "end": v(-984.94, 445.46) * mm});
            skLineSegment(sketch, "E1032.MirrorCS", {"start": v(-978.8, 428.48) * mm, "end": v(-976.05, 430.06) * mm});
            skLineSegment(sketch, "E1033.MirrorCS", {"start": v(-967.24, 411.64) * mm, "end": v(-967.24, 416.08) * mm});
            skLineSegment(sketch, "E1034", {"start": v(-1047.29, 462.3) * mm, "end": v(-1051.14, 460.08) * mm});
            skLineSegment(sketch, "E1035.0", {"start": v(-975.4, 413.72) * mm, "end": v(-998.76, 373.52) * mm});
            skLineSegment(sketch, "E1035.1", {"start": v(-998.76, 373.52) * mm, "end": v(-1045.26, 373.66) * mm});
            skLineSegment(sketch, "E1035.2", {"start": v(-1045.26, 373.66) * mm, "end": v(-1068.39, 414) * mm});
            skLineSegment(sketch, "E1035.3", {"start": v(-1068.39, 414) * mm, "end": v(-1045.01, 454.2) * mm});
            skLineSegment(sketch, "E1035.4", {"start": v(-1045.01, 454.2) * mm, "end": v(-998.52, 454.06) * mm});
            skLineSegment(sketch, "E1035.5", {"start": v(-998.52, 454.06) * mm, "end": v(-975.4, 413.72) * mm});
            skPoint(sketch, "E1035.0.midPoint", {"position": v(-987.08, 393.62) * mm});
            skLineSegment(sketch, "E1036", {"start": v(-967.24, 226.77) * mm, "end": v(-916.44, 226.77) * mm});
            skLineSegment(sketch, "E1037", {"start": v(-916.44, 231.22) * mm, "end": v(-916.44, 226.77) * mm});
            skPoint(sketch, "E1038.endSnap0", {"position": v(-916.44, 229) * mm});
            skLineSegment(sketch, "E1039", {"start": v(-967.24, 229) * mm, "end": v(-916.44, 229) * mm, "construction": true});
            skLineSegment(sketch, "E1040", {"start": v(-967.24, 231.22) * mm, "end": v(-916.44, 231.22) * mm});
            skLineSegment(sketch, "E1041.left", {"start": v(-920.25, 227.4) * mm, "end": v(-920.25, 230.58) * mm});
            skLineSegment(sketch, "E1041.right", {"start": v(-963.43, 227.4) * mm, "end": v(-963.43, 230.58) * mm});
            skPoint(sketch, "E1041.middle", {"position": v(-941.84, 229) * mm});
            skLineSegment(sketch, "E1042", {"start": v(-941.84, 230.58) * mm, "end": v(-941.84, 227.4) * mm, "construction": true});
            skLineSegment(sketch, "E1043", {"start": v(-950.73, 230.58) * mm, "end": v(-950.73, 227.4) * mm});
            skLineSegment(sketch, "E1044.MirrorCS", {"start": v(-932.95, 230.58) * mm, "end": v(-932.95, 227.4) * mm});
            skLineSegment(sketch, "E1045", {"start": v(-948.2, 230.58) * mm, "end": v(-948.2, 227.4) * mm});
            skLineSegment(sketch, "E1046.MirrorCS", {"start": v(-935.5, 230.58) * mm, "end": v(-935.5, 227.4) * mm});
            skLineSegment(sketch, "E1047", {"start": v(-963.43, 230.58) * mm, "end": v(-950.73, 230.58) * mm});
            skLineSegment(sketch, "E1048", {"start": v(-963.43, 227.4) * mm, "end": v(-950.73, 227.4) * mm});
            skLineSegment(sketch, "E1049", {"start": v(-948.2, 227.4) * mm, "end": v(-941.84, 227.4) * mm});
            skLineSegment(sketch, "E1050", {"start": v(-948.2, 230.58) * mm, "end": v(-941.84, 230.58) * mm});
            skLineSegment(sketch, "E1051", {"start": v(-941.84, 230.58) * mm, "end": v(-935.5, 230.58) * mm});
            skLineSegment(sketch, "E1052", {"start": v(-941.84, 227.4) * mm, "end": v(-935.5, 227.4) * mm});
            skLineSegment(sketch, "E1053", {"start": v(-932.95, 230.58) * mm, "end": v(-920.25, 230.58) * mm});
            skLineSegment(sketch, "E1054", {"start": v(-932.95, 227.4) * mm, "end": v(-920.25, 227.4) * mm});
            skLineSegment(sketch, "E1055", {"start": v(-912.6, 229) * mm, "end": v(-916.44, 226.77) * mm});
            skPoint(sketch, "E1056.endSnap0", {"position": v(-969.17, 227.88) * mm});
            skLineSegment(sketch, "E1057", {"start": v(-967.24, 319.2) * mm, "end": v(-916.44, 319.2) * mm});
            skLineSegment(sketch, "E1058", {"start": v(-916.44, 323.65) * mm, "end": v(-916.44, 319.2) * mm});
            skPoint(sketch, "E1059.endSnap0", {"position": v(-916.44, 321.43) * mm});
            skLineSegment(sketch, "E1060", {"start": v(-967.24, 321.43) * mm, "end": v(-916.44, 321.43) * mm, "construction": true});
            skLineSegment(sketch, "E1061", {"start": v(-967.24, 323.65) * mm, "end": v(-916.44, 323.65) * mm});
            skLineSegment(sketch, "E1062.left", {"start": v(-920.25, 319.84) * mm, "end": v(-920.25, 323.01) * mm});
            skLineSegment(sketch, "E1062.right", {"start": v(-963.43, 319.84) * mm, "end": v(-963.43, 323.01) * mm});
            skPoint(sketch, "E1062.middle", {"position": v(-941.84, 321.43) * mm});
            skLineSegment(sketch, "E1063", {"start": v(-941.84, 323.01) * mm, "end": v(-941.84, 319.84) * mm, "construction": true});
            skLineSegment(sketch, "E1064", {"start": v(-950.73, 323.01) * mm, "end": v(-950.73, 319.84) * mm});
            skLineSegment(sketch, "E1065.MirrorCS", {"start": v(-932.95, 323.01) * mm, "end": v(-932.95, 319.84) * mm});
            skLineSegment(sketch, "E1066", {"start": v(-948.2, 323.01) * mm, "end": v(-948.2, 319.84) * mm});
            skLineSegment(sketch, "E1067.MirrorCS", {"start": v(-935.5, 323.01) * mm, "end": v(-935.5, 319.84) * mm});
            skLineSegment(sketch, "E1068", {"start": v(-963.43, 323.01) * mm, "end": v(-950.73, 323.01) * mm});
            skLineSegment(sketch, "E1069", {"start": v(-963.43, 319.84) * mm, "end": v(-950.73, 319.84) * mm});
            skLineSegment(sketch, "E1070", {"start": v(-948.2, 319.84) * mm, "end": v(-941.84, 319.84) * mm});
            skLineSegment(sketch, "E1071", {"start": v(-948.2, 323.01) * mm, "end": v(-941.84, 323.01) * mm});
            skLineSegment(sketch, "E1072", {"start": v(-941.84, 323.01) * mm, "end": v(-935.5, 323.01) * mm});
            skLineSegment(sketch, "E1073", {"start": v(-941.84, 319.84) * mm, "end": v(-935.5, 319.84) * mm});
            skLineSegment(sketch, "E1074", {"start": v(-932.95, 323.01) * mm, "end": v(-920.25, 323.01) * mm});
            skLineSegment(sketch, "E1075", {"start": v(-932.95, 319.84) * mm, "end": v(-920.25, 319.84) * mm});
            skLineSegment(sketch, "E1076", {"start": v(-916.44, 319.2) * mm, "end": v(-891.04, 275.21) * mm});
            skLineSegment(sketch, "E1077", {"start": v(-912.6, 321.43) * mm, "end": v(-916.44, 319.2) * mm});
            skLineSegment(sketch, "E1078", {"start": v(-912.6, 321.43) * mm, "end": v(-887.2, 277.43) * mm});
            skLineSegment(sketch, "E1079.left", {"start": v(-892.4, 278.83) * mm, "end": v(-889.65, 280.41) * mm});
            skLineSegment(sketch, "E1079.right", {"start": v(-913.99, 316.22) * mm, "end": v(-911.24, 317.8) * mm});
            skPoint(sketch, "E1079.middle", {"position": v(-901.82, 298.32) * mm});
            skLineSegment(sketch, "E1080", {"start": v(-900.44, 299.11) * mm, "end": v(-903.2, 297.52) * mm, "construction": true});
            skLineSegment(sketch, "E1081", {"start": v(-904.89, 306.81) * mm, "end": v(-907.64, 305.22) * mm});
            skLineSegment(sketch, "E1082.MirrorCS", {"start": v(-896, 291.41) * mm, "end": v(-898.75, 289.83) * mm});
            skLineSegment(sketch, "E1083", {"start": v(-903.62, 304.61) * mm, "end": v(-906.37, 303.02) * mm});
            skLineSegment(sketch, "E1084.MirrorCS", {"start": v(-897.27, 293.61) * mm, "end": v(-900.02, 292.03) * mm});
            skLineSegment(sketch, "E1085", {"start": v(-911.24, 317.8) * mm, "end": v(-904.89, 306.81) * mm});
            skLineSegment(sketch, "E1086", {"start": v(-913.99, 316.22) * mm, "end": v(-907.64, 305.22) * mm});
            skLineSegment(sketch, "E1087", {"start": v(-906.37, 303.02) * mm, "end": v(-903.2, 297.52) * mm});
            skLineSegment(sketch, "E1088", {"start": v(-903.62, 304.61) * mm, "end": v(-900.44, 299.11) * mm});
            skLineSegment(sketch, "E1089", {"start": v(-900.44, 299.11) * mm, "end": v(-897.27, 293.61) * mm});
            skLineSegment(sketch, "E1090", {"start": v(-903.2, 297.52) * mm, "end": v(-900.02, 292.03) * mm});
            skLineSegment(sketch, "E1091", {"start": v(-896, 291.41) * mm, "end": v(-889.65, 280.41) * mm});
            skLineSegment(sketch, "E1092", {"start": v(-898.75, 289.83) * mm, "end": v(-892.4, 278.83) * mm});
            skPoint(sketch, "E1093.endSnap0", {"position": v(-969.17, 320.32) * mm});
            skLineSegment(sketch, "E1094", {"start": v(-891.04, 275.21) * mm, "end": v(-887.2, 277.43) * mm});
            skLineSegment(sketch, "E1095.MirrorCS", {"start": v(-900.44, 251.3) * mm, "end": v(-903.2, 252.9) * mm, "construction": true});
            skLineSegment(sketch, "E1096.MirrorCS", {"start": v(-941.84, 227.4) * mm, "end": v(-941.84, 230.58) * mm, "construction": true});
            skLineSegment(sketch, "E1097.MirrorCS", {"start": v(-912.6, 229) * mm, "end": v(-916.44, 231.22) * mm});
            skLineSegment(sketch, "E1098.MirrorCS", {"start": v(-913.99, 234.2) * mm, "end": v(-911.24, 232.61) * mm});
            skLineSegment(sketch, "E1099.MirrorCS", {"start": v(-935.5, 227.4) * mm, "end": v(-935.5, 230.58) * mm});
            skLineSegment(sketch, "E1100.MirrorCS", {"start": v(-916.44, 226.77) * mm, "end": v(-916.44, 231.22) * mm});
            skLineSegment(sketch, "E1101.MirrorCS", {"start": v(-950.73, 227.4) * mm, "end": v(-950.73, 230.58) * mm});
            skLineSegment(sketch, "E1102.MirrorCS", {"start": v(-904.89, 243.6) * mm, "end": v(-907.64, 245.2) * mm});
            skLineSegment(sketch, "E1103.MirrorCS", {"start": v(-948.2, 227.4) * mm, "end": v(-948.2, 230.58) * mm});
            skLineSegment(sketch, "E1104.MirrorCS", {"start": v(-903.62, 245.8) * mm, "end": v(-906.37, 247.4) * mm});
            skLineSegment(sketch, "E1105.MirrorCS", {"start": v(-932.95, 227.4) * mm, "end": v(-932.95, 230.58) * mm});
            skLineSegment(sketch, "E1106.MirrorCS", {"start": v(-892.4, 271.6) * mm, "end": v(-889.65, 270) * mm});
            skLineSegment(sketch, "E1107.MirrorCS", {"start": v(-963.43, 230.58) * mm, "end": v(-963.43, 227.4) * mm});
            skLineSegment(sketch, "E1108.MirrorCS", {"start": v(-896, 259) * mm, "end": v(-898.75, 260.6) * mm});
            skLineSegment(sketch, "E1109.MirrorCS", {"start": v(-891.04, 275.21) * mm, "end": v(-887.2, 272.99) * mm});
            skLineSegment(sketch, "E1110.MirrorCS", {"start": v(-897.27, 256.8) * mm, "end": v(-900.02, 258.4) * mm});
            skLineSegment(sketch, "E1111.MirrorCS", {"start": v(-920.25, 230.58) * mm, "end": v(-920.25, 227.4) * mm});
            skLineSegment(sketch, "E1112.MirrorCS", {"start": v(-906.37, 247.4) * mm, "end": v(-903.2, 252.9) * mm});
            skLineSegment(sketch, "E1113.MirrorCS", {"start": v(-900.44, 251.3) * mm, "end": v(-897.27, 256.8) * mm});
            skLineSegment(sketch, "E1114.MirrorCS", {"start": v(-903.2, 252.9) * mm, "end": v(-900.02, 258.4) * mm});
            skLineSegment(sketch, "E1115.MirrorCS", {"start": v(-903.62, 245.8) * mm, "end": v(-900.44, 251.3) * mm});
            skLineSegment(sketch, "E1116.MirrorCS", {"start": v(-898.75, 260.6) * mm, "end": v(-892.4, 271.6) * mm});
            skLineSegment(sketch, "E1117.MirrorCS", {"start": v(-916.44, 231.22) * mm, "end": v(-891.04, 275.21) * mm});
            skLineSegment(sketch, "E1118.MirrorCS", {"start": v(-911.24, 232.61) * mm, "end": v(-904.89, 243.6) * mm});
            skPoint(sketch, "E1119.MirrorP", {"position": v(-901.82, 252.1) * mm});
            skLineSegment(sketch, "E1120.MirrorCS", {"start": v(-896, 259) * mm, "end": v(-889.65, 270) * mm});
            skPoint(sketch, "E1121.MirrorP", {"position": v(-969.17, 230.1) * mm});
            skLineSegment(sketch, "E1122.MirrorCS", {"start": v(-913.99, 234.2) * mm, "end": v(-907.64, 245.2) * mm});
            skLineSegment(sketch, "E1123.MirrorCS", {"start": v(-912.6, 229) * mm, "end": v(-887.2, 272.99) * mm});
            skLineSegment(sketch, "E1124", {"start": v(-887.2, 277.43) * mm, "end": v(-887.2, 272.99) * mm});
            skLineSegment(sketch, "E1125", {"start": v(-916.44, 231.22) * mm, "end": v(-912.6, 229) * mm});
            skLineSegment(sketch, "E1126.left", {"start": v(-889.65, 270) * mm, "end": v(-892.4, 271.6) * mm});
            skLineSegment(sketch, "E1126.right", {"start": v(-911.24, 232.61) * mm, "end": v(-913.99, 234.2) * mm});
            skLineSegment(sketch, "E1127", {"start": v(-903.2, 252.9) * mm, "end": v(-900.44, 251.3) * mm, "construction": true});
            skLineSegment(sketch, "E1128", {"start": v(-907.64, 245.2) * mm, "end": v(-904.89, 243.6) * mm});
            skLineSegment(sketch, "E1129.MirrorCS", {"start": v(-898.75, 260.6) * mm, "end": v(-896, 259) * mm});
            skLineSegment(sketch, "E1130", {"start": v(-906.37, 247.4) * mm, "end": v(-903.62, 245.8) * mm});
            skLineSegment(sketch, "E1131.MirrorCS", {"start": v(-900.02, 258.4) * mm, "end": v(-897.27, 256.8) * mm});
            skLineSegment(sketch, "E1132.0", {"start": v(-887.2, 272.99) * mm, "end": v(-891.04, 275.21) * mm, "construction": true});
            skLineSegment(sketch, "E1133.MirrorCS", {"start": v(-916.44, 226.77) * mm, "end": v(-912.6, 229) * mm});
            skLineSegment(sketch, "E1134", {"start": v(-916.44, 323.65) * mm, "end": v(-912.6, 321.43) * mm});
            skLineSegment(sketch, "E1135.MirrorCS", {"start": v(-903.2, 297.52) * mm, "end": v(-900.44, 299.11) * mm, "construction": true});
            skLineSegment(sketch, "E1136.MirrorCS", {"start": v(-887.2, 277.43) * mm, "end": v(-891.04, 275.21) * mm, "construction": true});
            skLineSegment(sketch, "E1137.MirrorCS", {"start": v(-900.02, 292.03) * mm, "end": v(-897.27, 293.61) * mm});
            skLineSegment(sketch, "E1138.MirrorCS", {"start": v(-889.65, 280.41) * mm, "end": v(-892.4, 278.83) * mm});
            skLineSegment(sketch, "E1139.MirrorCS", {"start": v(-911.24, 317.8) * mm, "end": v(-913.99, 316.22) * mm});
            skLineSegment(sketch, "E1140.MirrorCS", {"start": v(-906.37, 303.02) * mm, "end": v(-903.62, 304.61) * mm});
            skLineSegment(sketch, "E1141.MirrorCS", {"start": v(-916.44, 319.2) * mm, "end": v(-912.6, 321.43) * mm});
            skLineSegment(sketch, "E1142.MirrorCS", {"start": v(-907.64, 305.22) * mm, "end": v(-904.89, 306.81) * mm});
            skLineSegment(sketch, "E1143.MirrorCS", {"start": v(-898.75, 289.83) * mm, "end": v(-896, 291.41) * mm});
            skLineSegment(sketch, "E1144.MirrorCS", {"start": v(-887.2, 272.99) * mm, "end": v(-887.2, 277.43) * mm});
            skLineSegment(sketch, "E1145", {"start": v(-967.24, 323.65) * mm, "end": v(-971.09, 321.43) * mm});
            skLineSegment(sketch, "E1146.0", {"start": v(-895.34, 275.07) * mm, "end": v(-918.72, 234.87) * mm});
            skLineSegment(sketch, "E1146.1", {"start": v(-918.72, 234.87) * mm, "end": v(-965.21, 235.01) * mm});
            skLineSegment(sketch, "E1146.2", {"start": v(-965.21, 235.01) * mm, "end": v(-988.34, 275.35) * mm});
            skLineSegment(sketch, "E1146.3", {"start": v(-988.34, 275.35) * mm, "end": v(-964.97, 315.55) * mm});
            skLineSegment(sketch, "E1146.4", {"start": v(-964.97, 315.55) * mm, "end": v(-918.47, 315.4) * mm});
            skLineSegment(sketch, "E1146.5", {"start": v(-918.47, 315.4) * mm, "end": v(-895.34, 275.07) * mm});
            skPoint(sketch, "E1146.0.midPoint", {"position": v(-907.03, 254.97) * mm});
            skLineSegment(sketch, "E1147", {"start": v(-967.24, 411.64) * mm, "end": v(-916.44, 411.64) * mm});
            skLineSegment(sketch, "E1148", {"start": v(-916.44, 416.08) * mm, "end": v(-916.44, 411.64) * mm});
            skPoint(sketch, "E1149.endSnap0", {"position": v(-916.44, 413.86) * mm});
            skLineSegment(sketch, "E1150", {"start": v(-967.24, 413.86) * mm, "end": v(-916.44, 413.86) * mm, "construction": true});
            skLineSegment(sketch, "E1151", {"start": v(-967.24, 416.08) * mm, "end": v(-916.44, 416.08) * mm});
            skLineSegment(sketch, "E1152.left", {"start": v(-920.25, 412.27) * mm, "end": v(-920.25, 415.45) * mm});
            skLineSegment(sketch, "E1152.right", {"start": v(-963.43, 412.27) * mm, "end": v(-963.43, 415.45) * mm});
            skPoint(sketch, "E1152.middle", {"position": v(-941.84, 413.86) * mm});
            skLineSegment(sketch, "E1153", {"start": v(-941.84, 415.45) * mm, "end": v(-941.84, 412.27) * mm, "construction": true});
            skLineSegment(sketch, "E1154", {"start": v(-950.73, 415.45) * mm, "end": v(-950.73, 412.27) * mm});
            skLineSegment(sketch, "E1155.MirrorCS", {"start": v(-932.95, 415.45) * mm, "end": v(-932.95, 412.27) * mm});
            skLineSegment(sketch, "E1156", {"start": v(-948.2, 415.45) * mm, "end": v(-948.2, 412.27) * mm});
            skLineSegment(sketch, "E1157.MirrorCS", {"start": v(-935.5, 415.45) * mm, "end": v(-935.5, 412.27) * mm});
            skLineSegment(sketch, "E1158", {"start": v(-963.43, 415.45) * mm, "end": v(-950.73, 415.45) * mm});
            skLineSegment(sketch, "E1159", {"start": v(-963.43, 412.27) * mm, "end": v(-950.73, 412.27) * mm});
            skLineSegment(sketch, "E1160", {"start": v(-948.2, 412.27) * mm, "end": v(-941.84, 412.27) * mm});
            skLineSegment(sketch, "E1161", {"start": v(-948.2, 415.45) * mm, "end": v(-941.84, 415.45) * mm});
            skLineSegment(sketch, "E1162", {"start": v(-941.84, 415.45) * mm, "end": v(-935.5, 415.45) * mm});
            skLineSegment(sketch, "E1163", {"start": v(-941.84, 412.27) * mm, "end": v(-935.5, 412.27) * mm});
            skLineSegment(sketch, "E1164", {"start": v(-932.95, 415.45) * mm, "end": v(-920.25, 415.45) * mm});
            skLineSegment(sketch, "E1165", {"start": v(-932.95, 412.27) * mm, "end": v(-920.25, 412.27) * mm});
            skLineSegment(sketch, "E1166", {"start": v(-916.44, 411.64) * mm, "end": v(-891.04, 367.64) * mm});
            skLineSegment(sketch, "E1167", {"start": v(-912.6, 413.86) * mm, "end": v(-916.44, 411.64) * mm});
            skLineSegment(sketch, "E1168", {"start": v(-912.6, 413.86) * mm, "end": v(-887.2, 369.87) * mm});
            skLineSegment(sketch, "E1169.left", {"start": v(-892.4, 371.26) * mm, "end": v(-889.65, 372.85) * mm});
            skLineSegment(sketch, "E1169.right", {"start": v(-913.99, 408.66) * mm, "end": v(-911.24, 410.24) * mm});
            skPoint(sketch, "E1169.middle", {"position": v(-901.82, 390.75) * mm});
            skLineSegment(sketch, "E1170", {"start": v(-900.44, 391.55) * mm, "end": v(-903.2, 389.96) * mm, "construction": true});
            skLineSegment(sketch, "E1171", {"start": v(-904.89, 399.24) * mm, "end": v(-907.64, 397.66) * mm});
            skLineSegment(sketch, "E1172.MirrorCS", {"start": v(-896, 383.85) * mm, "end": v(-898.75, 382.26) * mm});
            skLineSegment(sketch, "E1173", {"start": v(-903.62, 397.04) * mm, "end": v(-906.37, 395.46) * mm});
            skLineSegment(sketch, "E1174.MirrorCS", {"start": v(-897.27, 386.05) * mm, "end": v(-900.02, 384.46) * mm});
            skLineSegment(sketch, "E1175", {"start": v(-911.24, 410.24) * mm, "end": v(-904.89, 399.24) * mm});
            skLineSegment(sketch, "E1176", {"start": v(-913.99, 408.66) * mm, "end": v(-907.64, 397.66) * mm});
            skLineSegment(sketch, "E1177", {"start": v(-906.37, 395.46) * mm, "end": v(-903.2, 389.96) * mm});
            skLineSegment(sketch, "E1178", {"start": v(-903.62, 397.04) * mm, "end": v(-900.44, 391.55) * mm});
            skLineSegment(sketch, "E1179", {"start": v(-900.44, 391.55) * mm, "end": v(-897.27, 386.05) * mm});
            skLineSegment(sketch, "E1180", {"start": v(-903.2, 389.96) * mm, "end": v(-900.02, 384.46) * mm});
            skLineSegment(sketch, "E1181", {"start": v(-896, 383.85) * mm, "end": v(-889.65, 372.85) * mm});
            skLineSegment(sketch, "E1182", {"start": v(-898.75, 382.26) * mm, "end": v(-892.4, 371.26) * mm});
            skPoint(sketch, "E1183.endSnap0", {"position": v(-969.17, 412.75) * mm});
            skLineSegment(sketch, "E1184", {"start": v(-891.04, 367.64) * mm, "end": v(-887.2, 369.87) * mm});
            skLineSegment(sketch, "E1185.MirrorCS", {"start": v(-900.44, 343.74) * mm, "end": v(-903.2, 345.33) * mm, "construction": true});
            skLineSegment(sketch, "E1186.MirrorCS", {"start": v(-941.84, 319.84) * mm, "end": v(-941.84, 323.01) * mm, "construction": true});
            skLineSegment(sketch, "E1187.MirrorCS", {"start": v(-912.6, 321.43) * mm, "end": v(-916.44, 323.65) * mm});
            skLineSegment(sketch, "E1188.MirrorCS", {"start": v(-913.99, 326.63) * mm, "end": v(-911.24, 325.04) * mm});
            skLineSegment(sketch, "E1189.MirrorCS", {"start": v(-935.5, 319.84) * mm, "end": v(-935.5, 323.01) * mm});
            skLineSegment(sketch, "E1190.MirrorCS", {"start": v(-916.44, 319.2) * mm, "end": v(-916.44, 323.65) * mm});
            skLineSegment(sketch, "E1191.MirrorCS", {"start": v(-950.73, 319.84) * mm, "end": v(-950.73, 323.01) * mm});
            skLineSegment(sketch, "E1192.MirrorCS", {"start": v(-904.89, 336.04) * mm, "end": v(-907.64, 337.63) * mm});
            skLineSegment(sketch, "E1193.MirrorCS", {"start": v(-948.2, 319.84) * mm, "end": v(-948.2, 323.01) * mm});
            skLineSegment(sketch, "E1194.MirrorCS", {"start": v(-903.62, 338.24) * mm, "end": v(-906.37, 339.83) * mm});
            skLineSegment(sketch, "E1195.MirrorCS", {"start": v(-932.95, 319.84) * mm, "end": v(-932.95, 323.01) * mm});
            skLineSegment(sketch, "E1196.MirrorCS", {"start": v(-892.4, 364.03) * mm, "end": v(-889.65, 362.44) * mm});
            skLineSegment(sketch, "E1197.MirrorCS", {"start": v(-963.43, 323.01) * mm, "end": v(-963.43, 319.84) * mm});
            skLineSegment(sketch, "E1198.MirrorCS", {"start": v(-896, 351.44) * mm, "end": v(-898.75, 353.03) * mm});
            skLineSegment(sketch, "E1199.MirrorCS", {"start": v(-891.04, 367.64) * mm, "end": v(-887.2, 365.42) * mm});
            skLineSegment(sketch, "E1200.MirrorCS", {"start": v(-897.27, 349.24) * mm, "end": v(-900.02, 350.83) * mm});
            skLineSegment(sketch, "E1201.MirrorCS", {"start": v(-920.25, 323.01) * mm, "end": v(-920.25, 319.84) * mm});
            skLineSegment(sketch, "E1202.MirrorCS", {"start": v(-906.37, 339.83) * mm, "end": v(-903.2, 345.33) * mm});
            skLineSegment(sketch, "E1203.MirrorCS", {"start": v(-900.44, 343.74) * mm, "end": v(-897.27, 349.24) * mm});
            skLineSegment(sketch, "E1204.MirrorCS", {"start": v(-903.2, 345.33) * mm, "end": v(-900.02, 350.83) * mm});
            skLineSegment(sketch, "E1205.MirrorCS", {"start": v(-903.62, 338.24) * mm, "end": v(-900.44, 343.74) * mm});
            skLineSegment(sketch, "E1206.MirrorCS", {"start": v(-898.75, 353.03) * mm, "end": v(-892.4, 364.03) * mm});
            skLineSegment(sketch, "E1207.MirrorCS", {"start": v(-916.44, 323.65) * mm, "end": v(-891.04, 367.64) * mm});
            skLineSegment(sketch, "E1208.MirrorCS", {"start": v(-911.24, 325.04) * mm, "end": v(-904.89, 336.04) * mm});
            skPoint(sketch, "E1209.MirrorP", {"position": v(-901.82, 344.53) * mm});
            skLineSegment(sketch, "E1210.MirrorCS", {"start": v(-896, 351.44) * mm, "end": v(-889.65, 362.44) * mm});
            skPoint(sketch, "E1211.MirrorP", {"position": v(-969.17, 322.54) * mm});
            skLineSegment(sketch, "E1212.MirrorCS", {"start": v(-913.99, 326.63) * mm, "end": v(-907.64, 337.63) * mm});
            skLineSegment(sketch, "E1213.MirrorCS", {"start": v(-912.6, 321.43) * mm, "end": v(-887.2, 365.42) * mm});
            skLineSegment(sketch, "E1214", {"start": v(-887.2, 369.87) * mm, "end": v(-887.2, 365.42) * mm});
            skLineSegment(sketch, "E1215.left", {"start": v(-889.65, 362.44) * mm, "end": v(-892.4, 364.03) * mm});
            skLineSegment(sketch, "E1215.right", {"start": v(-911.24, 325.04) * mm, "end": v(-913.99, 326.63) * mm});
            skLineSegment(sketch, "E1216", {"start": v(-903.2, 345.33) * mm, "end": v(-900.44, 343.74) * mm, "construction": true});
            skLineSegment(sketch, "E1217", {"start": v(-907.64, 337.63) * mm, "end": v(-904.89, 336.04) * mm});
            skLineSegment(sketch, "E1218.MirrorCS", {"start": v(-898.75, 353.03) * mm, "end": v(-896, 351.44) * mm});
            skLineSegment(sketch, "E1219", {"start": v(-906.37, 339.83) * mm, "end": v(-903.62, 338.24) * mm});
            skLineSegment(sketch, "E1220.MirrorCS", {"start": v(-900.02, 350.83) * mm, "end": v(-897.27, 349.24) * mm});
            skLineSegment(sketch, "E1221.0", {"start": v(-887.2, 365.42) * mm, "end": v(-891.04, 367.64) * mm, "construction": true});
            skLineSegment(sketch, "E1222", {"start": v(-916.44, 416.08) * mm, "end": v(-912.6, 413.86) * mm});
            skLineSegment(sketch, "E1223.MirrorCS", {"start": v(-903.2, 389.96) * mm, "end": v(-900.44, 391.55) * mm, "construction": true});
            skLineSegment(sketch, "E1224.MirrorCS", {"start": v(-887.2, 369.87) * mm, "end": v(-891.04, 367.64) * mm, "construction": true});
            skLineSegment(sketch, "E1225.MirrorCS", {"start": v(-900.02, 384.46) * mm, "end": v(-897.27, 386.05) * mm});
            skLineSegment(sketch, "E1226.MirrorCS", {"start": v(-889.65, 372.85) * mm, "end": v(-892.4, 371.26) * mm});
            skLineSegment(sketch, "E1227.MirrorCS", {"start": v(-911.24, 410.24) * mm, "end": v(-913.99, 408.66) * mm});
            skLineSegment(sketch, "E1228.MirrorCS", {"start": v(-906.37, 395.46) * mm, "end": v(-903.62, 397.04) * mm});
            skLineSegment(sketch, "E1229.MirrorCS", {"start": v(-916.44, 411.64) * mm, "end": v(-912.6, 413.86) * mm});
            skLineSegment(sketch, "E1230.MirrorCS", {"start": v(-907.64, 397.66) * mm, "end": v(-904.89, 399.24) * mm});
            skLineSegment(sketch, "E1231.MirrorCS", {"start": v(-898.75, 382.26) * mm, "end": v(-896, 383.85) * mm});
            skLineSegment(sketch, "E1232.MirrorCS", {"start": v(-887.2, 365.42) * mm, "end": v(-887.2, 369.87) * mm});
            skLineSegment(sketch, "E1233", {"start": v(-967.24, 416.08) * mm, "end": v(-971.09, 413.86) * mm});
            skLineSegment(sketch, "E1234.0", {"start": v(-895.34, 367.5) * mm, "end": v(-918.72, 327.3) * mm});
            skLineSegment(sketch, "E1234.1", {"start": v(-918.72, 327.3) * mm, "end": v(-965.21, 327.45) * mm});
            skLineSegment(sketch, "E1234.2", {"start": v(-965.21, 327.45) * mm, "end": v(-988.34, 367.79) * mm});
            skLineSegment(sketch, "E1234.3", {"start": v(-988.34, 367.79) * mm, "end": v(-964.97, 407.98) * mm});
            skLineSegment(sketch, "E1234.4", {"start": v(-964.97, 407.98) * mm, "end": v(-918.47, 407.84) * mm});
            skLineSegment(sketch, "E1234.5", {"start": v(-918.47, 407.84) * mm, "end": v(-895.34, 367.5) * mm});
            skPoint(sketch, "E1234.0.midPoint", {"position": v(-907.03, 347.4) * mm});
            skLineSegment(sketch, "E1235", {"start": v(-967.24, 504.07) * mm, "end": v(-916.44, 504.07) * mm});
            skLineSegment(sketch, "E1236", {"start": v(-967.24, 508.52) * mm, "end": v(-967.24, 504.07) * mm});
            skLineSegment(sketch, "E1237", {"start": v(-916.44, 508.52) * mm, "end": v(-916.44, 504.07) * mm});
            skPoint(sketch, "E1238.endSnap0", {"position": v(-916.44, 506.3) * mm});
            skLineSegment(sketch, "E1239", {"start": v(-967.24, 506.3) * mm, "end": v(-916.44, 506.3) * mm, "construction": true});
            skLineSegment(sketch, "E1240", {"start": v(-967.24, 508.52) * mm, "end": v(-916.44, 508.52) * mm});
            skLineSegment(sketch, "E1241.left", {"start": v(-920.25, 504.7) * mm, "end": v(-920.25, 507.88) * mm});
            skLineSegment(sketch, "E1241.right", {"start": v(-963.43, 504.7) * mm, "end": v(-963.43, 507.88) * mm});
            skPoint(sketch, "E1241.middle", {"position": v(-941.84, 506.3) * mm});
            skLineSegment(sketch, "E1242", {"start": v(-941.84, 507.88) * mm, "end": v(-941.84, 504.7) * mm, "construction": true});
            skLineSegment(sketch, "E1243", {"start": v(-950.73, 507.88) * mm, "end": v(-950.73, 504.7) * mm});
            skLineSegment(sketch, "E1244.MirrorCS", {"start": v(-932.95, 507.88) * mm, "end": v(-932.95, 504.7) * mm});
            skLineSegment(sketch, "E1245", {"start": v(-948.2, 507.88) * mm, "end": v(-948.2, 504.7) * mm});
            skLineSegment(sketch, "E1246.MirrorCS", {"start": v(-935.5, 507.88) * mm, "end": v(-935.5, 504.7) * mm});
            skLineSegment(sketch, "E1247", {"start": v(-963.43, 507.88) * mm, "end": v(-950.73, 507.88) * mm});
            skLineSegment(sketch, "E1248", {"start": v(-963.43, 504.7) * mm, "end": v(-950.73, 504.7) * mm});
            skLineSegment(sketch, "E1249", {"start": v(-948.2, 504.7) * mm, "end": v(-941.84, 504.7) * mm});
            skLineSegment(sketch, "E1250", {"start": v(-948.2, 507.88) * mm, "end": v(-941.84, 507.88) * mm});
            skLineSegment(sketch, "E1251", {"start": v(-941.84, 507.88) * mm, "end": v(-935.5, 507.88) * mm});
            skLineSegment(sketch, "E1252", {"start": v(-941.84, 504.7) * mm, "end": v(-935.5, 504.7) * mm});
            skLineSegment(sketch, "E1253", {"start": v(-932.95, 507.88) * mm, "end": v(-920.25, 507.88) * mm});
            skLineSegment(sketch, "E1254", {"start": v(-932.95, 504.7) * mm, "end": v(-920.25, 504.7) * mm});
            skLineSegment(sketch, "E1255", {"start": v(-916.44, 504.07) * mm, "end": v(-891.04, 460.08) * mm});
            skLineSegment(sketch, "E1256", {"start": v(-912.6, 506.3) * mm, "end": v(-916.44, 504.07) * mm});
            skLineSegment(sketch, "E1257", {"start": v(-912.6, 506.3) * mm, "end": v(-887.2, 462.3) * mm});
            skLineSegment(sketch, "E1258.left", {"start": v(-892.4, 463.7) * mm, "end": v(-889.65, 465.28) * mm});
            skLineSegment(sketch, "E1258.right", {"start": v(-913.99, 501.09) * mm, "end": v(-911.24, 502.68) * mm});
            skPoint(sketch, "E1258.middle", {"position": v(-901.82, 483.18) * mm});
            skLineSegment(sketch, "E1259", {"start": v(-900.44, 483.98) * mm, "end": v(-903.2, 482.4) * mm, "construction": true});
            skLineSegment(sketch, "E1260", {"start": v(-904.89, 491.68) * mm, "end": v(-907.64, 490.09) * mm});
            skLineSegment(sketch, "E1261.MirrorCS", {"start": v(-896, 476.28) * mm, "end": v(-898.75, 474.7) * mm});
            skLineSegment(sketch, "E1262", {"start": v(-903.62, 489.48) * mm, "end": v(-906.37, 487.9) * mm});
            skLineSegment(sketch, "E1263.MirrorCS", {"start": v(-897.27, 478.48) * mm, "end": v(-900.02, 476.9) * mm});
            skLineSegment(sketch, "E1264", {"start": v(-911.24, 502.68) * mm, "end": v(-904.89, 491.68) * mm});
            skLineSegment(sketch, "E1265", {"start": v(-913.99, 501.09) * mm, "end": v(-907.64, 490.09) * mm});
            skLineSegment(sketch, "E1266", {"start": v(-906.37, 487.9) * mm, "end": v(-903.2, 482.4) * mm});
            skLineSegment(sketch, "E1267", {"start": v(-903.62, 489.48) * mm, "end": v(-900.44, 483.98) * mm});
            skLineSegment(sketch, "E1268", {"start": v(-900.44, 483.98) * mm, "end": v(-897.27, 478.48) * mm});
            skLineSegment(sketch, "E1269", {"start": v(-903.2, 482.4) * mm, "end": v(-900.02, 476.9) * mm});
            skLineSegment(sketch, "E1270", {"start": v(-896, 476.28) * mm, "end": v(-889.65, 465.28) * mm});
            skLineSegment(sketch, "E1271", {"start": v(-898.75, 474.7) * mm, "end": v(-892.4, 463.7) * mm});
            skLineSegment(sketch, "E1272", {"start": v(-992.64, 460.08) * mm, "end": v(-967.24, 504.07) * mm});
            skLineSegment(sketch, "E1273", {"start": v(-971.09, 506.3) * mm, "end": v(-967.24, 504.07) * mm});
            skPoint(sketch, "E1274.endSnap0", {"position": v(-969.17, 505.18) * mm});
            skLineSegment(sketch, "E1275", {"start": v(-996.49, 462.3) * mm, "end": v(-971.09, 506.3) * mm});
            skLineSegment(sketch, "E1276.left", {"start": v(-969.7, 501.09) * mm, "end": v(-972.44, 502.68) * mm});
            skLineSegment(sketch, "E1276.right", {"start": v(-991.29, 463.7) * mm, "end": v(-994.03, 465.28) * mm});
            skPoint(sketch, "E1276.middle", {"position": v(-981.87, 483.18) * mm});
            skLineSegment(sketch, "E1277", {"start": v(-983.24, 483.98) * mm, "end": v(-980.5, 482.4) * mm, "construction": true});
            skLineSegment(sketch, "E1278", {"start": v(-987.68, 476.28) * mm, "end": v(-984.94, 474.7) * mm});
            skLineSegment(sketch, "E1279.MirrorCS", {"start": v(-978.8, 491.68) * mm, "end": v(-976.05, 490.09) * mm});
            skLineSegment(sketch, "E1280", {"start": v(-986.41, 478.48) * mm, "end": v(-983.67, 476.9) * mm});
            skLineSegment(sketch, "E1281.MirrorCS", {"start": v(-980.06, 489.48) * mm, "end": v(-977.32, 487.9) * mm});
            skLineSegment(sketch, "E1282", {"start": v(-994.03, 465.28) * mm, "end": v(-987.68, 476.28) * mm});
            skLineSegment(sketch, "E1283", {"start": v(-991.29, 463.7) * mm, "end": v(-984.94, 474.7) * mm});
            skLineSegment(sketch, "E1284", {"start": v(-983.67, 476.9) * mm, "end": v(-980.5, 482.4) * mm});
            skLineSegment(sketch, "E1285", {"start": v(-986.41, 478.48) * mm, "end": v(-983.24, 483.98) * mm});
            skLineSegment(sketch, "E1286", {"start": v(-983.24, 483.98) * mm, "end": v(-980.06, 489.48) * mm});
            skLineSegment(sketch, "E1287", {"start": v(-980.5, 482.4) * mm, "end": v(-977.32, 487.9) * mm});
            skLineSegment(sketch, "E1288", {"start": v(-978.8, 491.68) * mm, "end": v(-972.44, 502.68) * mm});
            skLineSegment(sketch, "E1289", {"start": v(-976.05, 490.09) * mm, "end": v(-969.7, 501.09) * mm});
            skLineSegment(sketch, "E1290.0", {"start": v(-967.24, 504.07) * mm, "end": v(-971.09, 506.3) * mm, "construction": true});
            skLineSegment(sketch, "E1291", {"start": v(-891.04, 460.08) * mm, "end": v(-887.2, 462.3) * mm});
            skLineSegment(sketch, "E1292.MirrorCS", {"start": v(-900.44, 436.17) * mm, "end": v(-903.2, 437.76) * mm, "construction": true});
            skLineSegment(sketch, "E1293.MirrorCS", {"start": v(-941.84, 412.27) * mm, "end": v(-941.84, 415.45) * mm, "construction": true});
            skLineSegment(sketch, "E1294.MirrorCS", {"start": v(-912.6, 413.86) * mm, "end": v(-916.44, 416.08) * mm});
            skLineSegment(sketch, "E1295.MirrorCS", {"start": v(-913.99, 419.06) * mm, "end": v(-911.24, 417.48) * mm});
            skLineSegment(sketch, "E1296.MirrorCS", {"start": v(-935.5, 412.27) * mm, "end": v(-935.5, 415.45) * mm});
            skLineSegment(sketch, "E1297.MirrorCS", {"start": v(-916.44, 411.64) * mm, "end": v(-916.44, 416.08) * mm});
            skLineSegment(sketch, "E1298.MirrorCS", {"start": v(-950.73, 412.27) * mm, "end": v(-950.73, 415.45) * mm});
            skLineSegment(sketch, "E1299.MirrorCS", {"start": v(-904.89, 428.48) * mm, "end": v(-907.64, 430.06) * mm});
            skLineSegment(sketch, "E1300.MirrorCS", {"start": v(-948.2, 412.27) * mm, "end": v(-948.2, 415.45) * mm});
            skLineSegment(sketch, "E1301.MirrorCS", {"start": v(-903.62, 430.68) * mm, "end": v(-906.37, 432.26) * mm});
            skLineSegment(sketch, "E1302.MirrorCS", {"start": v(-932.95, 412.27) * mm, "end": v(-932.95, 415.45) * mm});
            skLineSegment(sketch, "E1303.MirrorCS", {"start": v(-892.4, 456.46) * mm, "end": v(-889.65, 454.87) * mm});
            skLineSegment(sketch, "E1304.MirrorCS", {"start": v(-963.43, 415.45) * mm, "end": v(-963.43, 412.27) * mm});
            skLineSegment(sketch, "E1305.MirrorCS", {"start": v(-896, 443.87) * mm, "end": v(-898.75, 445.46) * mm});
            skLineSegment(sketch, "E1306.MirrorCS", {"start": v(-891.04, 460.08) * mm, "end": v(-887.2, 457.85) * mm});
            skLineSegment(sketch, "E1307.MirrorCS", {"start": v(-897.27, 441.67) * mm, "end": v(-900.02, 443.26) * mm});
            skLineSegment(sketch, "E1308.MirrorCS", {"start": v(-920.25, 415.45) * mm, "end": v(-920.25, 412.27) * mm});
            skLineSegment(sketch, "E1309.MirrorCS", {"start": v(-906.37, 432.26) * mm, "end": v(-903.2, 437.76) * mm});
            skLineSegment(sketch, "E1310.MirrorCS", {"start": v(-900.44, 436.17) * mm, "end": v(-897.27, 441.67) * mm});
            skLineSegment(sketch, "E1311.MirrorCS", {"start": v(-903.2, 437.76) * mm, "end": v(-900.02, 443.26) * mm});
            skLineSegment(sketch, "E1312.MirrorCS", {"start": v(-903.62, 430.68) * mm, "end": v(-900.44, 436.17) * mm});
            skLineSegment(sketch, "E1313.MirrorCS", {"start": v(-898.75, 445.46) * mm, "end": v(-892.4, 456.46) * mm});
            skLineSegment(sketch, "E1314.MirrorCS", {"start": v(-916.44, 416.08) * mm, "end": v(-891.04, 460.08) * mm});
            skLineSegment(sketch, "E1315.MirrorCS", {"start": v(-911.24, 417.48) * mm, "end": v(-904.89, 428.48) * mm});
            skPoint(sketch, "E1316.MirrorP", {"position": v(-901.82, 436.97) * mm});
            skLineSegment(sketch, "E1317.MirrorCS", {"start": v(-896, 443.87) * mm, "end": v(-889.65, 454.87) * mm});
            skPoint(sketch, "E1318.MirrorP", {"position": v(-969.17, 414.97) * mm});
            skLineSegment(sketch, "E1319.MirrorCS", {"start": v(-913.99, 419.06) * mm, "end": v(-907.64, 430.06) * mm});
            skLineSegment(sketch, "E1320.MirrorCS", {"start": v(-912.6, 413.86) * mm, "end": v(-887.2, 457.85) * mm});
            skLineSegment(sketch, "E1321", {"start": v(-887.2, 462.3) * mm, "end": v(-887.2, 457.85) * mm});
            skLineSegment(sketch, "E1322.left", {"start": v(-889.65, 454.87) * mm, "end": v(-892.4, 456.46) * mm});
            skLineSegment(sketch, "E1322.right", {"start": v(-911.24, 417.48) * mm, "end": v(-913.99, 419.06) * mm});
            skLineSegment(sketch, "E1323", {"start": v(-903.2, 437.76) * mm, "end": v(-900.44, 436.17) * mm, "construction": true});
            skLineSegment(sketch, "E1324", {"start": v(-907.64, 430.06) * mm, "end": v(-904.89, 428.48) * mm});
            skLineSegment(sketch, "E1325.MirrorCS", {"start": v(-898.75, 445.46) * mm, "end": v(-896, 443.87) * mm});
            skLineSegment(sketch, "E1326", {"start": v(-906.37, 432.26) * mm, "end": v(-903.62, 430.68) * mm});
            skLineSegment(sketch, "E1327.MirrorCS", {"start": v(-900.02, 443.26) * mm, "end": v(-897.27, 441.67) * mm});
            skLineSegment(sketch, "E1328.0", {"start": v(-887.2, 457.85) * mm, "end": v(-891.04, 460.08) * mm, "construction": true});
            skLineSegment(sketch, "E1329", {"start": v(-916.44, 508.52) * mm, "end": v(-912.6, 506.3) * mm});
            skLineSegment(sketch, "E1330.MirrorCS", {"start": v(-903.2, 482.4) * mm, "end": v(-900.44, 483.98) * mm, "construction": true});
            skLineSegment(sketch, "E1331.MirrorCS", {"start": v(-887.2, 462.3) * mm, "end": v(-891.04, 460.08) * mm, "construction": true});
            skLineSegment(sketch, "E1332.MirrorCS", {"start": v(-900.02, 476.9) * mm, "end": v(-897.27, 478.48) * mm});
            skLineSegment(sketch, "E1333.MirrorCS", {"start": v(-889.65, 465.28) * mm, "end": v(-892.4, 463.7) * mm});
            skLineSegment(sketch, "E1334.MirrorCS", {"start": v(-911.24, 502.68) * mm, "end": v(-913.99, 501.09) * mm});
            skLineSegment(sketch, "E1335.MirrorCS", {"start": v(-906.37, 487.9) * mm, "end": v(-903.62, 489.48) * mm});
            skLineSegment(sketch, "E1336.MirrorCS", {"start": v(-916.44, 504.07) * mm, "end": v(-912.6, 506.3) * mm});
            skLineSegment(sketch, "E1337.MirrorCS", {"start": v(-907.64, 490.09) * mm, "end": v(-904.89, 491.68) * mm});
            skLineSegment(sketch, "E1338.MirrorCS", {"start": v(-898.75, 474.7) * mm, "end": v(-896, 476.28) * mm});
            skLineSegment(sketch, "E1339.MirrorCS", {"start": v(-887.2, 457.85) * mm, "end": v(-887.2, 462.3) * mm});
            skLineSegment(sketch, "E1340", {"start": v(-967.24, 508.52) * mm, "end": v(-971.09, 506.3) * mm});
            skLineSegment(sketch, "E1341.0", {"start": v(-895.34, 459.93) * mm, "end": v(-918.72, 419.74) * mm});
            skLineSegment(sketch, "E1341.1", {"start": v(-918.72, 419.74) * mm, "end": v(-965.21, 419.88) * mm});
            skLineSegment(sketch, "E1341.2", {"start": v(-965.21, 419.88) * mm, "end": v(-988.34, 460.22) * mm});
            skLineSegment(sketch, "E1341.3", {"start": v(-988.34, 460.22) * mm, "end": v(-964.97, 500.41) * mm});
            skLineSegment(sketch, "E1341.4", {"start": v(-964.97, 500.41) * mm, "end": v(-918.47, 500.27) * mm});
            skLineSegment(sketch, "E1341.5", {"start": v(-918.47, 500.27) * mm, "end": v(-895.34, 459.93) * mm});
            skPoint(sketch, "E1341.0.midPoint", {"position": v(-907.03, 439.84) * mm});
            skLineSegment(sketch, "E1342", {"start": v(-887.2, 180.55) * mm, "end": v(-836.4, 180.55) * mm});
            skLineSegment(sketch, "E1343", {"start": v(-887.2, 185) * mm, "end": v(-887.2, 180.55) * mm});
            skLineSegment(sketch, "E1344", {"start": v(-836.4, 185) * mm, "end": v(-836.4, 180.55) * mm});
            skPoint(sketch, "E1345.endSnap0", {"position": v(-836.4, 182.78) * mm});
            skLineSegment(sketch, "E1346", {"start": v(-887.2, 182.78) * mm, "end": v(-836.4, 182.78) * mm, "construction": true});
            skLineSegment(sketch, "E1347", {"start": v(-887.2, 185) * mm, "end": v(-836.4, 185) * mm});
            skLineSegment(sketch, "E1348.left", {"start": v(-840.2, 181.19) * mm, "end": v(-840.2, 184.36) * mm});
            skLineSegment(sketch, "E1348.right", {"start": v(-883.38, 181.19) * mm, "end": v(-883.38, 184.36) * mm});
            skPoint(sketch, "E1348.middle", {"position": v(-861.8, 182.78) * mm});
            skLineSegment(sketch, "E1349", {"start": v(-861.8, 184.36) * mm, "end": v(-861.8, 181.19) * mm, "construction": true});
            skLineSegment(sketch, "E1350", {"start": v(-870.68, 184.36) * mm, "end": v(-870.68, 181.19) * mm});
            skLineSegment(sketch, "E1351.MirrorCS", {"start": v(-852.9, 184.36) * mm, "end": v(-852.9, 181.19) * mm});
            skLineSegment(sketch, "E1352", {"start": v(-868.14, 184.36) * mm, "end": v(-868.14, 181.19) * mm});
            skLineSegment(sketch, "E1353.MirrorCS", {"start": v(-855.44, 184.36) * mm, "end": v(-855.44, 181.19) * mm});
            skLineSegment(sketch, "E1354", {"start": v(-883.38, 184.36) * mm, "end": v(-870.68, 184.36) * mm});
            skLineSegment(sketch, "E1355", {"start": v(-883.38, 181.19) * mm, "end": v(-870.68, 181.19) * mm});
            skLineSegment(sketch, "E1356", {"start": v(-868.14, 181.19) * mm, "end": v(-861.8, 181.19) * mm});
            skLineSegment(sketch, "E1357", {"start": v(-868.14, 184.36) * mm, "end": v(-861.8, 184.36) * mm});
            skLineSegment(sketch, "E1358", {"start": v(-861.8, 184.36) * mm, "end": v(-855.44, 184.36) * mm});
            skLineSegment(sketch, "E1359", {"start": v(-861.8, 181.19) * mm, "end": v(-855.44, 181.19) * mm});
            skLineSegment(sketch, "E1360", {"start": v(-852.9, 184.36) * mm, "end": v(-840.2, 184.36) * mm});
            skLineSegment(sketch, "E1361", {"start": v(-852.9, 181.19) * mm, "end": v(-840.2, 181.19) * mm});
            skLineSegment(sketch, "E1362", {"start": v(-832.54, 182.78) * mm, "end": v(-836.4, 180.55) * mm});
            skLineSegment(sketch, "E1363", {"start": v(-891.04, 182.78) * mm, "end": v(-887.2, 180.55) * mm});
            skPoint(sketch, "E1364.endSnap0", {"position": v(-889.12, 181.67) * mm});
            skLineSegment(sketch, "E1365.0", {"start": v(-887.2, 180.55) * mm, "end": v(-891.04, 182.78) * mm, "construction": true});
            skLineSegment(sketch, "E1366", {"start": v(-887.2, 272.99) * mm, "end": v(-836.4, 272.99) * mm});
            skLineSegment(sketch, "E1367", {"start": v(-836.4, 277.43) * mm, "end": v(-836.4, 272.99) * mm});
            skPoint(sketch, "E1368.endSnap0", {"position": v(-836.4, 275.21) * mm});
            skLineSegment(sketch, "E1369", {"start": v(-887.2, 275.21) * mm, "end": v(-836.4, 275.21) * mm, "construction": true});
            skLineSegment(sketch, "E1370", {"start": v(-887.2, 277.43) * mm, "end": v(-836.4, 277.43) * mm});
            skLineSegment(sketch, "E1371.left", {"start": v(-840.2, 273.62) * mm, "end": v(-840.2, 276.8) * mm});
            skLineSegment(sketch, "E1371.right", {"start": v(-883.38, 273.62) * mm, "end": v(-883.38, 276.8) * mm});
            skPoint(sketch, "E1371.middle", {"position": v(-861.8, 275.21) * mm});
            skLineSegment(sketch, "E1372", {"start": v(-861.8, 276.8) * mm, "end": v(-861.8, 273.62) * mm, "construction": true});
            skLineSegment(sketch, "E1373", {"start": v(-870.68, 276.8) * mm, "end": v(-870.68, 273.62) * mm});
            skLineSegment(sketch, "E1374.MirrorCS", {"start": v(-852.9, 276.8) * mm, "end": v(-852.9, 273.62) * mm});
            skLineSegment(sketch, "E1375", {"start": v(-868.14, 276.8) * mm, "end": v(-868.14, 273.62) * mm});
            skLineSegment(sketch, "E1376.MirrorCS", {"start": v(-855.44, 276.8) * mm, "end": v(-855.44, 273.62) * mm});
            skLineSegment(sketch, "E1377", {"start": v(-883.38, 276.8) * mm, "end": v(-870.68, 276.8) * mm});
            skLineSegment(sketch, "E1378", {"start": v(-883.38, 273.62) * mm, "end": v(-870.68, 273.62) * mm});
            skLineSegment(sketch, "E1379", {"start": v(-868.14, 273.62) * mm, "end": v(-861.8, 273.62) * mm});
            skLineSegment(sketch, "E1380", {"start": v(-868.14, 276.8) * mm, "end": v(-861.8, 276.8) * mm});
            skLineSegment(sketch, "E1381", {"start": v(-861.8, 276.8) * mm, "end": v(-855.44, 276.8) * mm});
            skLineSegment(sketch, "E1382", {"start": v(-861.8, 273.62) * mm, "end": v(-855.44, 273.62) * mm});
            skLineSegment(sketch, "E1383", {"start": v(-852.9, 276.8) * mm, "end": v(-840.2, 276.8) * mm});
            skLineSegment(sketch, "E1384", {"start": v(-852.9, 273.62) * mm, "end": v(-840.2, 273.62) * mm});
            skLineSegment(sketch, "E1385", {"start": v(-836.4, 272.99) * mm, "end": v(-811, 229) * mm});
            skLineSegment(sketch, "E1386", {"start": v(-832.54, 275.21) * mm, "end": v(-836.4, 272.99) * mm});
            skLineSegment(sketch, "E1387", {"start": v(-832.54, 275.21) * mm, "end": v(-807.14, 231.22) * mm});
            skLineSegment(sketch, "E1388.left", {"start": v(-812.35, 232.61) * mm, "end": v(-809.6, 234.2) * mm});
            skLineSegment(sketch, "E1388.right", {"start": v(-833.94, 270) * mm, "end": v(-831.19, 271.6) * mm});
            skPoint(sketch, "E1388.middle", {"position": v(-821.77, 252.1) * mm});
            skLineSegment(sketch, "E1389", {"start": v(-820.4, 252.9) * mm, "end": v(-823.14, 251.3) * mm, "construction": true});
            skLineSegment(sketch, "E1390", {"start": v(-824.84, 260.6) * mm, "end": v(-827.59, 259) * mm});
            skLineSegment(sketch, "E1391.MirrorCS", {"start": v(-815.95, 245.2) * mm, "end": v(-818.7, 243.6) * mm});
            skLineSegment(sketch, "E1392", {"start": v(-823.57, 258.4) * mm, "end": v(-826.32, 256.8) * mm});
            skLineSegment(sketch, "E1393.MirrorCS", {"start": v(-817.22, 247.4) * mm, "end": v(-819.97, 245.8) * mm});
            skLineSegment(sketch, "E1394", {"start": v(-831.19, 271.6) * mm, "end": v(-824.84, 260.6) * mm});
            skLineSegment(sketch, "E1395", {"start": v(-833.94, 270) * mm, "end": v(-827.59, 259) * mm});
            skLineSegment(sketch, "E1396", {"start": v(-826.32, 256.8) * mm, "end": v(-823.14, 251.3) * mm});
            skLineSegment(sketch, "E1397", {"start": v(-823.57, 258.4) * mm, "end": v(-820.4, 252.9) * mm});
            skLineSegment(sketch, "E1398", {"start": v(-820.4, 252.9) * mm, "end": v(-817.22, 247.4) * mm});
            skLineSegment(sketch, "E1399", {"start": v(-823.14, 251.3) * mm, "end": v(-819.97, 245.8) * mm});
            skLineSegment(sketch, "E1400", {"start": v(-815.95, 245.2) * mm, "end": v(-809.6, 234.2) * mm});
            skLineSegment(sketch, "E1401", {"start": v(-818.7, 243.6) * mm, "end": v(-812.35, 232.61) * mm});
            skPoint(sketch, "E1402.endSnap0", {"position": v(-889.12, 274.1) * mm});
            skLineSegment(sketch, "E1403", {"start": v(-811, 229) * mm, "end": v(-807.14, 231.22) * mm});
            skLineSegment(sketch, "E1404.MirrorCS", {"start": v(-891.04, 182.78) * mm, "end": v(-887.2, 185) * mm});
            skLineSegment(sketch, "E1405.MirrorCS", {"start": v(-820.4, 205.1) * mm, "end": v(-823.14, 206.68) * mm, "construction": true});
            skLineSegment(sketch, "E1406.MirrorCS", {"start": v(-903.2, 205.1) * mm, "end": v(-900.44, 206.68) * mm, "construction": true});
            skLineSegment(sketch, "E1407.MirrorCS", {"start": v(-861.8, 181.19) * mm, "end": v(-861.8, 184.36) * mm, "construction": true});
            skLineSegment(sketch, "E1408.MirrorCS", {"start": v(-887.2, 185) * mm, "end": v(-891.04, 182.78) * mm, "construction": true});
            skLineSegment(sketch, "E1409.MirrorCS", {"start": v(-832.54, 182.78) * mm, "end": v(-836.4, 185) * mm});
            skLineSegment(sketch, "E1410.MirrorCS", {"start": v(-833.94, 187.98) * mm, "end": v(-831.19, 186.4) * mm});
            skLineSegment(sketch, "E1411.MirrorCS", {"start": v(-900.02, 199.6) * mm, "end": v(-897.27, 201.18) * mm});
            skLineSegment(sketch, "E1412.MirrorCS", {"start": v(-855.44, 181.19) * mm, "end": v(-855.44, 184.36) * mm});
            skLineSegment(sketch, "E1413.MirrorCS", {"start": v(-836.4, 180.55) * mm, "end": v(-836.4, 185) * mm});
            skLineSegment(sketch, "E1414.MirrorCS", {"start": v(-870.68, 181.19) * mm, "end": v(-870.68, 184.36) * mm});
            skLineSegment(sketch, "E1415.MirrorCS", {"start": v(-824.84, 197.4) * mm, "end": v(-827.59, 198.98) * mm});
            skLineSegment(sketch, "E1416.MirrorCS", {"start": v(-868.14, 181.19) * mm, "end": v(-868.14, 184.36) * mm});
            skLineSegment(sketch, "E1417.MirrorCS", {"start": v(-889.65, 187.98) * mm, "end": v(-892.4, 186.4) * mm});
            skLineSegment(sketch, "E1418.MirrorCS", {"start": v(-911.24, 225.38) * mm, "end": v(-913.99, 223.79) * mm});
            skLineSegment(sketch, "E1419.MirrorCS", {"start": v(-906.37, 210.6) * mm, "end": v(-903.62, 212.18) * mm});
            skLineSegment(sketch, "E1420.MirrorCS", {"start": v(-823.57, 199.6) * mm, "end": v(-826.32, 201.18) * mm});
            skLineSegment(sketch, "E1421.MirrorCS", {"start": v(-852.9, 181.19) * mm, "end": v(-852.9, 184.36) * mm});
            skLineSegment(sketch, "E1422.MirrorCS", {"start": v(-907.64, 212.8) * mm, "end": v(-904.89, 214.38) * mm});
            skLineSegment(sketch, "E1423.MirrorCS", {"start": v(-812.35, 225.38) * mm, "end": v(-809.6, 223.79) * mm});
            skLineSegment(sketch, "E1424.MirrorCS", {"start": v(-883.38, 184.36) * mm, "end": v(-883.38, 181.19) * mm});
            skLineSegment(sketch, "E1425.MirrorCS", {"start": v(-815.95, 212.8) * mm, "end": v(-818.7, 214.38) * mm});
            skLineSegment(sketch, "E1426.MirrorCS", {"start": v(-811, 229) * mm, "end": v(-807.14, 226.77) * mm});
            skLineSegment(sketch, "E1427.MirrorCS", {"start": v(-817.22, 210.6) * mm, "end": v(-819.97, 212.18) * mm});
            skLineSegment(sketch, "E1428.MirrorCS", {"start": v(-898.75, 197.4) * mm, "end": v(-896, 198.98) * mm});
            skLineSegment(sketch, "E1429.MirrorCS", {"start": v(-840.2, 184.36) * mm, "end": v(-840.2, 181.19) * mm});
            skLineSegment(sketch, "E1430.MirrorCS", {"start": v(-826.32, 201.18) * mm, "end": v(-823.14, 206.68) * mm});
            skLineSegment(sketch, "E1431.MirrorCS", {"start": v(-903.62, 212.18) * mm, "end": v(-900.44, 206.68) * mm});
            skLineSegment(sketch, "E1432.MirrorCS", {"start": v(-820.4, 205.1) * mm, "end": v(-817.22, 210.6) * mm});
            skLineSegment(sketch, "E1433.MirrorCS", {"start": v(-887.2, 180.55) * mm, "end": v(-887.2, 185) * mm});
            skLineSegment(sketch, "E1434.MirrorCS", {"start": v(-823.14, 206.68) * mm, "end": v(-819.97, 212.18) * mm});
            skLineSegment(sketch, "E1435.MirrorCS", {"start": v(-823.57, 199.6) * mm, "end": v(-820.4, 205.1) * mm});
            skLineSegment(sketch, "E1436.MirrorCS", {"start": v(-900.44, 206.68) * mm, "end": v(-897.27, 201.18) * mm});
            skLineSegment(sketch, "E1437.MirrorCS", {"start": v(-818.7, 214.38) * mm, "end": v(-812.35, 225.38) * mm});
            skLineSegment(sketch, "E1438.MirrorCS", {"start": v(-916.44, 226.77) * mm, "end": v(-891.04, 182.78) * mm});
            skLineSegment(sketch, "E1439.MirrorCS", {"start": v(-836.4, 185) * mm, "end": v(-811, 229) * mm});
            skLineSegment(sketch, "E1440.MirrorCS", {"start": v(-831.19, 186.4) * mm, "end": v(-824.84, 197.4) * mm});
            skLineSegment(sketch, "E1441.MirrorCS", {"start": v(-911.24, 225.38) * mm, "end": v(-904.89, 214.38) * mm});
            skLineSegment(sketch, "E1442.MirrorCS", {"start": v(-896, 198.98) * mm, "end": v(-889.65, 187.98) * mm});
            skPoint(sketch, "E1443.MirrorP", {"position": v(-821.77, 205.89) * mm});
            skLineSegment(sketch, "E1444.MirrorCS", {"start": v(-815.95, 212.8) * mm, "end": v(-809.6, 223.79) * mm});
            skPoint(sketch, "E1445.MirrorP", {"position": v(-889.12, 183.89) * mm});
            skLineSegment(sketch, "E1446.MirrorCS", {"start": v(-906.37, 210.6) * mm, "end": v(-903.2, 205.1) * mm});
            skPoint(sketch, "E1447.MirrorP", {"position": v(-901.82, 205.89) * mm});
            skLineSegment(sketch, "E1448.MirrorCS", {"start": v(-833.94, 187.98) * mm, "end": v(-827.59, 198.98) * mm});
            skLineSegment(sketch, "E1449.MirrorCS", {"start": v(-832.54, 182.78) * mm, "end": v(-807.14, 226.77) * mm});
            skLineSegment(sketch, "E1450.MirrorCS", {"start": v(-912.6, 229) * mm, "end": v(-887.2, 185) * mm});
            skLineSegment(sketch, "E1451.MirrorCS", {"start": v(-898.75, 197.4) * mm, "end": v(-892.4, 186.4) * mm});
            skLineSegment(sketch, "E1452.MirrorCS", {"start": v(-913.99, 223.79) * mm, "end": v(-907.64, 212.8) * mm});
            skLineSegment(sketch, "E1453.MirrorCS", {"start": v(-903.2, 205.1) * mm, "end": v(-900.02, 199.6) * mm});
            skLineSegment(sketch, "E1454", {"start": v(-807.14, 231.22) * mm, "end": v(-807.14, 226.77) * mm});
            skLineSegment(sketch, "E1455", {"start": v(-836.4, 185) * mm, "end": v(-832.54, 182.78) * mm});
            skLineSegment(sketch, "E1456.left", {"start": v(-809.6, 223.79) * mm, "end": v(-812.35, 225.38) * mm});
            skLineSegment(sketch, "E1456.right", {"start": v(-831.19, 186.4) * mm, "end": v(-833.94, 187.98) * mm});
            skLineSegment(sketch, "E1457", {"start": v(-823.14, 206.68) * mm, "end": v(-820.4, 205.1) * mm, "construction": true});
            skLineSegment(sketch, "E1458", {"start": v(-827.59, 198.98) * mm, "end": v(-824.84, 197.4) * mm});
            skLineSegment(sketch, "E1459.MirrorCS", {"start": v(-818.7, 214.38) * mm, "end": v(-815.95, 212.8) * mm});
            skLineSegment(sketch, "E1460", {"start": v(-826.32, 201.18) * mm, "end": v(-823.57, 199.6) * mm});
            skLineSegment(sketch, "E1461.MirrorCS", {"start": v(-819.97, 212.18) * mm, "end": v(-817.22, 210.6) * mm});
            skLineSegment(sketch, "E1462.0", {"start": v(-807.14, 226.77) * mm, "end": v(-811, 229) * mm, "construction": true});
            skLineSegment(sketch, "E1463.MirrorCS", {"start": v(-836.4, 180.55) * mm, "end": v(-832.54, 182.78) * mm});
            skLineSegment(sketch, "E1464", {"start": v(-836.4, 277.43) * mm, "end": v(-832.54, 275.21) * mm});
            skLineSegment(sketch, "E1465.MirrorCS", {"start": v(-823.14, 251.3) * mm, "end": v(-820.4, 252.9) * mm, "construction": true});
            skLineSegment(sketch, "E1466.MirrorCS", {"start": v(-807.14, 231.22) * mm, "end": v(-811, 229) * mm, "construction": true});
            skLineSegment(sketch, "E1467.MirrorCS", {"start": v(-819.97, 245.8) * mm, "end": v(-817.22, 247.4) * mm});
            skLineSegment(sketch, "E1468.MirrorCS", {"start": v(-809.6, 234.2) * mm, "end": v(-812.35, 232.61) * mm});
            skLineSegment(sketch, "E1469.MirrorCS", {"start": v(-831.19, 271.6) * mm, "end": v(-833.94, 270) * mm});
            skLineSegment(sketch, "E1470.MirrorCS", {"start": v(-826.32, 256.8) * mm, "end": v(-823.57, 258.4) * mm});
            skLineSegment(sketch, "E1471.MirrorCS", {"start": v(-836.4, 272.99) * mm, "end": v(-832.54, 275.21) * mm});
            skLineSegment(sketch, "E1472.MirrorCS", {"start": v(-827.59, 259) * mm, "end": v(-824.84, 260.6) * mm});
            skLineSegment(sketch, "E1473.MirrorCS", {"start": v(-818.7, 243.6) * mm, "end": v(-815.95, 245.2) * mm});
            skLineSegment(sketch, "E1474.MirrorCS", {"start": v(-807.14, 226.77) * mm, "end": v(-807.14, 231.22) * mm});
            skLineSegment(sketch, "E1475", {"start": v(-887.2, 277.43) * mm, "end": v(-891.04, 275.21) * mm});
            skLineSegment(sketch, "E1476.0", {"start": v(-815.3, 228.85) * mm, "end": v(-838.67, 188.66) * mm});
            skLineSegment(sketch, "E1476.1", {"start": v(-838.67, 188.66) * mm, "end": v(-885.16, 188.8) * mm});
            skLineSegment(sketch, "E1476.2", {"start": v(-885.16, 188.8) * mm, "end": v(-908.29, 229.14) * mm});
            skLineSegment(sketch, "E1476.3", {"start": v(-908.29, 229.14) * mm, "end": v(-884.92, 269.33) * mm});
            skLineSegment(sketch, "E1476.4", {"start": v(-884.92, 269.33) * mm, "end": v(-838.42, 269.19) * mm});
            skLineSegment(sketch, "E1476.5", {"start": v(-838.42, 269.19) * mm, "end": v(-815.3, 228.85) * mm});
            skPoint(sketch, "E1476.0.midPoint", {"position": v(-826.98, 208.75) * mm});
            skLineSegment(sketch, "E1477", {"start": v(-887.2, 365.42) * mm, "end": v(-836.4, 365.42) * mm});
            skLineSegment(sketch, "E1478", {"start": v(-836.4, 369.87) * mm, "end": v(-836.4, 365.42) * mm});
            skPoint(sketch, "E1479.endSnap0", {"position": v(-836.4, 367.64) * mm});
            skLineSegment(sketch, "E1480", {"start": v(-887.2, 367.64) * mm, "end": v(-836.4, 367.64) * mm, "construction": true});
            skLineSegment(sketch, "E1481", {"start": v(-887.2, 369.87) * mm, "end": v(-836.4, 369.87) * mm});
            skLineSegment(sketch, "E1482.left", {"start": v(-840.2, 366.06) * mm, "end": v(-840.2, 369.23) * mm});
            skLineSegment(sketch, "E1482.right", {"start": v(-883.38, 366.06) * mm, "end": v(-883.38, 369.23) * mm});
            skPoint(sketch, "E1482.middle", {"position": v(-861.8, 367.64) * mm});
            skLineSegment(sketch, "E1483", {"start": v(-861.8, 369.23) * mm, "end": v(-861.8, 366.06) * mm, "construction": true});
            skLineSegment(sketch, "E1484", {"start": v(-870.68, 369.23) * mm, "end": v(-870.68, 366.06) * mm});
            skLineSegment(sketch, "E1485.MirrorCS", {"start": v(-852.9, 369.23) * mm, "end": v(-852.9, 366.06) * mm});
            skLineSegment(sketch, "E1486", {"start": v(-868.14, 369.23) * mm, "end": v(-868.14, 366.06) * mm});
            skLineSegment(sketch, "E1487.MirrorCS", {"start": v(-855.44, 369.23) * mm, "end": v(-855.44, 366.06) * mm});
            skLineSegment(sketch, "E1488", {"start": v(-883.38, 369.23) * mm, "end": v(-870.68, 369.23) * mm});
            skLineSegment(sketch, "E1489", {"start": v(-883.38, 366.06) * mm, "end": v(-870.68, 366.06) * mm});
            skLineSegment(sketch, "E1490", {"start": v(-868.14, 366.06) * mm, "end": v(-861.8, 366.06) * mm});
            skLineSegment(sketch, "E1491", {"start": v(-868.14, 369.23) * mm, "end": v(-861.8, 369.23) * mm});
            skLineSegment(sketch, "E1492", {"start": v(-861.8, 369.23) * mm, "end": v(-855.44, 369.23) * mm});
            skLineSegment(sketch, "E1493", {"start": v(-861.8, 366.06) * mm, "end": v(-855.44, 366.06) * mm});
            skLineSegment(sketch, "E1494", {"start": v(-852.9, 369.23) * mm, "end": v(-840.2, 369.23) * mm});
            skLineSegment(sketch, "E1495", {"start": v(-852.9, 366.06) * mm, "end": v(-840.2, 366.06) * mm});
            skLineSegment(sketch, "E1496", {"start": v(-836.4, 365.42) * mm, "end": v(-811, 321.43) * mm});
            skLineSegment(sketch, "E1497", {"start": v(-832.54, 367.64) * mm, "end": v(-836.4, 365.42) * mm});
            skLineSegment(sketch, "E1498", {"start": v(-832.54, 367.64) * mm, "end": v(-807.14, 323.65) * mm});
            skLineSegment(sketch, "E1499.left", {"start": v(-812.35, 325.04) * mm, "end": v(-809.6, 326.63) * mm});
            skLineSegment(sketch, "E1499.right", {"start": v(-833.94, 362.44) * mm, "end": v(-831.19, 364.03) * mm});
            skPoint(sketch, "E1499.middle", {"position": v(-821.77, 344.53) * mm});
            skLineSegment(sketch, "E1500", {"start": v(-820.4, 345.33) * mm, "end": v(-823.14, 343.74) * mm, "construction": true});
            skLineSegment(sketch, "E1501", {"start": v(-824.84, 353.03) * mm, "end": v(-827.59, 351.44) * mm});
            skLineSegment(sketch, "E1502.MirrorCS", {"start": v(-815.95, 337.63) * mm, "end": v(-818.7, 336.04) * mm});
            skLineSegment(sketch, "E1503", {"start": v(-823.57, 350.83) * mm, "end": v(-826.32, 349.24) * mm});
            skLineSegment(sketch, "E1504.MirrorCS", {"start": v(-817.22, 339.83) * mm, "end": v(-819.97, 338.24) * mm});
            skLineSegment(sketch, "E1505", {"start": v(-831.19, 364.03) * mm, "end": v(-824.84, 353.03) * mm});
            skLineSegment(sketch, "E1506", {"start": v(-833.94, 362.44) * mm, "end": v(-827.59, 351.44) * mm});
            skLineSegment(sketch, "E1507", {"start": v(-826.32, 349.24) * mm, "end": v(-823.14, 343.74) * mm});
            skLineSegment(sketch, "E1508", {"start": v(-823.57, 350.83) * mm, "end": v(-820.4, 345.33) * mm});
            skLineSegment(sketch, "E1509", {"start": v(-820.4, 345.33) * mm, "end": v(-817.22, 339.83) * mm});
            skLineSegment(sketch, "E1510", {"start": v(-823.14, 343.74) * mm, "end": v(-819.97, 338.24) * mm});
            skLineSegment(sketch, "E1511", {"start": v(-815.95, 337.63) * mm, "end": v(-809.6, 326.63) * mm});
            skLineSegment(sketch, "E1512", {"start": v(-818.7, 336.04) * mm, "end": v(-812.35, 325.04) * mm});
            skPoint(sketch, "E1513.endSnap0", {"position": v(-889.12, 366.53) * mm});
            skLineSegment(sketch, "E1514", {"start": v(-811, 321.43) * mm, "end": v(-807.14, 323.65) * mm});
            skLineSegment(sketch, "E1515.MirrorCS", {"start": v(-820.4, 297.52) * mm, "end": v(-823.14, 299.11) * mm, "construction": true});
            skLineSegment(sketch, "E1516.MirrorCS", {"start": v(-861.8, 273.62) * mm, "end": v(-861.8, 276.8) * mm, "construction": true});
            skLineSegment(sketch, "E1517.MirrorCS", {"start": v(-832.54, 275.21) * mm, "end": v(-836.4, 277.43) * mm});
            skLineSegment(sketch, "E1518.MirrorCS", {"start": v(-833.94, 280.41) * mm, "end": v(-831.19, 278.83) * mm});
            skLineSegment(sketch, "E1519.MirrorCS", {"start": v(-855.44, 273.62) * mm, "end": v(-855.44, 276.8) * mm});
            skLineSegment(sketch, "E1520.MirrorCS", {"start": v(-836.4, 272.99) * mm, "end": v(-836.4, 277.43) * mm});
            skLineSegment(sketch, "E1521.MirrorCS", {"start": v(-870.68, 273.62) * mm, "end": v(-870.68, 276.8) * mm});
            skLineSegment(sketch, "E1522.MirrorCS", {"start": v(-824.84, 289.83) * mm, "end": v(-827.59, 291.41) * mm});
            skLineSegment(sketch, "E1523.MirrorCS", {"start": v(-868.14, 273.62) * mm, "end": v(-868.14, 276.8) * mm});
            skLineSegment(sketch, "E1524.MirrorCS", {"start": v(-823.57, 292.03) * mm, "end": v(-826.32, 293.61) * mm});
            skLineSegment(sketch, "E1525.MirrorCS", {"start": v(-852.9, 273.62) * mm, "end": v(-852.9, 276.8) * mm});
            skLineSegment(sketch, "E1526.MirrorCS", {"start": v(-812.35, 317.8) * mm, "end": v(-809.6, 316.22) * mm});
            skLineSegment(sketch, "E1527.MirrorCS", {"start": v(-883.38, 276.8) * mm, "end": v(-883.38, 273.62) * mm});
            skLineSegment(sketch, "E1528.MirrorCS", {"start": v(-815.95, 305.22) * mm, "end": v(-818.7, 306.81) * mm});
            skLineSegment(sketch, "E1529.MirrorCS", {"start": v(-811, 321.43) * mm, "end": v(-807.14, 319.2) * mm});
            skLineSegment(sketch, "E1530.MirrorCS", {"start": v(-817.22, 303.02) * mm, "end": v(-819.97, 304.61) * mm});
            skLineSegment(sketch, "E1531.MirrorCS", {"start": v(-840.2, 276.8) * mm, "end": v(-840.2, 273.62) * mm});
            skLineSegment(sketch, "E1532.MirrorCS", {"start": v(-826.32, 293.61) * mm, "end": v(-823.14, 299.11) * mm});
            skLineSegment(sketch, "E1533.MirrorCS", {"start": v(-820.4, 297.52) * mm, "end": v(-817.22, 303.02) * mm});
            skLineSegment(sketch, "E1534.MirrorCS", {"start": v(-823.14, 299.11) * mm, "end": v(-819.97, 304.61) * mm});
            skLineSegment(sketch, "E1535.MirrorCS", {"start": v(-823.57, 292.03) * mm, "end": v(-820.4, 297.52) * mm});
            skLineSegment(sketch, "E1536.MirrorCS", {"start": v(-818.7, 306.81) * mm, "end": v(-812.35, 317.8) * mm});
            skLineSegment(sketch, "E1537.MirrorCS", {"start": v(-836.4, 277.43) * mm, "end": v(-811, 321.43) * mm});
            skLineSegment(sketch, "E1538.MirrorCS", {"start": v(-831.19, 278.83) * mm, "end": v(-824.84, 289.83) * mm});
            skPoint(sketch, "E1539.MirrorP", {"position": v(-821.77, 298.32) * mm});
            skLineSegment(sketch, "E1540.MirrorCS", {"start": v(-815.95, 305.22) * mm, "end": v(-809.6, 316.22) * mm});
            skPoint(sketch, "E1541.MirrorP", {"position": v(-889.12, 276.32) * mm});
            skLineSegment(sketch, "E1542.MirrorCS", {"start": v(-833.94, 280.41) * mm, "end": v(-827.59, 291.41) * mm});
            skLineSegment(sketch, "E1543.MirrorCS", {"start": v(-832.54, 275.21) * mm, "end": v(-807.14, 319.2) * mm});
            skLineSegment(sketch, "E1544", {"start": v(-807.14, 323.65) * mm, "end": v(-807.14, 319.2) * mm});
            skLineSegment(sketch, "E1545.left", {"start": v(-809.6, 316.22) * mm, "end": v(-812.35, 317.8) * mm});
            skLineSegment(sketch, "E1545.right", {"start": v(-831.19, 278.83) * mm, "end": v(-833.94, 280.41) * mm});
            skLineSegment(sketch, "E1546", {"start": v(-823.14, 299.11) * mm, "end": v(-820.4, 297.52) * mm, "construction": true});
            skLineSegment(sketch, "E1547", {"start": v(-827.59, 291.41) * mm, "end": v(-824.84, 289.83) * mm});
            skLineSegment(sketch, "E1548.MirrorCS", {"start": v(-818.7, 306.81) * mm, "end": v(-815.95, 305.22) * mm});
            skLineSegment(sketch, "E1549", {"start": v(-826.32, 293.61) * mm, "end": v(-823.57, 292.03) * mm});
            skLineSegment(sketch, "E1550.MirrorCS", {"start": v(-819.97, 304.61) * mm, "end": v(-817.22, 303.02) * mm});
            skLineSegment(sketch, "E1551.0", {"start": v(-807.14, 319.2) * mm, "end": v(-811, 321.43) * mm, "construction": true});
            skLineSegment(sketch, "E1552", {"start": v(-836.4, 369.87) * mm, "end": v(-832.54, 367.64) * mm});
            skLineSegment(sketch, "E1553.MirrorCS", {"start": v(-823.14, 343.74) * mm, "end": v(-820.4, 345.33) * mm, "construction": true});
            skLineSegment(sketch, "E1554.MirrorCS", {"start": v(-807.14, 323.65) * mm, "end": v(-811, 321.43) * mm, "construction": true});
            skLineSegment(sketch, "E1555.MirrorCS", {"start": v(-819.97, 338.24) * mm, "end": v(-817.22, 339.83) * mm});
            skLineSegment(sketch, "E1556.MirrorCS", {"start": v(-809.6, 326.63) * mm, "end": v(-812.35, 325.04) * mm});
            skLineSegment(sketch, "E1557.MirrorCS", {"start": v(-831.19, 364.03) * mm, "end": v(-833.94, 362.44) * mm});
            skLineSegment(sketch, "E1558.MirrorCS", {"start": v(-826.32, 349.24) * mm, "end": v(-823.57, 350.83) * mm});
            skLineSegment(sketch, "E1559.MirrorCS", {"start": v(-836.4, 365.42) * mm, "end": v(-832.54, 367.64) * mm});
            skLineSegment(sketch, "E1560.MirrorCS", {"start": v(-827.59, 351.44) * mm, "end": v(-824.84, 353.03) * mm});
            skLineSegment(sketch, "E1561.MirrorCS", {"start": v(-818.7, 336.04) * mm, "end": v(-815.95, 337.63) * mm});
            skLineSegment(sketch, "E1562.MirrorCS", {"start": v(-807.14, 319.2) * mm, "end": v(-807.14, 323.65) * mm});
            skLineSegment(sketch, "E1563", {"start": v(-887.2, 369.87) * mm, "end": v(-891.04, 367.64) * mm});
            skLineSegment(sketch, "E1564.0", {"start": v(-815.3, 321.28) * mm, "end": v(-838.67, 281.09) * mm});
            skLineSegment(sketch, "E1564.1", {"start": v(-838.67, 281.09) * mm, "end": v(-885.16, 281.23) * mm});
            skLineSegment(sketch, "E1564.2", {"start": v(-885.16, 281.23) * mm, "end": v(-908.29, 321.57) * mm});
            skLineSegment(sketch, "E1564.3", {"start": v(-908.29, 321.57) * mm, "end": v(-884.92, 361.76) * mm});
            skLineSegment(sketch, "E1564.4", {"start": v(-884.92, 361.76) * mm, "end": v(-838.42, 361.62) * mm});
            skLineSegment(sketch, "E1564.5", {"start": v(-838.42, 361.62) * mm, "end": v(-815.3, 321.28) * mm});
            skPoint(sketch, "E1564.0.midPoint", {"position": v(-826.98, 301.19) * mm});
            skLineSegment(sketch, "E1565", {"start": v(-887.2, 457.85) * mm, "end": v(-836.4, 457.85) * mm});
            skLineSegment(sketch, "E1566", {"start": v(-836.4, 462.3) * mm, "end": v(-836.4, 457.85) * mm});
            skPoint(sketch, "E1567.endSnap0", {"position": v(-836.4, 460.08) * mm});
            skLineSegment(sketch, "E1568", {"start": v(-887.2, 460.08) * mm, "end": v(-836.4, 460.08) * mm, "construction": true});
            skLineSegment(sketch, "E1569", {"start": v(-887.2, 462.3) * mm, "end": v(-836.4, 462.3) * mm});
            skLineSegment(sketch, "E1570.left", {"start": v(-840.2, 458.49) * mm, "end": v(-840.2, 461.66) * mm});
            skLineSegment(sketch, "E1570.right", {"start": v(-883.38, 458.49) * mm, "end": v(-883.38, 461.66) * mm});
            skPoint(sketch, "E1570.middle", {"position": v(-861.8, 460.08) * mm});
            skLineSegment(sketch, "E1571", {"start": v(-861.8, 461.66) * mm, "end": v(-861.8, 458.49) * mm, "construction": true});
            skLineSegment(sketch, "E1572", {"start": v(-870.68, 461.66) * mm, "end": v(-870.68, 458.49) * mm});
            skLineSegment(sketch, "E1573.MirrorCS", {"start": v(-852.9, 461.66) * mm, "end": v(-852.9, 458.49) * mm});
            skLineSegment(sketch, "E1574", {"start": v(-868.14, 461.66) * mm, "end": v(-868.14, 458.49) * mm});
            skLineSegment(sketch, "E1575.MirrorCS", {"start": v(-855.44, 461.66) * mm, "end": v(-855.44, 458.49) * mm});
            skLineSegment(sketch, "E1576", {"start": v(-883.38, 461.66) * mm, "end": v(-870.68, 461.66) * mm});
            skLineSegment(sketch, "E1577", {"start": v(-883.38, 458.49) * mm, "end": v(-870.68, 458.49) * mm});
            skLineSegment(sketch, "E1578", {"start": v(-868.14, 458.49) * mm, "end": v(-861.8, 458.49) * mm});
            skLineSegment(sketch, "E1579", {"start": v(-868.14, 461.66) * mm, "end": v(-861.8, 461.66) * mm});
            skLineSegment(sketch, "E1580", {"start": v(-861.8, 461.66) * mm, "end": v(-855.44, 461.66) * mm});
            skLineSegment(sketch, "E1581", {"start": v(-861.8, 458.49) * mm, "end": v(-855.44, 458.49) * mm});
            skLineSegment(sketch, "E1582", {"start": v(-852.9, 461.66) * mm, "end": v(-840.2, 461.66) * mm});
            skLineSegment(sketch, "E1583", {"start": v(-852.9, 458.49) * mm, "end": v(-840.2, 458.49) * mm});
            skLineSegment(sketch, "E1584", {"start": v(-836.4, 457.85) * mm, "end": v(-811, 413.86) * mm});
            skLineSegment(sketch, "E1585", {"start": v(-832.54, 460.08) * mm, "end": v(-836.4, 457.85) * mm});
            skLineSegment(sketch, "E1586", {"start": v(-832.54, 460.08) * mm, "end": v(-807.14, 416.08) * mm});
            skLineSegment(sketch, "E1587.left", {"start": v(-812.35, 417.48) * mm, "end": v(-809.6, 419.06) * mm});
            skLineSegment(sketch, "E1587.right", {"start": v(-833.94, 454.87) * mm, "end": v(-831.19, 456.46) * mm});
            skPoint(sketch, "E1587.middle", {"position": v(-821.77, 436.97) * mm});
            skLineSegment(sketch, "E1588", {"start": v(-820.4, 437.76) * mm, "end": v(-823.14, 436.17) * mm, "construction": true});
            skLineSegment(sketch, "E1589", {"start": v(-824.84, 445.46) * mm, "end": v(-827.59, 443.87) * mm});
            skLineSegment(sketch, "E1590.MirrorCS", {"start": v(-815.95, 430.06) * mm, "end": v(-818.7, 428.48) * mm});
            skLineSegment(sketch, "E1591", {"start": v(-823.57, 443.26) * mm, "end": v(-826.32, 441.67) * mm});
            skLineSegment(sketch, "E1592.MirrorCS", {"start": v(-817.22, 432.26) * mm, "end": v(-819.97, 430.68) * mm});
            skLineSegment(sketch, "E1593", {"start": v(-831.19, 456.46) * mm, "end": v(-824.84, 445.46) * mm});
            skLineSegment(sketch, "E1594", {"start": v(-833.94, 454.87) * mm, "end": v(-827.59, 443.87) * mm});
            skLineSegment(sketch, "E1595", {"start": v(-826.32, 441.67) * mm, "end": v(-823.14, 436.17) * mm});
            skLineSegment(sketch, "E1596", {"start": v(-823.57, 443.26) * mm, "end": v(-820.4, 437.76) * mm});
            skLineSegment(sketch, "E1597", {"start": v(-820.4, 437.76) * mm, "end": v(-817.22, 432.26) * mm});
            skLineSegment(sketch, "E1598", {"start": v(-823.14, 436.17) * mm, "end": v(-819.97, 430.68) * mm});
            skLineSegment(sketch, "E1599", {"start": v(-815.95, 430.06) * mm, "end": v(-809.6, 419.06) * mm});
            skLineSegment(sketch, "E1600", {"start": v(-818.7, 428.48) * mm, "end": v(-812.35, 417.48) * mm});
            skPoint(sketch, "E1601.endSnap0", {"position": v(-889.12, 458.97) * mm});
            skLineSegment(sketch, "E1602", {"start": v(-811, 413.86) * mm, "end": v(-807.14, 416.08) * mm});
            skLineSegment(sketch, "E1603.MirrorCS", {"start": v(-820.4, 389.96) * mm, "end": v(-823.14, 391.55) * mm, "construction": true});
            skLineSegment(sketch, "E1604.MirrorCS", {"start": v(-861.8, 366.06) * mm, "end": v(-861.8, 369.23) * mm, "construction": true});
            skLineSegment(sketch, "E1605.MirrorCS", {"start": v(-832.54, 367.64) * mm, "end": v(-836.4, 369.87) * mm});
            skLineSegment(sketch, "E1606.MirrorCS", {"start": v(-833.94, 372.85) * mm, "end": v(-831.19, 371.26) * mm});
            skLineSegment(sketch, "E1607.MirrorCS", {"start": v(-855.44, 366.06) * mm, "end": v(-855.44, 369.23) * mm});
            skLineSegment(sketch, "E1608.MirrorCS", {"start": v(-836.4, 365.42) * mm, "end": v(-836.4, 369.87) * mm});
            skLineSegment(sketch, "E1609.MirrorCS", {"start": v(-870.68, 366.06) * mm, "end": v(-870.68, 369.23) * mm});
            skLineSegment(sketch, "E1610.MirrorCS", {"start": v(-824.84, 382.26) * mm, "end": v(-827.59, 383.85) * mm});
            skLineSegment(sketch, "E1611.MirrorCS", {"start": v(-868.14, 366.06) * mm, "end": v(-868.14, 369.23) * mm});
            skLineSegment(sketch, "E1612.MirrorCS", {"start": v(-823.57, 384.46) * mm, "end": v(-826.32, 386.05) * mm});
            skLineSegment(sketch, "E1613.MirrorCS", {"start": v(-852.9, 366.06) * mm, "end": v(-852.9, 369.23) * mm});
            skLineSegment(sketch, "E1614.MirrorCS", {"start": v(-812.35, 410.24) * mm, "end": v(-809.6, 408.66) * mm});
            skLineSegment(sketch, "E1615.MirrorCS", {"start": v(-883.38, 369.23) * mm, "end": v(-883.38, 366.06) * mm});
            skLineSegment(sketch, "E1616.MirrorCS", {"start": v(-815.95, 397.66) * mm, "end": v(-818.7, 399.24) * mm});
            skLineSegment(sketch, "E1617.MirrorCS", {"start": v(-811, 413.86) * mm, "end": v(-807.14, 411.64) * mm});
            skLineSegment(sketch, "E1618.MirrorCS", {"start": v(-817.22, 395.46) * mm, "end": v(-819.97, 397.04) * mm});
            skLineSegment(sketch, "E1619.MirrorCS", {"start": v(-840.2, 369.23) * mm, "end": v(-840.2, 366.06) * mm});
            skLineSegment(sketch, "E1620.MirrorCS", {"start": v(-826.32, 386.05) * mm, "end": v(-823.14, 391.55) * mm});
            skLineSegment(sketch, "E1621.MirrorCS", {"start": v(-820.4, 389.96) * mm, "end": v(-817.22, 395.46) * mm});
            skLineSegment(sketch, "E1622.MirrorCS", {"start": v(-823.14, 391.55) * mm, "end": v(-819.97, 397.04) * mm});
            skLineSegment(sketch, "E1623.MirrorCS", {"start": v(-823.57, 384.46) * mm, "end": v(-820.4, 389.96) * mm});
            skLineSegment(sketch, "E1624.MirrorCS", {"start": v(-818.7, 399.24) * mm, "end": v(-812.35, 410.24) * mm});
            skLineSegment(sketch, "E1625.MirrorCS", {"start": v(-836.4, 369.87) * mm, "end": v(-811, 413.86) * mm});
            skLineSegment(sketch, "E1626.MirrorCS", {"start": v(-831.19, 371.26) * mm, "end": v(-824.84, 382.26) * mm});
            skPoint(sketch, "E1627.MirrorP", {"position": v(-821.77, 390.75) * mm});
            skLineSegment(sketch, "E1628.MirrorCS", {"start": v(-815.95, 397.66) * mm, "end": v(-809.6, 408.66) * mm});
            skPoint(sketch, "E1629.MirrorP", {"position": v(-889.12, 368.75) * mm});
            skLineSegment(sketch, "E1630.MirrorCS", {"start": v(-833.94, 372.85) * mm, "end": v(-827.59, 383.85) * mm});
            skLineSegment(sketch, "E1631.MirrorCS", {"start": v(-832.54, 367.64) * mm, "end": v(-807.14, 411.64) * mm});
            skLineSegment(sketch, "E1632", {"start": v(-807.14, 416.08) * mm, "end": v(-807.14, 411.64) * mm});
            skLineSegment(sketch, "E1633.left", {"start": v(-809.6, 408.66) * mm, "end": v(-812.35, 410.24) * mm});
            skLineSegment(sketch, "E1633.right", {"start": v(-831.19, 371.26) * mm, "end": v(-833.94, 372.85) * mm});
            skLineSegment(sketch, "E1634", {"start": v(-823.14, 391.55) * mm, "end": v(-820.4, 389.96) * mm, "construction": true});
            skLineSegment(sketch, "E1635", {"start": v(-827.59, 383.85) * mm, "end": v(-824.84, 382.26) * mm});
            skLineSegment(sketch, "E1636.MirrorCS", {"start": v(-818.7, 399.24) * mm, "end": v(-815.95, 397.66) * mm});
            skLineSegment(sketch, "E1637", {"start": v(-826.32, 386.05) * mm, "end": v(-823.57, 384.46) * mm});
            skLineSegment(sketch, "E1638.MirrorCS", {"start": v(-819.97, 397.04) * mm, "end": v(-817.22, 395.46) * mm});
            skLineSegment(sketch, "E1639.0", {"start": v(-807.14, 411.64) * mm, "end": v(-811, 413.86) * mm, "construction": true});
            skLineSegment(sketch, "E1640", {"start": v(-836.4, 462.3) * mm, "end": v(-832.54, 460.08) * mm});
            skLineSegment(sketch, "E1641.MirrorCS", {"start": v(-823.14, 436.17) * mm, "end": v(-820.4, 437.76) * mm, "construction": true});
            skLineSegment(sketch, "E1642.MirrorCS", {"start": v(-807.14, 416.08) * mm, "end": v(-811, 413.86) * mm, "construction": true});
            skLineSegment(sketch, "E1643.MirrorCS", {"start": v(-819.97, 430.68) * mm, "end": v(-817.22, 432.26) * mm});
            skLineSegment(sketch, "E1644.MirrorCS", {"start": v(-809.6, 419.06) * mm, "end": v(-812.35, 417.48) * mm});
            skLineSegment(sketch, "E1645.MirrorCS", {"start": v(-831.19, 456.46) * mm, "end": v(-833.94, 454.87) * mm});
            skLineSegment(sketch, "E1646.MirrorCS", {"start": v(-826.32, 441.67) * mm, "end": v(-823.57, 443.26) * mm});
            skLineSegment(sketch, "E1647.MirrorCS", {"start": v(-836.4, 457.85) * mm, "end": v(-832.54, 460.08) * mm});
            skLineSegment(sketch, "E1648.MirrorCS", {"start": v(-827.59, 443.87) * mm, "end": v(-824.84, 445.46) * mm});
            skLineSegment(sketch, "E1649.MirrorCS", {"start": v(-818.7, 428.48) * mm, "end": v(-815.95, 430.06) * mm});
            skLineSegment(sketch, "E1650.MirrorCS", {"start": v(-807.14, 411.64) * mm, "end": v(-807.14, 416.08) * mm});
            skLineSegment(sketch, "E1651", {"start": v(-887.2, 462.3) * mm, "end": v(-891.04, 460.08) * mm});
            skLineSegment(sketch, "E1652.0", {"start": v(-815.3, 413.72) * mm, "end": v(-838.67, 373.52) * mm});
            skLineSegment(sketch, "E1652.1", {"start": v(-838.67, 373.52) * mm, "end": v(-885.16, 373.66) * mm});
            skLineSegment(sketch, "E1652.2", {"start": v(-885.16, 373.66) * mm, "end": v(-908.29, 414) * mm});
            skLineSegment(sketch, "E1652.3", {"start": v(-908.29, 414) * mm, "end": v(-884.92, 454.2) * mm});
            skLineSegment(sketch, "E1652.4", {"start": v(-884.92, 454.2) * mm, "end": v(-838.42, 454.06) * mm});
            skLineSegment(sketch, "E1652.5", {"start": v(-838.42, 454.06) * mm, "end": v(-815.3, 413.72) * mm});
            skPoint(sketch, "E1652.0.midPoint", {"position": v(-826.98, 393.62) * mm});
            skLineSegment(sketch, "E1653", {"start": v(-807.14, 323.65) * mm, "end": v(-811, 321.43) * mm});
            skLineSegment(sketch, "E1654", {"start": v(-807.14, 416.08) * mm, "end": v(-811, 413.86) * mm});
            skSolve(sketch);
        }
        {
            var Q0;
            Q0=makeQuery(id+"F0.imprint","IMPRINT",FACE,{"disambiguationData":[TD([[makeQuery(id+"F0.imprint","IMPRINT",EDGE,{"derivedFrom":sQuery(id+"F0.wireOp",EDGE,"E30")}),1.0]])]});
            var Q1;
            Q1=makeQuery(id+"F0.imprint","IMPRINT",FACE,{"disambiguationData":[TD([[makeQuery(id+"F0.imprint","IMPRINT",EDGE,{"derivedFrom":sQuery(id+"F0.wireOp",EDGE,"E24")}),1.0]])]});
            var Q2;
            Q2=makeQuery(id+"F0.imprint","IMPRINT",FACE,{"disambiguationData":[TD([[makeQuery(id+"F0.imprint","IMPRINT",EDGE,{"derivedFrom":sQuery(id+"F0.wireOp",EDGE,"E82.MirrorCS")}),1.0]])]});
            var Q3;
            Q3=makeQuery(id+"F0.imprint","IMPRINT",FACE,{"disambiguationData":[TD([[makeQuery(id+"F0.imprint","IMPRINT",EDGE,{"derivedFrom":sQuery(id+"F0.wireOp",EDGE,"E81")}),1.0]])]});
            var Q4;
            Q4=makeQuery(id+"F0.imprint","IMPRINT",FACE,{"disambiguationData":[TD([[makeQuery(id+"F0.imprint","IMPRINT",EDGE,{"derivedFrom":sQuery(id+"F0.wireOp",EDGE,"E143")}),1.0]])]});
            var Q5;
            Q5=makeQuery(id+"F0.imprint","IMPRINT",FACE,{"disambiguationData":[TD([[makeQuery(id+"F0.imprint","IMPRINT",EDGE,{"derivedFrom":sQuery(id+"F0.wireOp",EDGE,"E134")}),1.0]])]});
            var Q6;
            Q6=makeQuery(id+"F0.imprint","IMPRINT",FACE,{"disambiguationData":[TD([[makeQuery(id+"F0.imprint","IMPRINT",EDGE,{"derivedFrom":sQuery(id+"F0.wireOp",EDGE,"930dedf4-2d83-4b8b-8b55-9059e09ae95c.MirrorCS")}),-1.0]])]});
            var Q7;
            Q7=makeQuery(id+"F0.imprint","IMPRINT",FACE,{"disambiguationData":[TD([[makeQuery(id+"F0.imprint","IMPRINT",EDGE,{"derivedFrom":sQuery(id+"F0.wireOp",EDGE,"6570753b-811f-4365-b11a-a9cbfb38ab35")}),1.0]])]});
            var Q8;
            Q8=makeQuery(id+"F0.imprint","IMPRINT",FACE,{"disambiguationData":[TD([[makeQuery(id+"F0.imprint","IMPRINT",EDGE,{"derivedFrom":sQuery(id+"F0.wireOp",EDGE,"E90.MirrorCS")}),-1.0]])]});
            var Q9;
            Q9=makeQuery(id+"F0.imprint","IMPRINT",FACE,{"disambiguationData":[TD([[makeQuery(id+"F0.imprint","IMPRINT",EDGE,{"derivedFrom":sQuery(id+"F0.wireOp",EDGE,"f29950b3-5ab6-43ee-bb47-0cffdfada996.MirrorCS")}),1.0]])]});
            var Q10;
            Q10=makeQuery(id+"F0.imprint","IMPRINT",FACE,{"disambiguationData":[TD([[makeQuery(id+"F0.imprint","IMPRINT",EDGE,{"derivedFrom":sQuery(id+"F0.wireOp",EDGE,"6439b138-387e-4292-85c5-b0e5f2dc72f0")}),1.0]])]});
            var Q11;
            Q11=makeQuery(id+"F0.imprint","IMPRINT",FACE,{"disambiguationData":[TD([[makeQuery(id+"F0.imprint","IMPRINT",EDGE,{"derivedFrom":sQuery(id+"F0.wireOp",EDGE,"c3b65142-6a43-47dc-a7cc-2a4a00c8030a.MirrorCS")}),-1.0]])]});
            var Q12;
            Q12=makeQuery(id+"F0.imprint","IMPRINT",FACE,{"disambiguationData":[TD([[makeQuery(id+"F0.imprint","IMPRINT",EDGE,{"derivedFrom":sQuery(id+"F0.wireOp",EDGE,"72b8f760-c9fd-43ad-a9b9-b6b262194cfc.MirrorCS")}),1.0]])]});
            var Q13;
            Q13=makeQuery(id+"F0.imprint","IMPRINT",FACE,{"disambiguationData":[TD([[makeQuery(id+"F0.imprint","IMPRINT",EDGE,{"derivedFrom":sQuery(id+"F0.wireOp",EDGE,"62336fad-bb5a-4227-ba00-837f4be8ea73.MirrorCS")}),-1.0]])]});
            var Q14;
            Q14=makeQuery(id+"F0.imprint","IMPRINT",FACE,{"disambiguationData":[TD([[makeQuery(id+"F0.imprint","IMPRINT",EDGE,{"derivedFrom":sQuery(id+"F0.wireOp",EDGE,"5292e8aa-793e-4388-b925-83b6ac676c8b")}),1.0]])]});
            var Q15;
            Q15=makeQuery(id+"F0.imprint","IMPRINT",FACE,{"disambiguationData":[TD([[makeQuery(id+"F0.imprint","IMPRINT",EDGE,{"derivedFrom":sQuery(id+"F0.wireOp",EDGE,"a36d15a1-651a-48fe-a868-c0545d57ef350.MirrorCS")}),1.0]])]});
            var Q16;
            Q16=makeQuery(id+"F0.imprint","IMPRINT",FACE,{"disambiguationData":[TD([[makeQuery(id+"F0.imprint","IMPRINT",EDGE,{"derivedFrom":sQuery(id+"F0.wireOp",EDGE,"fb6067dc-29dd-4804-86f0-7a7858a01ea8.MirrorCS")}),1.0]])]});
            var Q17;
            Q17=makeQuery(id+"F0.imprint","IMPRINT",FACE,{"disambiguationData":[TD([[makeQuery(id+"F0.imprint","IMPRINT",EDGE,{"derivedFrom":sQuery(id+"F0.wireOp",EDGE,"a36d15a1-651a-48fe-a868-c0545d57ef355.MirrorCS")}),-1.0]])]});
            var Q18;
            Q18=makeQuery(id+"F0.imprint","IMPRINT",FACE,{"disambiguationData":[TD([[makeQuery(id+"F0.imprint","IMPRINT",EDGE,{"derivedFrom":sQuery(id+"F0.wireOp",EDGE,"fbde0b22-fe4e-4072-bd88-99435dc31b14.MirrorCS")}),-1.0]])]});
            var Q19;
            Q19=makeQuery(id+"F0.imprint","IMPRINT",FACE,{"disambiguationData":[TD([[makeQuery(id+"F0.imprint","IMPRINT",EDGE,{"derivedFrom":sQuery(id+"F0.wireOp",EDGE,"a36d15a1-651a-48fe-a868-c0545d57ef358.MirrorCS")}),-1.0]])]});
            var Q20;
            Q20=makeQuery(id+"F0.imprint","IMPRINT",FACE,{"disambiguationData":[TD([[makeQuery(id+"F0.imprint","IMPRINT",EDGE,{"derivedFrom":sQuery(id+"F0.wireOp",EDGE,"9fc7aec9-07a5-474b-a00d-ec70c89e4a84")}),1.0]])]});
            var Q21;
            Q21=makeQuery(id+"F0.imprint","IMPRINT",FACE,{"disambiguationData":[TD([[makeQuery(id+"F0.imprint","IMPRINT",EDGE,{"derivedFrom":sQuery(id+"F0.wireOp",EDGE,"834990e3-d3e4-4368-a2ad-76951a6882b7.MirrorCS")}),-1.0]])]});
            var Q22;
            Q22=makeQuery(id+"F0.imprint","IMPRINT",FACE,{"disambiguationData":[TD([[makeQuery(id+"F0.imprint","IMPRINT",EDGE,{"derivedFrom":sQuery(id+"F0.wireOp",EDGE,"a6144f18-dc5e-4c6e-b31c-7e3fed000be5.MirrorCS")}),1.0]])]});
            var Q23;
            Q23=makeQuery(id+"F0.imprint","IMPRINT",FACE,{"disambiguationData":[TD([[makeQuery(id+"F0.imprint","IMPRINT",EDGE,{"derivedFrom":sQuery(id+"F0.wireOp",EDGE,"dd018b08-eb82-4778-a51c-ca58f3f22463.MirrorCS")}),-1.0]])]});
            var Q24;
            Q24=makeQuery(id+"F0.imprint","IMPRINT",FACE,{"disambiguationData":[TD([[makeQuery(id+"F0.imprint","IMPRINT",EDGE,{"derivedFrom":sQuery(id+"F0.wireOp",EDGE,"67ff597e-5083-4d11-82c4-6efb6a149a32.MirrorCS")}),-1.0]])]});
            var Q25;
            Q25=makeQuery(id+"F0.imprint","IMPRINT",FACE,{"disambiguationData":[TD([[makeQuery(id+"F0.imprint","IMPRINT",EDGE,{"derivedFrom":sQuery(id+"F0.wireOp",EDGE,"1bbd868e-9afc-42d6-8b11-ecf4abd326d3.MirrorCS")}),-1.0]])]});
            var Q26;
            Q26=makeQuery(id+"F0.imprint","IMPRINT",FACE,{"disambiguationData":[TD([[makeQuery(id+"F0.imprint","IMPRINT",EDGE,{"derivedFrom":sQuery(id+"F0.wireOp",EDGE,"7424bb74-779f-4825-a635-390552279b9d.MirrorCS")}),1.0]])]});
            var Q27;
            Q27=makeQuery(id+"F0.imprint","IMPRINT",FACE,{"disambiguationData":[TD([[makeQuery(id+"F0.imprint","IMPRINT",EDGE,{"derivedFrom":sQuery(id+"F0.wireOp",EDGE,"1e52a223-575a-49e3-a5d0-3279d9ff813e")}),1.0]])]});
            var Q28;
            Q28=makeQuery(id+"F0.imprint","IMPRINT",FACE,{"disambiguationData":[TD([[makeQuery(id+"F0.imprint","IMPRINT",EDGE,{"derivedFrom":sQuery(id+"F0.wireOp",EDGE,"fff2690d-8a3a-4f14-ace0-f27e414b8b69.MirrorCS")}),1.0]])]});
            var Q29;
            Q29=makeQuery(id+"F0.imprint","IMPRINT",FACE,{"disambiguationData":[TD([[makeQuery(id+"F0.imprint","IMPRINT",EDGE,{"derivedFrom":sQuery(id+"F0.wireOp",EDGE,"fd6a4565-bc39-4eac-89a8-c9ef9922e2c2.MirrorCS")}),-1.0]])]});
            var Q30;
            Q30=makeQuery(id+"F0.imprint","IMPRINT",FACE,{"disambiguationData":[TD([[makeQuery(id+"F0.imprint","IMPRINT",EDGE,{"derivedFrom":sQuery(id+"F0.wireOp",EDGE,"540bedad-7875-459c-86bb-fd8edf0bee21.MirrorCS")}),-1.0]])]});
            var Q31;
            Q31=makeQuery(id+"F0.imprint","IMPRINT",FACE,{"disambiguationData":[TD([[makeQuery(id+"F0.imprint","IMPRINT",EDGE,{"derivedFrom":sQuery(id+"F0.wireOp",EDGE,"8ed1b27b-a74b-491a-8a7a-07f137f2b3b9.MirrorCS")}),1.0]])]});
            var Q32;
            Q32=makeQuery(id+"F0.imprint","IMPRINT",FACE,{"disambiguationData":[TD([[makeQuery(id+"F0.imprint","IMPRINT",EDGE,{"derivedFrom":sQuery(id+"F0.wireOp",EDGE,"6a3769bc-dd9c-4a0c-809f-3b1142e488e3")}),1.0]])]});
            var Q33;
            Q33=makeQuery(id+"F0.imprint","IMPRINT",FACE,{"disambiguationData":[TD([[makeQuery(id+"F0.imprint","IMPRINT",EDGE,{"derivedFrom":sQuery(id+"F0.wireOp",EDGE,"c6e13bd8-f415-450b-9f57-cb1ec7fdfc31.MirrorCS")}),-1.0]])]});
            var Q34;
            Q34=makeQuery(id+"F0.imprint","IMPRINT",FACE,{"disambiguationData":[TD([[makeQuery(id+"F0.imprint","IMPRINT",EDGE,{"derivedFrom":sQuery(id+"F0.wireOp",EDGE,"75d368d4-1ec5-4209-9122-2ac09438cec9")}),1.0]])]});
            var Q35;
            Q35=makeQuery(id+"F0.imprint","IMPRINT",FACE,{"disambiguationData":[TD([[makeQuery(id+"F0.imprint","IMPRINT",EDGE,{"derivedFrom":sQuery(id+"F0.wireOp",EDGE,"c353834b-293f-4320-a5be-103ba9951c23.MirrorCS")}),1.0]])]});
            var Q36;
            Q36=makeQuery(id+"F0.imprint","IMPRINT",FACE,{"disambiguationData":[TD([[makeQuery(id+"F0.imprint","IMPRINT",EDGE,{"derivedFrom":sQuery(id+"F0.wireOp",EDGE,"238b2c6d-2a7b-43c8-86cb-87090c9e4131.MirrorCS")}),-1.0]])]});
            var Q37;
            Q37=makeQuery(id+"F0.imprint","IMPRINT",FACE,{"disambiguationData":[TD([[makeQuery(id+"F0.imprint","IMPRINT",EDGE,{"derivedFrom":sQuery(id+"F0.wireOp",EDGE,"6e7bb8d0-d5a7-4633-9e05-38cac3758b86")}),1.0]])]});
            var Q38;
            Q38=makeQuery(id+"F0.imprint","IMPRINT",FACE,{"disambiguationData":[TD([[makeQuery(id+"F0.imprint","IMPRINT",EDGE,{"derivedFrom":sQuery(id+"F0.wireOp",EDGE,"4e9335f0-e0bb-49f2-97b9-79593e453623")}),1.0]])]});
            var Q39;
            Q39=makeQuery(id+"F0.imprint","IMPRINT",FACE,{"disambiguationData":[TD([[makeQuery(id+"F0.imprint","IMPRINT",EDGE,{"derivedFrom":sQuery(id+"F0.wireOp",EDGE,"11202429-4bbe-41c9-80c2-80f7cd88a402.MirrorCS")}),-1.0]])]});
            var Q40;
            Q40=makeQuery(id+"F0.imprint","IMPRINT",FACE,{"disambiguationData":[TD([[makeQuery(id+"F0.imprint","IMPRINT",EDGE,{"derivedFrom":sQuery(id+"F0.wireOp",EDGE,"0bf9a244-adfc-4bf4-bf7c-008a291155b1.MirrorCS")}),-1.0]])]});
            var Q41;
            Q41=makeQuery(id+"F0.imprint","IMPRINT",FACE,{"disambiguationData":[TD([[makeQuery(id+"F0.imprint","IMPRINT",EDGE,{"derivedFrom":sQuery(id+"F0.wireOp",EDGE,"5d4d7b34-a0ef-4fc0-8a9f-76da22b0dc98")}),1.0]])]});
            var Q42;
            Q42=makeQuery(id+"F0.imprint","IMPRINT",FACE,{"disambiguationData":[TD([[makeQuery(id+"F0.imprint","IMPRINT",EDGE,{"derivedFrom":sQuery(id+"F0.wireOp",EDGE,"e5193fdc-4d1f-4681-8cd7-1bd9673117e2")}),1.0]])]});
            var Q43;
            Q43=makeQuery(id+"F0.imprint","IMPRINT",FACE,{"disambiguationData":[TD([[makeQuery(id+"F0.imprint","IMPRINT",EDGE,{"derivedFrom":sQuery(id+"F0.wireOp",EDGE,"5a3dca7a-4faf-4dc0-acb3-ed07b61b7ae4.MirrorCS")}),1.0]])]});
            var Q44;
            Q44=makeQuery(id+"F0.imprint","IMPRINT",FACE,{"disambiguationData":[TD([[makeQuery(id+"F0.imprint","IMPRINT",EDGE,{"derivedFrom":sQuery(id+"F0.wireOp",EDGE,"5410d7f1-1553-474f-8e32-46b3729ad7c6.MirrorCS")}),-1.0]])]});
            var Q45;
            Q45=makeQuery(id+"F0.imprint","IMPRINT",FACE,{"disambiguationData":[TD([[makeQuery(id+"F0.imprint","IMPRINT",EDGE,{"derivedFrom":sQuery(id+"F0.wireOp",EDGE,"6929af7f-03ca-41e3-8076-07cc3e00f7c4.MirrorCS")}),1.0]])]});
            var Q46;
            Q46=makeQuery(id+"F0.imprint","IMPRINT",FACE,{"disambiguationData":[TD([[makeQuery(id+"F0.imprint","IMPRINT",EDGE,{"derivedFrom":sQuery(id+"F0.wireOp",EDGE,"f18df92d-2584-42fe-943a-964de10e0314")}),1.0]])]});
            var Q47;
            Q47=makeQuery(id+"F0.imprint","IMPRINT",FACE,{"disambiguationData":[TD([[makeQuery(id+"F0.imprint","IMPRINT",EDGE,{"derivedFrom":sQuery(id+"F0.wireOp",EDGE,"fb53d5b5-8270-47d8-a7b3-c4f284fdc201")}),1.0]])]});
            var Q48;
            Q48=makeQuery(id+"F0.imprint","IMPRINT",FACE,{"disambiguationData":[TD([[makeQuery(id+"F0.imprint","IMPRINT",EDGE,{"derivedFrom":sQuery(id+"F0.wireOp",EDGE,"21fe16a3-90b1-4aa2-aaf0-adb625a7fb3f")}),1.0]])]});
            var Q49;
            Q49=makeQuery(id+"F0.imprint","IMPRINT",FACE,{"disambiguationData":[TD([[makeQuery(id+"F0.imprint","IMPRINT",EDGE,{"derivedFrom":sQuery(id+"F0.wireOp",EDGE,"581c3449-be73-4448-956a-8e5d3dcaee4d.MirrorCS")}),-1.0]])]});
            var Q50;
            Q50=makeQuery(id+"F0.imprint","IMPRINT",FACE,{"disambiguationData":[TD([[makeQuery(id+"F0.imprint","IMPRINT",EDGE,{"derivedFrom":sQuery(id+"F0.wireOp",EDGE,"fb0dcb06-1d51-4f8a-b954-1e7591c087ae.MirrorCS")}),1.0]])]});
            var Q51;
            Q51=makeQuery(id+"F0.imprint","IMPRINT",FACE,{"disambiguationData":[TD([[makeQuery(id+"F0.imprint","IMPRINT",EDGE,{"derivedFrom":sQuery(id+"F0.wireOp",EDGE,"477da0d6-631d-4c19-b11b-28d970b13b2a")}),1.0]])]});
            var Q52;
            Q52=makeQuery(id+"F0.imprint","IMPRINT",FACE,{"disambiguationData":[TD([[makeQuery(id+"F0.imprint","IMPRINT",EDGE,{"derivedFrom":sQuery(id+"F0.wireOp",EDGE,"ae544586-ea1c-4426-9e3c-212fcaa1edb4")}),1.0]])]});
            var Q53;
            Q53=makeQuery(id+"F0.imprint","IMPRINT",FACE,{"disambiguationData":[TD([[makeQuery(id+"F0.imprint","IMPRINT",EDGE,{"derivedFrom":sQuery(id+"F0.wireOp",EDGE,"dba6a027-60b8-4e8c-9a13-e2da1c82cd69")}),1.0]])]});
            var Q54;
            Q54=makeQuery(id+"F0.imprint","IMPRINT",FACE,{"disambiguationData":[TD([[makeQuery(id+"F0.imprint","IMPRINT",EDGE,{"derivedFrom":sQuery(id+"F0.wireOp",EDGE,"23b21192-7d69-4b8a-9dbf-dfcd70aea1bb")}),1.0]])]});
            var Q55;
            Q55=makeQuery(id+"F0.imprint","IMPRINT",FACE,{"disambiguationData":[TD([[makeQuery(id+"F0.imprint","IMPRINT",EDGE,{"derivedFrom":sQuery(id+"F0.wireOp",EDGE,"82c1dd1d-a279-427f-bffb-b7f75b71ae6c.MirrorCS")}),1.0]])]});
            var Q56;
            Q56=makeQuery(id+"F0.imprint","IMPRINT",FACE,{"disambiguationData":[TD([[makeQuery(id+"F0.imprint","IMPRINT",EDGE,{"derivedFrom":sQuery(id+"F0.wireOp",EDGE,"e5c82b55-3b9b-4e48-92b4-dfc1de2c3c21")}),1.0]])]});
            var Q57;
            Q57=makeQuery(id+"F0.imprint","IMPRINT",FACE,{"disambiguationData":[TD([[makeQuery(id+"F0.imprint","IMPRINT",EDGE,{"derivedFrom":sQuery(id+"F0.wireOp",EDGE,"9d4359a0-cbd5-4d50-bb40-2d3be3cecd4d")}),1.0]])]});
            var Q58;
            Q58=makeQuery(id+"F0.imprint","IMPRINT",FACE,{"disambiguationData":[TD([[makeQuery(id+"F0.imprint","IMPRINT",EDGE,{"derivedFrom":sQuery(id+"F0.wireOp",EDGE,"a28e28d0-b3f5-459a-8cc8-a304c070a47b.MirrorCS")}),-1.0]])]});
            var Q59;
            Q59=makeQuery(id+"F0.imprint","IMPRINT",FACE,{"disambiguationData":[TD([[makeQuery(id+"F0.imprint","IMPRINT",EDGE,{"derivedFrom":sQuery(id+"F0.wireOp",EDGE,"c03affca-ee44-4105-8db8-614de076143c")}),1.0]])]});
            var Q60;
            Q60=makeQuery(id+"F0.imprint","IMPRINT",FACE,{"disambiguationData":[TD([[makeQuery(id+"F0.imprint","IMPRINT",EDGE,{"derivedFrom":sQuery(id+"F0.wireOp",EDGE,"E21")}),1.0]])]});
            var Q61;
            Q61=makeQuery(id+"F0.imprint","IMPRINT",FACE,{"disambiguationData":[TD([[makeQuery(id+"F0.imprint","IMPRINT",EDGE,{"derivedFrom":sQuery(id+"F0.wireOp",EDGE,"E91.MirrorCS")}),-1.0]])]});
            var Q62;
            Q62=makeQuery(id+"F0.imprint","IMPRINT",FACE,{"disambiguationData":[TD([[makeQuery(id+"F0.imprint","IMPRINT",EDGE,{"derivedFrom":sQuery(id+"F0.wireOp",EDGE,"E26")}),1.0]])]});
            var Q63;
            Q63=makeQuery(id+"F0.imprint","IMPRINT",FACE,{"disambiguationData":[TD([[makeQuery(id+"F0.imprint","IMPRINT",EDGE,{"derivedFrom":sQuery(id+"F0.wireOp",EDGE,"E105.MirrorCS")}),1.0]])]});
            var Q64;
            Q64=makeQuery(id+"F0.imprint","IMPRINT",FACE,{"disambiguationData":[TD([[makeQuery(id+"F0.imprint","IMPRINT",EDGE,{"derivedFrom":sQuery(id+"F0.wireOp",EDGE,"bbcefe13-07ef-40f0-ab07-79d1f37fc04f.MirrorCS")}),-1.0]])]});
            var Q65;
            Q65=makeQuery(id+"F0.imprint","IMPRINT",FACE,{"disambiguationData":[TD([[makeQuery(id+"F0.imprint","IMPRINT",EDGE,{"derivedFrom":sQuery(id+"F0.wireOp",EDGE,"bfa1a572-a1f9-40b2-a836-c3e04a2abb9a")}),-1.0]])]});
            var Q66;
            Q66=makeQuery(id+"F0.imprint","IMPRINT",FACE,{"disambiguationData":[TD([[makeQuery(id+"F0.imprint","IMPRINT",EDGE,{"derivedFrom":sQuery(id+"F0.wireOp",EDGE,"a70be9d8-2ca8-434c-b3fe-2aae981aa060")}),1.0]])]});
            var Q67;
            Q67=makeQuery(id+"F0.imprint","IMPRINT",FACE,{"disambiguationData":[TD([[makeQuery(id+"F0.imprint","IMPRINT",EDGE,{"derivedFrom":sQuery(id+"F0.wireOp",EDGE,"984992f3-7ce3-4161-8e56-36e8aa536630")}),1.0]])]});
            var Q68;
            Q68=makeQuery(id+"F0.imprint","IMPRINT",FACE,{"disambiguationData":[TD([[makeQuery(id+"F0.imprint","IMPRINT",EDGE,{"derivedFrom":sQuery(id+"F0.wireOp",EDGE,"d70aac21-0b34-413f-8a81-50291821fc7c")}),1.0]])]});
            var Q69;
            Q69=makeQuery(id+"F0.imprint","IMPRINT",FACE,{"disambiguationData":[TD([[makeQuery(id+"F0.imprint","IMPRINT",EDGE,{"derivedFrom":sQuery(id+"F0.wireOp",EDGE,"bf7e44ce-545e-4a3a-a0b2-7b6c487773f4.MirrorCS")}),-1.0]])]});
            var Q70;
            Q70=makeQuery(id+"F0.imprint","IMPRINT",FACE,{"disambiguationData":[TD([[makeQuery(id+"F0.imprint","IMPRINT",EDGE,{"derivedFrom":sQuery(id+"F0.wireOp",EDGE,"45c30d2b-ba87-4ed5-b51f-fc0e9da035c6")}),-1.0]])]});
            var Q71;
            Q71=makeQuery(id+"F0.imprint","IMPRINT",FACE,{"disambiguationData":[TD([[makeQuery(id+"F0.imprint","IMPRINT",EDGE,{"derivedFrom":sQuery(id+"F0.wireOp",EDGE,"1c485df4-d575-4356-8471-0de72fb2b36c.MirrorCS")}),-1.0]])]});
            var Q72;
            Q72=makeQuery(id+"F0.imprint","IMPRINT",FACE,{"disambiguationData":[TD([[makeQuery(id+"F0.imprint","IMPRINT",EDGE,{"derivedFrom":sQuery(id+"F0.wireOp",EDGE,"ef3d5e37-b322-4c56-9000-b154395bb826")}),1.0]])]});
            var Q73;
            Q73=makeQuery(id+"F0.imprint","IMPRINT",FACE,{"disambiguationData":[TD([[makeQuery(id+"F0.imprint","IMPRINT",EDGE,{"derivedFrom":sQuery(id+"F0.wireOp",EDGE,"4ca1b0d1-b9a9-4351-bf09-41962642fc45")}),-1.0]])]});
            var Q74;
            Q74=makeQuery(id+"F0.imprint","IMPRINT",FACE,{"disambiguationData":[TD([[makeQuery(id+"F0.imprint","IMPRINT",EDGE,{"derivedFrom":sQuery(id+"F0.wireOp",EDGE,"55628f44-d555-47f8-8bb8-a5d024cf72a8")}),-1.0]])]});
            var Q75;
            Q75=makeQuery(id+"F0.imprint","IMPRINT",FACE,{"disambiguationData":[TD([[makeQuery(id+"F0.imprint","IMPRINT",EDGE,{"derivedFrom":sQuery(id+"F0.wireOp",EDGE,"2bcda4c1-a7b0-4626-8478-850a389ba188")}),1.0]])]});
            var Q76;
            Q76=makeQuery(id+"F0.imprint","IMPRINT",FACE,{"disambiguationData":[TD([[makeQuery(id+"F0.imprint","IMPRINT",EDGE,{"derivedFrom":sQuery(id+"F0.wireOp",EDGE,"7e457187-6a04-47d2-9d7e-5b19782d0155.MirrorCS")}),-1.0]])]});
            var Q77;
            Q77=makeQuery(id+"F0.imprint","IMPRINT",FACE,{"disambiguationData":[TD([[makeQuery(id+"F0.imprint","IMPRINT",EDGE,{"derivedFrom":sQuery(id+"F0.wireOp",EDGE,"c4126aae-9acb-49ae-ba95-605847954749")}),1.0]])]});
            var Q78;
            Q78=makeQuery(id+"F0.imprint","IMPRINT",FACE,{"disambiguationData":[TD([[makeQuery(id+"F0.imprint","IMPRINT",EDGE,{"derivedFrom":sQuery(id+"F0.wireOp",EDGE,"e106da1c-f3cb-4750-8b78-47bcc5eed9b4.MirrorCS")}),-1.0]])]});
            var Q79;
            Q79=makeQuery(id+"F0.imprint","IMPRINT",FACE,{"disambiguationData":[TD([[makeQuery(id+"F0.imprint","IMPRINT",EDGE,{"derivedFrom":sQuery(id+"F0.wireOp",EDGE,"687391b2-608f-4388-be00-f3ba3b0cdae9.MirrorCS")}),1.0]])]});
            var Q80;
            Q80=makeQuery(id+"F0.imprint","IMPRINT",FACE,{"disambiguationData":[TD([[makeQuery(id+"F0.imprint","IMPRINT",EDGE,{"derivedFrom":sQuery(id+"F0.wireOp",EDGE,"83d4a8a6-6797-4a35-9b61-78833aad9cd3.MirrorCS")}),-1.0]])]});
            var Q81;
            Q81=makeQuery(id+"F0.imprint","IMPRINT",FACE,{"disambiguationData":[TD([[makeQuery(id+"F0.imprint","IMPRINT",EDGE,{"derivedFrom":sQuery(id+"F0.wireOp",EDGE,"930746c8-b6ea-4051-80b1-413b92e7b73b.MirrorCS")}),-1.0]])]});
            var Q82;
            Q82=makeQuery(id+"F0.imprint","IMPRINT",FACE,{"disambiguationData":[TD([[makeQuery(id+"F0.imprint","IMPRINT",EDGE,{"derivedFrom":sQuery(id+"F0.wireOp",EDGE,"e9a8c155-b00b-4f90-aca6-eb02adda00da")}),1.0]])]});
            var Q83;
            Q83=makeQuery(id+"F0.imprint","IMPRINT",FACE,{"disambiguationData":[TD([[makeQuery(id+"F0.imprint","IMPRINT",EDGE,{"derivedFrom":sQuery(id+"F0.wireOp",EDGE,"614dc5cd-0402-42db-a272-2973c1ca6f46.MirrorCS")}),-1.0]])]});
            var Q84;
            Q84=makeQuery(id+"F0.imprint","IMPRINT",FACE,{"disambiguationData":[TD([[makeQuery(id+"F0.imprint","IMPRINT",EDGE,{"derivedFrom":sQuery(id+"F0.wireOp",EDGE,"896ead0e-79eb-42ee-84e9-2c01e45dec43.MirrorCS")}),-1.0]])]});
            var Q85;
            Q85=makeQuery(id+"F0.imprint","IMPRINT",FACE,{"disambiguationData":[TD([[makeQuery(id+"F0.imprint","IMPRINT",EDGE,{"derivedFrom":sQuery(id+"F0.wireOp",EDGE,"a36d15a1-651a-48fe-a868-c0545d57ef3523.MirrorCS")}),1.0]])]});
            var Q86;
            Q86=makeQuery(id+"F0.imprint","IMPRINT",FACE,{"disambiguationData":[TD([[makeQuery(id+"F0.imprint","IMPRINT",EDGE,{"derivedFrom":sQuery(id+"F0.wireOp",EDGE,"f937566a-4831-4760-b262-1e84392f5fe5")}),1.0]])]});
            var Q87;
            Q87=makeQuery(id+"F0.imprint","IMPRINT",FACE,{"disambiguationData":[TD([[makeQuery(id+"F0.imprint","IMPRINT",EDGE,{"derivedFrom":sQuery(id+"F0.wireOp",EDGE,"1907961d-e485-47d0-b1d1-648ef04490cc")}),1.0]])]});
            var Q88;
            Q88=makeQuery(id+"F0.imprint","IMPRINT",FACE,{"disambiguationData":[TD([[makeQuery(id+"F0.imprint","IMPRINT",EDGE,{"derivedFrom":sQuery(id+"F0.wireOp",EDGE,"E30")}),-1.0]])]});
            var Q89;
            Q89=makeQuery(id+"F0.imprint","IMPRINT",FACE,{"disambiguationData":[TD([[makeQuery(id+"F0.imprint","IMPRINT",EDGE,{"derivedFrom":sQuery(id+"F0.wireOp",EDGE,"E25")}),-1.0]])]});
            var Q90;
            Q90=makeQuery(id+"F0.imprint","IMPRINT",FACE,{"disambiguationData":[TD([[makeQuery(id+"F0.imprint","IMPRINT",EDGE,{"derivedFrom":sQuery(id+"F0.wireOp",EDGE,"8e5d4706-0bdf-450c-9111-f431ecc40303")}),-1.0]])]});
            var Q91;
            Q91=makeQuery(id+"F0.imprint","IMPRINT",FACE,{"disambiguationData":[TD([[makeQuery(id+"F0.imprint","IMPRINT",EDGE,{"derivedFrom":sQuery(id+"F0.wireOp",EDGE,"2935ac85-5441-43bf-9be7-893b82722d31")}),1.0]])]});
            var Q92;
            Q92=makeQuery(id+"F0.imprint","IMPRINT",FACE,{"disambiguationData":[TD([[makeQuery(id+"F0.imprint","IMPRINT",EDGE,{"derivedFrom":sQuery(id+"F0.wireOp",EDGE,"20a6c459-d186-49cb-afe3-c6b9063006d7")}),-1.0]])]});
            var Q93;
            Q93=makeQuery(id+"F0.imprint","IMPRINT",FACE,{"disambiguationData":[TD([[makeQuery(id+"F0.imprint","IMPRINT",EDGE,{"derivedFrom":sQuery(id+"F0.wireOp",EDGE,"9d547d07-8b58-4eab-be1b-24a12ae78220")}),1.0]])]});
            var Q94;
            Q94=makeQuery(id+"F0.imprint","IMPRINT",FACE,{"disambiguationData":[TD([[makeQuery(id+"F0.imprint","IMPRINT",EDGE,{"derivedFrom":sQuery(id+"F0.wireOp",EDGE,"babb0ecb-76b2-44fd-ae4f-ecb6d7f26535")}),1.0]])]});
            var Q95;
            Q95=makeQuery(id+"F0.imprint","IMPRINT",FACE,{"disambiguationData":[TD([[makeQuery(id+"F0.imprint","IMPRINT",EDGE,{"derivedFrom":sQuery(id+"F0.wireOp",EDGE,"b9095286-4574-4df6-bd63-3ce174a64418")}),-1.0]])]});
            var Q96;
            Q96=makeQuery(id+"F0.imprint","IMPRINT",FACE,{"disambiguationData":[TD([[makeQuery(id+"F0.imprint","IMPRINT",EDGE,{"derivedFrom":sQuery(id+"F0.wireOp",EDGE,"6858a604-43eb-481a-80b9-d1724237938f")}),-1.0]])]});
            var Q97;
            Q97=makeQuery(id+"F0.imprint","IMPRINT",FACE,{"disambiguationData":[TD([[makeQuery(id+"F0.imprint","IMPRINT",EDGE,{"derivedFrom":sQuery(id+"F0.wireOp",EDGE,"e2ec96ad-1cf8-40c4-9192-3c143c93966d")}),-1.0]])]});
            var Q98;
            Q98=makeQuery(id+"F0.imprint","IMPRINT",FACE,{"disambiguationData":[TD([[makeQuery(id+"F0.imprint","IMPRINT",EDGE,{"derivedFrom":sQuery(id+"F0.wireOp",EDGE,"540bedad-7875-459c-86bb-fd8edf0bee21.MirrorCS")}),1.0]])]});
            var Q99;
            Q99=makeQuery(id+"F0.imprint","IMPRINT",FACE,{"disambiguationData":[TD([[makeQuery(id+"F0.imprint","IMPRINT",EDGE,{"derivedFrom":sQuery(id+"F0.wireOp",EDGE,"8ed1b27b-a74b-491a-8a7a-07f137f2b3b9.MirrorCS")}),-1.0]])]});
            var Q100;
            Q100=makeQuery(id+"F0.imprint","IMPRINT",FACE,{"disambiguationData":[TD([[makeQuery(id+"F0.imprint","IMPRINT",EDGE,{"derivedFrom":sQuery(id+"F0.wireOp",EDGE,"dd018b08-eb82-4778-a51c-ca58f3f22463.MirrorCS")}),1.0]])]});
            var Q101;
            Q101=makeQuery(id+"F0.imprint","IMPRINT",FACE,{"disambiguationData":[TD([[makeQuery(id+"F0.imprint","IMPRINT",EDGE,{"derivedFrom":sQuery(id+"F0.wireOp",EDGE,"a6144f18-dc5e-4c6e-b31c-7e3fed000be5.MirrorCS")}),-1.0]])]});
            var Q102;
            Q102=makeQuery(id+"F0.imprint","IMPRINT",FACE,{"disambiguationData":[TD([[makeQuery(id+"F0.imprint","IMPRINT",EDGE,{"derivedFrom":sQuery(id+"F0.wireOp",EDGE,"a36d15a1-651a-48fe-a868-c0545d57ef355.MirrorCS")}),1.0]])]});
            var Q103;
            Q103=makeQuery(id+"F0.imprint","IMPRINT",FACE,{"disambiguationData":[TD([[makeQuery(id+"F0.imprint","IMPRINT",EDGE,{"derivedFrom":sQuery(id+"F0.wireOp",EDGE,"a36d15a1-651a-48fe-a868-c0545d57ef350.MirrorCS")}),-1.0]])]});
            var Q104;
            Q104=makeQuery(id+"F0.imprint","IMPRINT",FACE,{"disambiguationData":[TD([[makeQuery(id+"F0.imprint","IMPRINT",EDGE,{"derivedFrom":sQuery(id+"F0.wireOp",EDGE,"5292e8aa-793e-4388-b925-83b6ac676c8b")}),-1.0]])]});
            var Q105;
            Q105=makeQuery(id+"F0.imprint","IMPRINT",FACE,{"disambiguationData":[TD([[makeQuery(id+"F0.imprint","IMPRINT",EDGE,{"derivedFrom":sQuery(id+"F0.wireOp",EDGE,"6570753b-811f-4365-b11a-a9cbfb38ab35")}),-1.0]])]});
            var Q106;
            Q106=makeQuery(id+"F0.imprint","IMPRINT",FACE,{"disambiguationData":[TD([[makeQuery(id+"F0.imprint","IMPRINT",EDGE,{"derivedFrom":sQuery(id+"F0.wireOp",EDGE,"E418.0")}),-1.0]])]});
            var Q107;
            Q107=makeQuery(id+"F0.imprint","IMPRINT",FACE,{"disambiguationData":[TD([[makeQuery(id+"F0.imprint","IMPRINT",EDGE,{"derivedFrom":sQuery(id+"F0.wireOp",EDGE,"E859.0")}),-1.0]])]});
            var Q108;
            Q108=makeQuery(id+"F0.imprint","IMPRINT",FACE,{"disambiguationData":[TD([[makeQuery(id+"F0.imprint","IMPRINT",EDGE,{"derivedFrom":sQuery(id+"F0.wireOp",EDGE,"E1564.0")}),-1.0]])]});
            var Q109;
            Q109=makeQuery(id+"F0.imprint","IMPRINT",FACE,{"disambiguationData":[TD([[makeQuery(id+"F0.imprint","IMPRINT",EDGE,{"derivedFrom":sQuery(id+"F0.wireOp",EDGE,"E294")}),1.0]])]});
            var Q110;
            Q110=makeQuery(id+"F0.imprint","IMPRINT",FACE,{"disambiguationData":[TD([[makeQuery(id+"F0.imprint","IMPRINT",EDGE,{"derivedFrom":sQuery(id+"F0.wireOp",EDGE,"E288")}),-1.0]])]});
            var Q111;
            Q111=makeQuery(id+"F0.imprint","IMPRINT",FACE,{"disambiguationData":[TD([[makeQuery(id+"F0.imprint","IMPRINT",EDGE,{"derivedFrom":sQuery(id+"F0.wireOp",EDGE,"E288")}),1.0]])]});
            var Q112;
            Q112=makeQuery(id+"F0.imprint","IMPRINT",FACE,{"disambiguationData":[TD([[makeQuery(id+"F0.imprint","IMPRINT",EDGE,{"derivedFrom":sQuery(id+"F0.wireOp",EDGE,"E289")}),-1.0]])]});
            var Q113;
            Q113=makeQuery(id+"F0.imprint","IMPRINT",FACE,{"disambiguationData":[TD([[makeQuery(id+"F0.imprint","IMPRINT",EDGE,{"derivedFrom":sQuery(id+"F0.wireOp",EDGE,"E405")}),-1.0]])]});
            var Q114;
            Q114=makeQuery(id+"F0.imprint","IMPRINT",FACE,{"disambiguationData":[TD([[makeQuery(id+"F0.imprint","IMPRINT",EDGE,{"derivedFrom":sQuery(id+"F0.wireOp",EDGE,"E345")}),1.0]])]});
            var Q115;
            Q115=makeQuery(id+"F0.imprint","IMPRINT",FACE,{"disambiguationData":[TD([[makeQuery(id+"F0.imprint","IMPRINT",EDGE,{"derivedFrom":sQuery(id+"F0.wireOp",EDGE,"E405")}),1.0]])]});
            var Q116;
            Q116=makeQuery(id+"F0.imprint","IMPRINT",FACE,{"disambiguationData":[TD([[makeQuery(id+"F0.imprint","IMPRINT",EDGE,{"derivedFrom":sQuery(id+"F0.wireOp",EDGE,"E618")}),-1.0]])]});
            var Q117;
            Q117=makeQuery(id+"F0.imprint","IMPRINT",FACE,{"disambiguationData":[TD([[makeQuery(id+"F0.imprint","IMPRINT",EDGE,{"derivedFrom":sQuery(id+"F0.wireOp",EDGE,"E618")}),1.0]])]});
            var Q118;
            Q118=makeQuery(id+"F0.imprint","IMPRINT",FACE,{"disambiguationData":[TD([[makeQuery(id+"F0.imprint","IMPRINT",EDGE,{"derivedFrom":sQuery(id+"F0.wireOp",EDGE,"E620")}),1.0]])]});
            var Q119;
            Q119=makeQuery(id+"F0.imprint","IMPRINT",FACE,{"disambiguationData":[TD([[makeQuery(id+"F0.imprint","IMPRINT",EDGE,{"derivedFrom":sQuery(id+"F0.wireOp",EDGE,"E715.MirrorCS")}),-1.0]])]});
            var Q120;
            Q120=makeQuery(id+"F0.imprint","IMPRINT",FACE,{"disambiguationData":[TD([[makeQuery(id+"F0.imprint","IMPRINT",EDGE,{"derivedFrom":sQuery(id+"F0.wireOp",EDGE,"E605")}),1.0]])]});
            var Q121;
            Q121=makeQuery(id+"F0.imprint","IMPRINT",FACE,{"disambiguationData":[TD([[makeQuery(id+"F0.imprint","IMPRINT",EDGE,{"derivedFrom":sQuery(id+"F0.wireOp",EDGE,"E704")}),-1.0]])]});
            var Q122;
            Q122=makeQuery(id+"F0.imprint","IMPRINT",FACE,{"disambiguationData":[TD([[makeQuery(id+"F0.imprint","IMPRINT",EDGE,{"derivedFrom":sQuery(id+"F0.wireOp",EDGE,"E948")}),1.0]])]});
            var Q123;
            Q123=makeQuery(id+"F0.imprint","IMPRINT",FACE,{"disambiguationData":[TD([[makeQuery(id+"F0.imprint","IMPRINT",EDGE,{"derivedFrom":sQuery(id+"F0.wireOp",EDGE,"E948")}),-1.0]])]});
            var Q124;
            Q124=makeQuery(id+"F0.imprint","IMPRINT",FACE,{"disambiguationData":[TD([[makeQuery(id+"F0.imprint","IMPRINT",EDGE,{"derivedFrom":sQuery(id+"F0.wireOp",EDGE,"E605")}),-1.0]])]});
            var Q125;
            Q125=makeQuery(id+"F0.imprint","IMPRINT",FACE,{"disambiguationData":[TD([[makeQuery(id+"F0.imprint","IMPRINT",EDGE,{"derivedFrom":sQuery(id+"F0.wireOp",EDGE,"E567")}),1.0]])]});
            var Q126;
            Q126=makeQuery(id+"F0.imprint","IMPRINT",FACE,{"disambiguationData":[TD([[makeQuery(id+"F0.imprint","IMPRINT",EDGE,{"derivedFrom":sQuery(id+"F0.wireOp",EDGE,"E392.MirrorCS")}),-1.0]])]});
            var Q127;
            Q127=makeQuery(id+"F0.imprint","IMPRINT",FACE,{"disambiguationData":[TD([[makeQuery(id+"F0.imprint","IMPRINT",EDGE,{"derivedFrom":sQuery(id+"F0.wireOp",EDGE,"E679.MirrorCS")}),-1.0]])]});
            var Q128;
            Q128=makeQuery(id+"F0.imprint","IMPRINT",FACE,{"disambiguationData":[TD([[makeQuery(id+"F0.imprint","IMPRINT",EDGE,{"derivedFrom":sQuery(id+"F0.wireOp",EDGE,"E369.MirrorCS")}),1.0]])]});
            var Q129;
            Q129=makeQuery(id+"F0.imprint","IMPRINT",FACE,{"disambiguationData":[TD([[makeQuery(id+"F0.imprint","IMPRINT",EDGE,{"derivedFrom":sQuery(id+"F0.wireOp",EDGE,"E274")}),1.0]])]});
            var Q130;
            Q130=makeQuery(id+"F0.imprint","IMPRINT",FACE,{"disambiguationData":[TD([[makeQuery(id+"F0.imprint","IMPRINT",EDGE,{"derivedFrom":sQuery(id+"F0.wireOp",EDGE,"E985")}),1.0]])]});
            var Q131;
            Q131=makeQuery(id+"F0.imprint","IMPRINT",FACE,{"disambiguationData":[TD([[makeQuery(id+"F0.imprint","IMPRINT",EDGE,{"derivedFrom":sQuery(id+"F0.wireOp",EDGE,"E1023")}),1.0]])]});
            var Q132;
            Q132=makeQuery(id+"F0.imprint","IMPRINT",FACE,{"disambiguationData":[TD([[makeQuery(id+"F0.imprint","IMPRINT",EDGE,{"derivedFrom":sQuery(id+"F0.wireOp",EDGE,"E1235")}),-1.0]])]});
            var Q133;
            Q133=makeQuery(id+"F0.imprint","IMPRINT",FACE,{"disambiguationData":[TD([[makeQuery(id+"F0.imprint","IMPRINT",EDGE,{"derivedFrom":sQuery(id+"F0.wireOp",EDGE,"E1023")}),-1.0]])]});
            var Q134;
            Q134=makeQuery(id+"F0.imprint","IMPRINT",FACE,{"disambiguationData":[TD([[makeQuery(id+"F0.imprint","IMPRINT",EDGE,{"derivedFrom":sQuery(id+"F0.wireOp",EDGE,"E1236")}),-1.0]])]});
            var Q135;
            Q135=makeQuery(id+"F0.imprint","IMPRINT",FACE,{"disambiguationData":[TD([[makeQuery(id+"F0.imprint","IMPRINT",EDGE,{"derivedFrom":sQuery(id+"F0.wireOp",EDGE,"E1235")}),1.0]])]});
            var Q136;
            Q136=makeQuery(id+"F0.imprint","IMPRINT",FACE,{"disambiguationData":[TD([[makeQuery(id+"F0.imprint","IMPRINT",EDGE,{"derivedFrom":sQuery(id+"F0.wireOp",EDGE,"E1000.MirrorCS")}),1.0]])]});
            var Q137;
            Q137=makeQuery(id+"F0.imprint","IMPRINT",FACE,{"disambiguationData":[TD([[makeQuery(id+"F0.imprint","IMPRINT",EDGE,{"derivedFrom":sQuery(id+"F0.wireOp",EDGE,"E935")}),1.0]])]});
            var Q138;
            Q138=makeQuery(id+"F0.imprint","IMPRINT",FACE,{"disambiguationData":[TD([[makeQuery(id+"F0.imprint","IMPRINT",EDGE,{"derivedFrom":sQuery(id+"F0.wireOp",EDGE,"E1296.MirrorCS")}),-1.0]])]});
            var Q139;
            Q139=makeQuery(id+"F0.imprint","IMPRINT",FACE,{"disambiguationData":[TD([[makeQuery(id+"F0.imprint","IMPRINT",EDGE,{"derivedFrom":sQuery(id+"F0.wireOp",EDGE,"E1014.MirrorCS")}),-1.0]])]});
            var Q140;
            Q140=makeQuery(id+"F0.imprint","IMPRINT",FACE,{"disambiguationData":[TD([[makeQuery(id+"F0.imprint","IMPRINT",EDGE,{"derivedFrom":sQuery(id+"F0.wireOp",EDGE,"E1237")}),1.0]])]});
            var Q141;
            Q141=makeQuery(id+"F0.imprint","IMPRINT",FACE,{"disambiguationData":[TD([[makeQuery(id+"F0.imprint","IMPRINT",EDGE,{"derivedFrom":sQuery(id+"F0.wireOp",EDGE,"E1332.MirrorCS")}),-1.0]])]});
            var Q142;
            Q142=makeQuery(id+"F0.imprint","IMPRINT",FACE,{"disambiguationData":[TD([[makeQuery(id+"F0.imprint","IMPRINT",EDGE,{"derivedFrom":sQuery(id+"F0.wireOp",EDGE,"E1321")}),-1.0]])]});
            var Q143;
            Q143=makeQuery(id+"F0.imprint","IMPRINT",FACE,{"disambiguationData":[TD([[makeQuery(id+"F0.imprint","IMPRINT",EDGE,{"derivedFrom":sQuery(id+"F0.wireOp",EDGE,"E1222")}),1.0]])]});
            var Q144;
            Q144=makeQuery(id+"F0.imprint","IMPRINT",FACE,{"disambiguationData":[TD([[makeQuery(id+"F0.imprint","IMPRINT",EDGE,{"derivedFrom":sQuery(id+"F0.wireOp",EDGE,"E1565")}),1.0]])]});
            var Q145;
            Q145=makeQuery(id+"F0.imprint","IMPRINT",FACE,{"disambiguationData":[TD([[makeQuery(id+"F0.imprint","IMPRINT",EDGE,{"derivedFrom":sQuery(id+"F0.wireOp",EDGE,"E1565")}),-1.0]])]});
            var Q146;
            Q146=makeQuery(id+"F0.imprint","IMPRINT",FACE,{"disambiguationData":[TD([[makeQuery(id+"F0.imprint","IMPRINT",EDGE,{"derivedFrom":sQuery(id+"F0.wireOp",EDGE,"E1222")}),-1.0]])]});
            var Q147;
            Q147=makeQuery(id+"F0.imprint","IMPRINT",FACE,{"disambiguationData":[TD([[makeQuery(id+"F0.imprint","IMPRINT",EDGE,{"derivedFrom":sQuery(id+"F0.wireOp",EDGE,"E1184")}),1.0]])]});
            var Q148;
            Q148=makeQuery(id+"F0.imprint","IMPRINT",FACE,{"disambiguationData":[TD([[makeQuery(id+"F0.imprint","IMPRINT",EDGE,{"derivedFrom":sQuery(id+"F0.wireOp",EDGE,"E1640")}),-1.0]])]});
            var Q149;
            Q149=makeQuery(id+"F0.imprint","IMPRINT",FACE,{"disambiguationData":[TD([[makeQuery(id+"F0.imprint","IMPRINT",EDGE,{"derivedFrom":sQuery(id+"F0.wireOp",EDGE,"E1602")}),1.0]])]});
            var Q150;
            Q150=makeQuery(id+"F0.imprint","IMPRINT",FACE,{"disambiguationData":[TD([[makeQuery(id+"F0.imprint","IMPRINT",EDGE,{"derivedFrom":sQuery(id+"F0.wireOp",EDGE,"E1617.MirrorCS")}),1.0]])]});
            var Q151;
            Q151=makeQuery(id+"F0.imprint","IMPRINT",FACE,{"disambiguationData":[TD([[makeQuery(id+"F0.imprint","IMPRINT",EDGE,{"derivedFrom":sQuery(id+"F0.wireOp",EDGE,"E1552")}),1.0]])]});
            var Q152;
            Q152=makeQuery(id+"F0.imprint","IMPRINT",FACE,{"disambiguationData":[TD([[makeQuery(id+"F0.imprint","IMPRINT",EDGE,{"derivedFrom":sQuery(id+"F0.wireOp",EDGE,"E1552")}),-1.0]])]});
            var Q153;
            Q153=makeQuery(id+"F0.imprint","IMPRINT",FACE,{"disambiguationData":[TD([[makeQuery(id+"F0.imprint","IMPRINT",EDGE,{"derivedFrom":sQuery(id+"F0.wireOp",EDGE,"E1514")}),1.0]])]});
            var Q154;
            Q154=makeQuery(id+"F0.imprint","IMPRINT",FACE,{"disambiguationData":[TD([[makeQuery(id+"F0.imprint","IMPRINT",EDGE,{"derivedFrom":sQuery(id+"F0.wireOp",EDGE,"E1607.MirrorCS")}),-1.0]])]});
            var Q155;
            Q155=makeQuery(id+"F0.imprint","IMPRINT",FACE,{"disambiguationData":[TD([[makeQuery(id+"F0.imprint","IMPRINT",EDGE,{"derivedFrom":sQuery(id+"F0.wireOp",EDGE,"E1213.MirrorCS")}),-1.0]])]});
            var Q156;
            Q156=makeQuery(id+"F0.imprint","IMPRINT",FACE,{"disambiguationData":[TD([[makeQuery(id+"F0.imprint","IMPRINT",EDGE,{"derivedFrom":sQuery(id+"F0.wireOp",EDGE,"E1134")}),1.0]])]});
            var Q157;
            Q157=makeQuery(id+"F0.imprint","IMPRINT",FACE,{"disambiguationData":[TD([[makeQuery(id+"F0.imprint","IMPRINT",EDGE,{"derivedFrom":sQuery(id+"F0.wireOp",EDGE,"E1199.MirrorCS")}),1.0]])]});
            var Q158;
            Q158=makeQuery(id+"F0.imprint","IMPRINT",FACE,{"disambiguationData":[TD([[makeQuery(id+"F0.imprint","IMPRINT",EDGE,{"derivedFrom":sQuery(id+"F0.wireOp",EDGE,"E1529.MirrorCS")}),1.0]])]});
            var Q159;
            Q159=makeQuery(id+"F0.imprint","IMPRINT",FACE,{"disambiguationData":[TD([[makeQuery(id+"F0.imprint","IMPRINT",EDGE,{"derivedFrom":sQuery(id+"F0.wireOp",EDGE,"E1464")}),1.0]])]});
            var Q160;
            Q160=makeQuery(id+"F0.imprint","IMPRINT",FACE,{"disambiguationData":[TD([[makeQuery(id+"F0.imprint","IMPRINT",EDGE,{"derivedFrom":sQuery(id+"F0.wireOp",EDGE,"E1464")}),-1.0]])]});
            var Q161;
            Q161=makeQuery(id+"F0.imprint","IMPRINT",FACE,{"disambiguationData":[TD([[makeQuery(id+"F0.imprint","IMPRINT",EDGE,{"derivedFrom":sQuery(id+"F0.wireOp",EDGE,"E1403")}),1.0]])]});
            var Q162;
            Q162=makeQuery(id+"F0.imprint","IMPRINT",FACE,{"disambiguationData":[TD([[makeQuery(id+"F0.imprint","IMPRINT",EDGE,{"derivedFrom":sQuery(id+"F0.wireOp",EDGE,"E1519.MirrorCS")}),-1.0]])]});
            var Q163;
            Q163=makeQuery(id+"F0.imprint","IMPRINT",FACE,{"disambiguationData":[TD([[makeQuery(id+"F0.imprint","IMPRINT",EDGE,{"derivedFrom":sQuery(id+"F0.wireOp",EDGE,"E1123.MirrorCS")}),-1.0]])]});
            var Q164;
            Q164=makeQuery(id+"F0.imprint","IMPRINT",FACE,{"disambiguationData":[TD([[makeQuery(id+"F0.imprint","IMPRINT",EDGE,{"derivedFrom":sQuery(id+"F0.wireOp",EDGE,"E1109.MirrorCS")}),1.0]])]});
            var Q165;
            Q165=makeQuery(id+"F0.imprint","IMPRINT",FACE,{"disambiguationData":[TD([[makeQuery(id+"F0.imprint","IMPRINT",EDGE,{"derivedFrom":sQuery(id+"F0.wireOp",EDGE,"E1094")}),1.0]])]});
            var Q166;
            Q166=makeQuery(id+"F0.imprint","IMPRINT",FACE,{"disambiguationData":[TD([[makeQuery(id+"F0.imprint","IMPRINT",EDGE,{"derivedFrom":sQuery(id+"F0.wireOp",EDGE,"E926.MirrorCS")}),-1.0]])]});
            var Q167;
            Q167=makeQuery(id+"F0.imprint","IMPRINT",FACE,{"disambiguationData":[TD([[makeQuery(id+"F0.imprint","IMPRINT",EDGE,{"derivedFrom":sQuery(id+"F0.wireOp",EDGE,"E1125")}),1.0]])]});
            var Q168;
            Q168=makeQuery(id+"F0.imprint","IMPRINT",FACE,{"disambiguationData":[TD([[makeQuery(id+"F0.imprint","IMPRINT",EDGE,{"derivedFrom":sQuery(id+"F0.wireOp",EDGE,"E1134")}),-1.0]])]});
            var Q169;
            Q169=makeQuery(id+"F0.imprint","IMPRINT",FACE,{"disambiguationData":[TD([[makeQuery(id+"F0.imprint","IMPRINT",EDGE,{"derivedFrom":sQuery(id+"F0.wireOp",EDGE,"E1426.MirrorCS")}),1.0]])]});
            var Q170;
            Q170=makeQuery(id+"F0.imprint","IMPRINT",FACE,{"disambiguationData":[TD([[makeQuery(id+"F0.imprint","IMPRINT",EDGE,{"derivedFrom":sQuery(id+"F0.wireOp",EDGE,"E1455")}),1.0]])]});
            var Q171;
            Q171=makeQuery(id+"F0.imprint","IMPRINT",FACE,{"disambiguationData":[TD([[makeQuery(id+"F0.imprint","IMPRINT",EDGE,{"derivedFrom":sQuery(id+"F0.wireOp",EDGE,"E1413.MirrorCS")}),-1.0]])]});
            var Q172;
            Q172=makeQuery(id+"F0.imprint","IMPRINT",FACE,{"disambiguationData":[TD([[makeQuery(id+"F0.imprint","IMPRINT",EDGE,{"derivedFrom":sQuery(id+"F0.wireOp",EDGE,"E1412.MirrorCS")}),-1.0]])]});
            var Q173;
            Q173=makeQuery(id+"F0.imprint","IMPRINT",FACE,{"disambiguationData":[TD([[makeQuery(id+"F0.imprint","IMPRINT",EDGE,{"derivedFrom":sQuery(id+"F0.wireOp",EDGE,"E1125")}),-1.0]])]});
            var Q174;
            Q174=makeQuery(id+"F0.imprint","IMPRINT",FACE,{"disambiguationData":[TD([[makeQuery(id+"F0.imprint","IMPRINT",EDGE,{"derivedFrom":sQuery(id+"F0.wireOp",EDGE,"E1099.MirrorCS")}),-1.0]])]});
            var Q175;
            Q175=makeQuery(id+"F0.imprint","IMPRINT",FACE,{"disambiguationData":[TD([[makeQuery(id+"F0.imprint","IMPRINT",EDGE,{"derivedFrom":sQuery(id+"F0.wireOp",EDGE,"E809.MirrorCS")}),1.0]])]});
            var Q176;
            Q176=makeQuery(id+"F0.imprint","IMPRINT",FACE,{"disambiguationData":[TD([[makeQuery(id+"F0.imprint","IMPRINT",EDGE,{"derivedFrom":sQuery(id+"F0.wireOp",EDGE,"E838")}),1.0]])]});
            var Q177;
            Q177=makeQuery(id+"F0.imprint","IMPRINT",FACE,{"disambiguationData":[TD([[makeQuery(id+"F0.imprint","IMPRINT",EDGE,{"derivedFrom":sQuery(id+"F0.wireOp",EDGE,"E786")}),1.0]])]});
            var Q178;
            Q178=makeQuery(id+"F0.imprint","IMPRINT",FACE,{"disambiguationData":[TD([[makeQuery(id+"F0.imprint","IMPRINT",EDGE,{"derivedFrom":sQuery(id+"F0.wireOp",EDGE,"E796.MirrorCS")}),-1.0]])]});
            var Q179;
            Q179=makeQuery(id+"F0.imprint","IMPRINT",FACE,{"disambiguationData":[TD([[makeQuery(id+"F0.imprint","IMPRINT",EDGE,{"derivedFrom":sQuery(id+"F0.wireOp",EDGE,"E506.MirrorCS")}),-1.0]])]});
            var Q180;
            Q180=makeQuery(id+"F0.imprint","IMPRINT",FACE,{"disambiguationData":[TD([[makeQuery(id+"F0.imprint","IMPRINT",EDGE,{"derivedFrom":sQuery(id+"F0.wireOp",EDGE,"E1363")}),1.0]])]});
            var Q181;
            Q181=makeQuery(id+"F0.imprint","IMPRINT",FACE,{"disambiguationData":[TD([[makeQuery(id+"F0.imprint","IMPRINT",EDGE,{"derivedFrom":sQuery(id+"F0.wireOp",EDGE,"E1404.MirrorCS")}),1.0]])]});
            var Q182;
            Q182=makeQuery(id+"F0.imprint","IMPRINT",FACE,{"disambiguationData":[TD([[makeQuery(id+"F0.imprint","IMPRINT",EDGE,{"derivedFrom":sQuery(id+"F0.wireOp",EDGE,"E795.MirrorCS")}),-1.0]])]});
            var Q183;
            Q183=makeQuery(id+"F0.imprint","IMPRINT",FACE,{"disambiguationData":[TD([[makeQuery(id+"F0.imprint","IMPRINT",EDGE,{"derivedFrom":sQuery(id+"F0.wireOp",EDGE,"E746")}),1.0]])]});
            var Q184;
            Q184=makeQuery(id+"F0.imprint","IMPRINT",FACE,{"disambiguationData":[TD([[makeQuery(id+"F0.imprint","IMPRINT",EDGE,{"derivedFrom":sQuery(id+"F0.wireOp",EDGE,"E787.MirrorCS")}),1.0]])]});
            var Q185;
            Q185=makeQuery(id+"F0.imprint","IMPRINT",FACE,{"disambiguationData":[TD([[makeQuery(id+"F0.imprint","IMPRINT",EDGE,{"derivedFrom":sQuery(id+"F0.wireOp",EDGE,"E508")}),-1.0]])]});
            var Q186;
            Q186=makeQuery(id+"F0.imprint","IMPRINT",FACE,{"disambiguationData":[TD([[makeQuery(id+"F0.imprint","IMPRINT",EDGE,{"derivedFrom":sQuery(id+"F0.wireOp",EDGE,"E508")}),1.0]])]});
            var Q187;
            Q187=makeQuery(id+"F0.imprint","IMPRINT",FACE,{"disambiguationData":[TD([[makeQuery(id+"F0.imprint","IMPRINT",EDGE,{"derivedFrom":sQuery(id+"F0.wireOp",EDGE,"E482.MirrorCS")}),-1.0]])]});
            var Q188;
            Q188=makeQuery(id+"F0.imprint","IMPRINT",FACE,{"disambiguationData":[TD([[makeQuery(id+"F0.imprint","IMPRINT",EDGE,{"derivedFrom":sQuery(id+"F0.wireOp",EDGE,"E105.MirrorCS")}),1.0]])]});
            var Q189;
            Q189=makeQuery(id+"F0.imprint","IMPRINT",FACE,{"disambiguationData":[TD([[makeQuery(id+"F0.imprint","IMPRINT",EDGE,{"derivedFrom":sQuery(id+"F0.wireOp",EDGE,"E81")}),1.0]])]});
            var Q190;
            Q190=makeQuery(id+"F0.imprint","IMPRINT",FACE,{"disambiguationData":[TD([[makeQuery(id+"F0.imprint","IMPRINT",EDGE,{"derivedFrom":sQuery(id+"F0.wireOp",EDGE,"E492.MirrorCS")}),1.0]])]});
            var Q191;
            Q191=makeQuery(id+"F0.imprint","IMPRINT",FACE,{"disambiguationData":[TD([[makeQuery(id+"F0.imprint","IMPRINT",EDGE,{"derivedFrom":sQuery(id+"F0.wireOp",EDGE,"E902.MirrorCS")}),-1.0]])]});
            var Q192;
            Q192=makeQuery(id+"F0.imprint","IMPRINT",FACE,{"disambiguationData":[TD([[makeQuery(id+"F0.imprint","IMPRINT",EDGE,{"derivedFrom":sQuery(id+"F0.wireOp",EDGE,"E477")}),1.0]])]});
            var Q193;
            Q193=makeQuery(id+"F0.imprint","IMPRINT",FACE,{"disambiguationData":[TD([[makeQuery(id+"F0.imprint","IMPRINT",EDGE,{"derivedFrom":sQuery(id+"F0.wireOp",EDGE,"E596.MirrorCS")}),-1.0]])]});
            var Q194;
            Q194=makeQuery(id+"F0.imprint","IMPRINT",FACE,{"disambiguationData":[TD([[makeQuery(id+"F0.imprint","IMPRINT",EDGE,{"derivedFrom":sQuery(id+"F0.wireOp",EDGE,"E261.MirrorCS")}),-1.0]])]});
            var Q195;
            Q195=makeQuery(id+"F0.imprint","IMPRINT",FACE,{"disambiguationData":[TD([[makeQuery(id+"F0.imprint","IMPRINT",EDGE,{"derivedFrom":sQuery(id+"F0.wireOp",EDGE,"E62")}),-1.0]])]});
            var Q196;
            Q196=makeQuery(id+"F0.imprint","IMPRINT",FACE,{"disambiguationData":[TD([[makeQuery(id+"F0.imprint","IMPRINT",EDGE,{"derivedFrom":sQuery(id+"F0.wireOp",EDGE,"E223.MirrorCS")}),-1.0]])]});
            var Q197;
            Q197=makeQuery(id+"F0.imprint","IMPRINT",FACE,{"disambiguationData":[TD([[makeQuery(id+"F0.imprint","IMPRINT",EDGE,{"derivedFrom":sQuery(id+"F0.wireOp",EDGE,"E143")}),1.0]])]});
            var Q198;
            Q198=makeQuery(id+"F0.imprint","IMPRINT",FACE,{"disambiguationData":[TD([[makeQuery(id+"F0.imprint","IMPRINT",EDGE,{"derivedFrom":sQuery(id+"F0.wireOp",EDGE,"E63")}),1.0]])]});
            var Q199;
            Q199=makeQuery(id+"F0.imprint","IMPRINT",FACE,{"disambiguationData":[TD([[makeQuery(id+"F0.imprint","IMPRINT",EDGE,{"derivedFrom":sQuery(id+"F0.wireOp",EDGE,"E143")}),-1.0]])]});
            var Q200;
            Q200=makeQuery(id+"F0.imprint","IMPRINT",FACE,{"disambiguationData":[TD([[makeQuery(id+"F0.imprint","IMPRINT",EDGE,{"derivedFrom":sQuery(id+"F0.wireOp",EDGE,"E215.MirrorCS")}),1.0]])]});
            var Q201;
            Q201=makeQuery(id+"F0.imprint","IMPRINT",FACE,{"disambiguationData":[TD([[makeQuery(id+"F0.imprint","IMPRINT",EDGE,{"derivedFrom":sQuery(id+"F0.wireOp",EDGE,"E238.MirrorCS")}),1.0]])]});
            var Q202;
            Q202=makeQuery(id+"F0.imprint","IMPRINT",FACE,{"disambiguationData":[TD([[makeQuery(id+"F0.imprint","IMPRINT",EDGE,{"derivedFrom":sQuery(id+"F0.wireOp",EDGE,"E572.MirrorCS")}),-1.0]])]});
            var Q203;
            Q203=makeQuery(id+"F0.imprint","IMPRINT",FACE,{"disambiguationData":[TD([[makeQuery(id+"F0.imprint","IMPRINT",EDGE,{"derivedFrom":sQuery(id+"F0.wireOp",EDGE,"E214")}),1.0]])]});
            var Q204;
            Q204=makeQuery(id+"F0.imprint","IMPRINT",FACE,{"disambiguationData":[TD([[makeQuery(id+"F0.imprint","IMPRINT",EDGE,{"derivedFrom":sQuery(id+"F0.wireOp",EDGE,"E274")}),-1.0]])]});
            var Q205;
            Q205=makeQuery(id+"F0.imprint","IMPRINT",FACE,{"disambiguationData":[TD([[makeQuery(id+"F0.imprint","IMPRINT",EDGE,{"derivedFrom":sQuery(id+"F0.wireOp",EDGE,"E354.MirrorCS")}),-1.0]])]});
            var Q206;
            Q206=makeQuery(id+"F0.imprint","IMPRINT",FACE,{"disambiguationData":[TD([[makeQuery(id+"F0.imprint","IMPRINT",EDGE,{"derivedFrom":sQuery(id+"F0.wireOp",EDGE,"E195")}),-1.0]])]});
            var Q207;
            Q207=makeQuery(id+"F0.imprint","IMPRINT",FACE,{"disambiguationData":[TD([[makeQuery(id+"F0.imprint","IMPRINT",EDGE,{"derivedFrom":sQuery(id+"F0.wireOp",EDGE,"E163")}),-1.0]])]});
            var Q208;
            Q208=makeQuery(id+"F0.imprint","IMPRINT",FACE,{"disambiguationData":[TD([[makeQuery(id+"F0.imprint","IMPRINT",EDGE,{"derivedFrom":sQuery(id+"F0.wireOp",EDGE,"E163")}),1.0]])]});
            var Q209;
            Q209=makeQuery(id+"F0.imprint","IMPRINT",FACE,{"disambiguationData":[TD([[makeQuery(id+"F0.imprint","IMPRINT",EDGE,{"derivedFrom":sQuery(id+"F0.wireOp",EDGE,"E196")}),1.0]])]});
            var Q210;
            Q210=makeQuery(id+"F0.imprint","IMPRINT",FACE,{"disambiguationData":[TD([[makeQuery(id+"F0.imprint","IMPRINT",EDGE,{"derivedFrom":sQuery(id+"F0.wireOp",EDGE,"E346.MirrorCS")}),1.0]])]});
            var Q211;
            Q211=makeQuery(id+"F0.imprint","IMPRINT",FACE,{"disambiguationData":[TD([[makeQuery(id+"F0.imprint","IMPRINT",EDGE,{"derivedFrom":sQuery(id+"F0.wireOp",EDGE,"E294")}),-1.0]])]});
            var Q212;
            Q212=makeQuery(id+"F0.imprint","IMPRINT",FACE,{"disambiguationData":[TD([[makeQuery(id+"F0.imprint","IMPRINT",EDGE,{"derivedFrom":sQuery(id+"F0.wireOp",EDGE,"E517")}),1.0]])]});
            var Q213;
            Q213=makeQuery(id+"F0.imprint","IMPRINT",FACE,{"disambiguationData":[TD([[makeQuery(id+"F0.imprint","IMPRINT",EDGE,{"derivedFrom":sQuery(id+"F0.wireOp",EDGE,"E990.MirrorCS")}),-1.0]])]});
            var Q214;
            Q214=makeQuery(id+"F0.imprint","IMPRINT",FACE,{"disambiguationData":[TD([[makeQuery(id+"F0.imprint","IMPRINT",EDGE,{"derivedFrom":sQuery(id+"F0.wireOp",EDGE,"E582.MirrorCS")}),1.0]])]});
            var Q215;
            Q215=makeQuery(id+"F0.imprint","IMPRINT",FACE,{"disambiguationData":[TD([[makeQuery(id+"F0.imprint","IMPRINT",EDGE,{"derivedFrom":sQuery(id+"F0.wireOp",EDGE,"E897")}),1.0]])]});
            var Q216;
            Q216=makeQuery(id+"F0.imprint","IMPRINT",FACE,{"disambiguationData":[TD([[makeQuery(id+"F0.imprint","IMPRINT",EDGE,{"derivedFrom":sQuery(id+"F0.wireOp",EDGE,"E935")}),-1.0]])]});
            var Q217;
            Q217=makeQuery(id+"F0.imprint","IMPRINT",FACE,{"disambiguationData":[TD([[makeQuery(id+"F0.imprint","IMPRINT",EDGE,{"derivedFrom":sQuery(id+"F0.wireOp",EDGE,"E847")}),1.0]])]});
            var Q218;
            Q218=makeQuery(id+"F0.imprint","IMPRINT",FACE,{"disambiguationData":[TD([[makeQuery(id+"F0.imprint","IMPRINT",EDGE,{"derivedFrom":sQuery(id+"F0.wireOp",EDGE,"E912.MirrorCS")}),1.0]])]});
            var Q219;
            Q219=makeQuery(id+"F0.imprint","IMPRINT",FACE,{"disambiguationData":[TD([[makeQuery(id+"F0.imprint","IMPRINT",EDGE,{"derivedFrom":sQuery(id+"F0.wireOp",EDGE,"E1189.MirrorCS")}),-1.0]])]});
            extrude(context, id + "F1", {"entities" : qUnion([Q0, Q1, Q2, Q3, Q4, Q5, Q6, Q7, Q8, Q9, Q10, Q11, Q12, Q13, Q14, Q15, Q16, Q17, Q18, Q19, Q20, Q21, Q22, Q23, Q24, Q25, Q26, Q27, Q28, Q29, Q30, Q31, Q32, Q33, Q34, Q35, Q36, Q37, Q38, Q39, Q40, Q41, Q42, Q43, Q44, Q45, Q46, Q47, Q48, Q49, Q50, Q51, Q52, Q53, Q54, Q55, Q56, Q57, Q58, Q59, Q60, Q61, Q62, Q63, Q64, Q65, Q66, Q67, Q68, Q69, Q70, Q71, Q72, Q73, Q74, Q75, Q76, Q77, Q78, Q79, Q80, Q81, Q82, Q83, Q84, Q85, Q86, Q87, Q88, Q89, Q90, Q91, Q92, Q93, Q94, Q95, Q96, Q97, Q98, Q99, Q100, Q101, Q102, Q103, Q104, Q105, Q106, Q107, Q108, Q109, Q110, Q111, Q112, Q113, Q114, Q115, Q116, Q117, Q118, Q119, Q120, Q121, Q122, Q123, Q124, Q125, Q126, Q127, Q128, Q129, Q130, Q131, Q132, Q133, Q134, Q135, Q136, Q137, Q138, Q139, Q140, Q141, Q142, Q143, Q144, Q145, Q146, Q147, Q148, Q149, Q150, Q151, Q152, Q153, Q154, Q155, Q156, Q157, Q158, Q159, Q160, Q161, Q162, Q163, Q164, Q165, Q166, Q167, Q168, Q169, Q170, Q171, Q172, Q173, Q174, Q175, Q176, Q177, Q178, Q179, Q180, Q181, Q182, Q183, Q184, Q185, Q186, Q187, Q188, Q189, Q190, Q191, Q192, Q193, Q194, Q195, Q196, Q197, Q198, Q199, Q200, Q201, Q202, Q203, Q204, Q205, Q206, Q207, Q208, Q209, Q210, Q211, Q212, Q213, Q214, Q215, Q216, Q217, Q218, Q219]), "depth" : 3.17 * mm, "offsetDistance" : 25.4 * mm});
        }
    });
